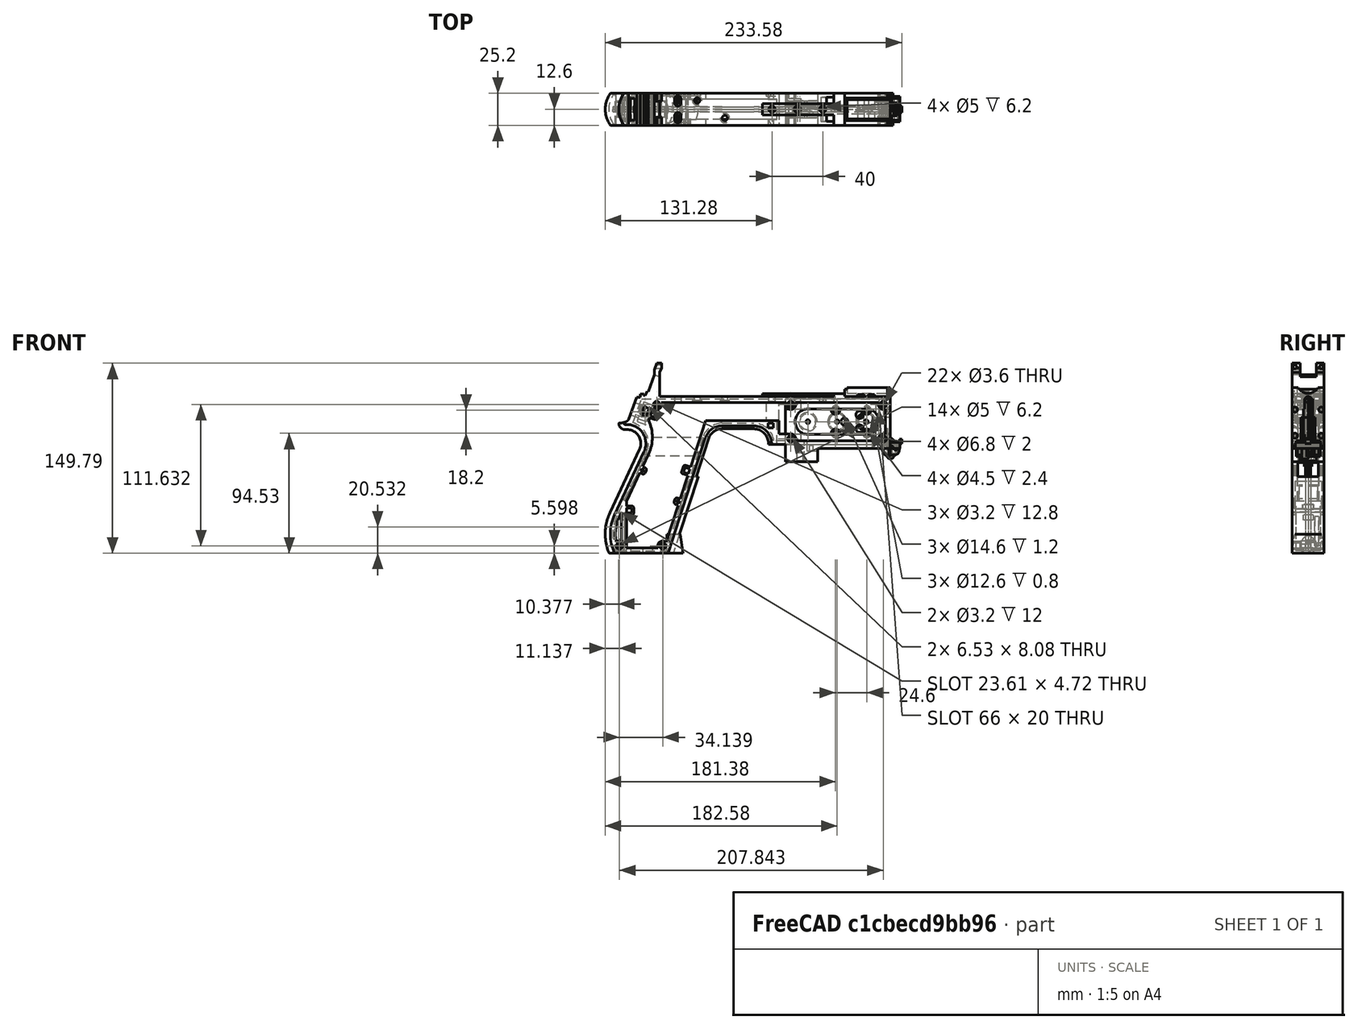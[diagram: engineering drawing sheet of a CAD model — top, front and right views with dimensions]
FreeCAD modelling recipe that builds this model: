
FCSTD DOCUMENT  (FreeCAD 1.0R39319 (Git))
Label: PICON-OF_ver_31
License: All rights reserved
LicenseURL: https://en.wikipedia.org/wiki/All_rights_reserved
objects: Sketcher::SketchObject×119, Part::Extrusion×75, Part::Cut×47, PartDesign::Pad×19, PartDesign::Chamfer×14, PartDesign::Pocket×12, PartDesign::Fillet×9, PartDesign::Body×8, Part::MultiFuse×6, PartDesign::SubtractivePipe×4, PartDesign::SubtractiveLoft×4, PartDesign::Plane×2, PartDesign::SubShapeBinder×2, Part::Part2DObjectPython×2, Part::Sweep×1, PartDesign::ShapeBinder×1, PartDesign::FeatureBase×1, Part::Cone×1, Part::Chamfer×1, Part::Mirroring×1, +1 more types
note: 573 computed .brp shape members not serialized (recipe doc carries the construction recipe); baked Part::Feature solids carry a one-line shape summary decoded from their .brp

FEATURE [Sketcher::SketchObject] Sketch  label="corpo principale"
  ArcFitTolerance = 1e-06
  AttacherType = Attacher::AttachEngine3D
  AttachmentSupport = -> [XZ_Plane]
  FullyConstrained = true
  MakeInternals = false
  MapMode = 5
  Placement = pos=(0,0,0) rot=(1,0,0;1.5708rad)
  sketch-geometry (65):
    g0: LineSegment StartX=0 StartY=0 StartZ=0 EndX=-57.2 EndY=0 EndZ=0
    g1: LineSegment StartX=-57.2 StartY=0 StartZ=0 EndX=-57.2 EndY=-10.4 EndZ=0
    g2: LineSegment StartX=-57.2 StartY=-10.4 StartZ=0 EndX=-82.8 EndY=-10.4 EndZ=0
    g3: LineSegment StartX=-82.8 StartY=-10.4 StartZ=0 EndX=-82.8 EndY=3.2 EndZ=0
    g4: LineSegment StartX=-82.8 StartY=3.2 StartZ=0 EndX=-93.6 EndY=3.2 EndZ=0
    g5: LineSegment StartX=-93.6 StartY=3.2 StartZ=0 EndX=-93.6 EndY=4 EndZ=0
    g6: LineSegment StartX=-107.6 StartY=18 StartZ=0 EndX=-132.428 EndY=18 EndZ=0
    g7: LineSegment StartX=-145.743 StartY=8.32624 StartZ=0 EndX=-175.232 EndY=-82.4316 EndZ=0
    g8: LineSegment StartX=-175.232 StartY=-82.4316 StartZ=0 EndX=-217.232 EndY=-82.4316 EndZ=0
    g9: LineSegment StartX=-217.232 StartY=-52.1862 StartZ=0 EndX=-193.988 EndY=-2.33927 EndZ=0
    g10: LineSegment StartX=-206.196 StartY=23.0857 StartZ=0 EndX=-199.861 EndY=40.4914 EndZ=0
    g11: LineSegment StartX=-199.861 StartY=40.4914 StartZ=0 EndX=-197.061 EndY=40.4914 EndZ=0
    g12: LineSegment StartX=-197.061 StartY=40.4914 StartZ=0 EndX=-197.061 EndY=42.8914 EndZ=0
    g13: LineSegment StartX=-197.061 StartY=42.8914 StartZ=0 EndX=-194.261 EndY=42.8914 EndZ=0
    g14: LineSegment StartX=-194.261 StartY=42.8914 StartZ=0 EndX=-194.535 EndY=42.1397 EndZ=0
    g15: LineSegment StartX=-194.535 StartY=42.1397 StartZ=0 EndX=-193.031 EndY=41.5924 EndZ=0
    g16: LineSegment StartX=-193.031 StartY=41.5924 StartZ=0 EndX=-191.663 EndY=45.3512 EndZ=0
    g17: LineSegment StartX=-191.663 StartY=45.3512 StartZ=0 EndX=-190.536 EndY=44.9408 EndZ=0
    g18: LineSegment StartX=-190.536 StartY=44.9408 StartZ=0 EndX=-185.747 EndY=58.0965 EndZ=0
    g19: LineSegment StartX=-185.747 StartY=58.0965 StartZ=0 EndX=-185.747 EndY=62.0965 EndZ=0
    g20: LineSegment StartX=-185.747 StartY=62.0965 StartZ=0 EndX=-183.832 EndY=67.3588 EndZ=0
    g21: LineSegment StartX=-183.832 StartY=67.3588 StartZ=0 EndX=-180.232 EndY=67.3588 EndZ=0
    g22: LineSegment StartX=-180.232 StartY=67.3588 StartZ=0 EndX=-180.232 EndY=63.7588 EndZ=0
    g23: LineSegment StartX=-180.232 StartY=63.7588 StartZ=0 EndX=-181.6 EndY=60 EndZ=0
    g24: LineSegment StartX=-181.6 StartY=60 StartZ=0 EndX=-181.6 EndY=41.2 EndZ=0
    g25: LineSegment StartX=-181.6 StartY=41.2 StartZ=0 EndX=-100.8 EndY=41.2 EndZ=0
    g26: LineSegment StartX=-36 StartY=43.2 StartZ=0 EndX=-36 EndY=41.2 EndZ=0
    g27: LineSegment StartX=0 StartY=48 StartZ=0 EndX=0 EndY=0 EndZ=0
    g28: LineSegment StartX=-209.901 StartY=19.85 StartZ=0 EndX=-209.901 EndY=20.1 EndZ=0
    g29: LineSegment StartX=-208.001 StartY=22 StartZ=0 EndX=-207.747 EndY=22 EndZ=0
    g30: LineSegment StartX=-207.583 StartY=19 StartZ=0 EndX=-209.051 EndY=19 EndZ=0
    g31: ArcOfCircle CenterX=-208.001 CenterY=20.1 CenterZ=0 NormalX=0 NormalY=0 NormalZ=1 AngleXU=0 Radius=1.9 StartAngle=1.5708 EndAngle=3.14159
    g32: GeomPoint [constr] X=-209.901 Y=22 Z=0
    g33: ArcOfCircle CenterX=-209.051 CenterY=19.85 CenterZ=0 NormalX=0 NormalY=0 NormalZ=1 AngleXU=0 Radius=0.85 StartAngle=3.14159 EndAngle=4.71239
    g34: GeomPoint [constr] X=-209.901 Y=19 Z=0
    g35: ArcOfCircle CenterX=-207.747 CenterY=23.65 CenterZ=0 NormalX=0 NormalY=0 NormalZ=1 AngleXU=0 Radius=1.65 StartAngle=4.71239 EndAngle=5.93412
    g36: GeomPoint [constr] X=-206.591 Y=22 Z=0
    g37: LineSegment StartX=-4 StartY=6 StartZ=0 EndX=-4 EndY=36.4 EndZ=0
    g38: LineSegment StartX=-4 StartY=36.4 StartZ=0 EndX=-185.2 EndY=36.4 EndZ=0
    g39: LineSegment StartX=-185.2 StartY=36.4 StartZ=0 EndX=-190.441 EndY=22 EndZ=0
    g40: LineSegment StartX=-214.575 StartY=-78.4316 StartZ=0 EndX=-178.142 EndY=-78.4316 EndZ=0
    g41: LineSegment StartX=-178.142 StartY=-78.4316 StartZ=0 EndX=-145.51 EndY=22 EndZ=0
    g42: LineSegment StartX=-145.51 StartY=22 StartZ=0 EndX=-87.91 EndY=22 EndZ=0
    g43: LineSegment StartX=-87.91 StartY=22 StartZ=0 EndX=-87.91 EndY=11.6 EndZ=0
    g44: LineSegment StartX=-87.91 StartY=11.6 StartZ=0 EndX=-80.11 EndY=11.6 EndZ=0
    g45: LineSegment StartX=-80.11 StartY=11.6 StartZ=0 EndX=-80.11 EndY=6 EndZ=0
    g46: LineSegment StartX=-80.11 StartY=6 StartZ=0 EndX=-4 EndY=6 EndZ=0
    g47: LineSegment StartX=-190.363 StartY=-4.02975 StartZ=0 EndX=-213.607 EndY=-53.8767 EndZ=0
    g48: ArcOfCircle CenterX=-132.428 CenterY=4 CenterZ=0 NormalX=0 NormalY=0 NormalZ=1 AngleXU=0 Radius=14 StartAngle=1.5708 EndAngle=2.82743
    g49: GeomPoint [constr] X=-142.6 Y=18 Z=0
    g50: ArcOfCircle CenterX=-107.6 CenterY=4 CenterZ=0 NormalX=0 NormalY=0 NormalZ=1 AngleXU=0 Radius=14 StartAngle=0 EndAngle=1.5708
    g51: GeomPoint [constr] X=-93.6 Y=18 Z=0
    g52: ArcOfCircle CenterX=-184.801 CenterY=-67.3089 CenterZ=0 NormalX=0 NormalY=0 NormalZ=1 AngleXU=0 Radius=35.7833 StartAngle=2.70526 EndAngle=3.57792
    g53: ArcOfCircle CenterX=-207.583 CenterY=4 CenterZ=0 NormalX=0 NormalY=0 NormalZ=1 AngleXU=0 Radius=15 StartAngle=5.84685 EndAngle=7.85398
    g54: LineSegment [constr] StartX=-213.607 StartY=-53.8767 StartZ=0 EndX=-217.232 EndY=-52.1862 EndZ=0
    g55: ArcOfCircle CenterX=-184.801 CenterY=-67.3089 CenterZ=0 NormalX=0 NormalY=0 NormalZ=1 AngleXU=0 Radius=31.7833 StartAngle=2.70526 EndAngle=3.49911
    g56: ArcOfCircle CenterX=-218.095 CenterY=8.90192 CenterZ=0 NormalX=0 NormalY=0 NormalZ=1 AngleXU=0 Radius=30.5989 StartAngle=5.84685 EndAngle=6.72553
    g57: LineSegment StartX=-44.6 StartY=43.2 StartZ=0 EndX=-36 EndY=43.2 EndZ=0
    g58: LineSegment StartX=-100.8 StartY=41.2 StartZ=0 EndX=-44.6 EndY=41.2 EndZ=0
    g59: LineSegment StartX=-44.6 StartY=41.2 StartZ=0 EndX=-44.6 EndY=43.2 EndZ=0
    g60: LineSegment StartX=-2.4 StartY=48 StartZ=0 EndX=0 EndY=48 EndZ=0
    g61: LineSegment StartX=-36 StartY=41.2 StartZ=0 EndX=-2.4 EndY=41.2 EndZ=0
    g62: LineSegment StartX=-2.4 StartY=41.2 StartZ=0 EndX=-2.4 EndY=48 EndZ=0
    g63: LineSegment [constr] StartX=-181.6 StartY=36.4 StartZ=0 EndX=-152.209 EndY=36.4 EndZ=0
    g64: LineSegment [constr] StartX=-181.6 StartY=36.4 StartZ=0 EndX=-130.41 EndY=36.4 EndZ=0
  constraints (183):
    c: Coincident(g-1,g0)
    c: PointOnObject(g0,g-1)
    c: Coincident(g0,g1)
    c: Vertical(g1)
    c: Coincident(g1,g2)
    c: Horizontal(g2)
    c: Coincident(g2,g3)
    c: Vertical(g3)
    c: Coincident(g3,g4)
    c: Coincident(g4,g5)
    c: Vertical(g5)
    c: Horizontal(g6)
    c: Coincident(g7,g8)
    c: Horizontal(g8)
    c: Coincident(g10,g11)
    c: Horizontal(g11)
    c: Coincident(g11,g12)
    c: Vertical(g12)
    c: Coincident(g12,g13)
    c: Horizontal(g13)
    c: Coincident(g13,g14)
    c: Coincident(g14,g15)
    c: Coincident(g15,g16)
    c: Coincident(g16,g17)
    c: Coincident(g17,g18)
    c: Coincident(g18,g19)
    c: Vertical(g19)
    c: Coincident(g19,g20)
    c: Coincident(g20,g21)
    c: Horizontal(g21)
    c: Coincident(g21,g22)
    c: Vertical(g22)
    c: Coincident(g22,g23)
    c: Coincident(g23,g24)
    c: Vertical(g24)
    c: Coincident(g24,g25)
    c: Horizontal(g25)
    c: Coincident(g57,g26)
    c: Vertical(g26)
    c: Coincident(g26,g61)
    c: PointOnObject(g60,g-2)
    c: Coincident(g60,g27)
    c: Coincident(g27,g0)
    c: DistanceY(g27,g27) = 48
    c: DistanceY(g1,g1) = 10.4
    c: DistanceX(g0,g0) = 57.2
    c: DistanceX(g2,g2) = 25.6
    c: Horizontal(g4)
    c: DistanceY(g3,g3) = 13.6
    c: DistanceX(g4,g4) = 10.8
    c: DistanceY(g5,g51) = 14.8
    c: DistanceX(g49,g51) = 49
    c: Distance(g7,g49) = 105.6
    c: DistanceX(g61,g60) = 36
    c: DistanceX(g25,g25) = 80.8
    c: DistanceY(g24,g24) = 18.8
    c: DistanceY(g22,g22) = 3.6
    c: Distance(g23) = 4
    c: Angle(g-1,g23) = 1.22173
    c: DistanceX(g21,g21) = 3.6
    c: Distance(g20) = 5.6
    c: Angle(g-1,g20) = 1.22173
    c: DistanceY(g19,g19) = 4
    c: Distance(g18) = 14
    c: Angle(g-1,g18) = 1.22173
    c: Distance(g17) = 1.2
    c: Distance(g16) = 4
    c: Angle(g16) = 1.22173
    c: Perpendicular(g18,g17)
    c: Distance(g15) = 1.6
    c: Perpendicular(g16,g15)
    c: Distance(g14) = 0.8
    c: DistanceX(g13,g13) = 2.8
    c: Perpendicular(g15,g14)
    c: DistanceY(g12,g12) = 2.4
    c: DistanceX(g11,g11) = 2.8
    c: Distance(g9) = 55
    c: Angle(g9,g-1) = 2.00713
    c: Horizontal(g29)
    c: Vertical(g28)
    c: Horizontal(g30)
    c: PointOnObject(g32,g29)
    c: PointOnObject(g32,g28)
    c: Tangent(g29,g31) = 1.5708
    c: Tangent(g28,g31) = 1.5708
    c: PointOnObject(g34,g28)
    c: PointOnObject(g34,g30)
    c: Tangent(g28,g33) = 1.5708
    c: Tangent(g30,g33) = 1.5708
    c: PointOnObject(g36,g29)
    c: PointOnObject(g36,g10)
    c: Tangent(g29,g35) = -1.5708
    c: Tangent(g10,g35) = -1.5708
    c: Angle(g-1,g10) = 1.22173
    c: Radius(g35) = 1.65
    c: Vertical(g37)
    c: Coincident(g37,g38)
    c: Horizontal(g38)
    c: Coincident(g38,g39)
    c: Horizontal(g40)
    c: Coincident(g40,g41)
    c: Coincident(g41,g42)
    c: Horizontal(g42)
    c: Coincident(g42,g43)
    c: Vertical(g43)
    c: Coincident(g43,g44)
    c: Horizontal(g44)
    c: Coincident(g44,g45)
    c: Vertical(g45)
    c: Coincident(g45,g46)
    c: Coincident(g46,g37)
    c: Horizontal(g46)
    c: DistanceY(g0,g37) = 6
    c: DistanceX(g37,g0) = 4
    c: DistanceY(g37,g25) = 4.8
    c: DistanceX(g38,g38) = 181.2
    c: DistanceX(g42,g42) = 57.6
    c: DistanceY(g49,g41) = 4
    c: DistanceX(g41,g49) = 2.91
    c: DistanceY(g43,g43) = 10.4
    c: DistanceX(g44,g44) = 7.8
    c: DistanceY(g7,g40) = 4
    c: Distance(g47) = 55
    c: Angle(g-1,g39) = 1.22173
    c: PointOnObject(g49,g7)
    c: PointOnObject(g49,g6)
    c: Tangent(g7,g48) = -1.5708
    c: Tangent(g6,g48) = -1.5708
    c: PointOnObject(g51,g5)
    c: PointOnObject(g51,g6)
    c: Tangent(g5,g50) = -1.5708
    c: Tangent(g6,g50) = -1.5708
    c: Radius(g50) = 14
    c: Radius(g48) = 14
    c: DistanceX(g8,g8) = 42
    c: Angle(g7,g-1) = 1.88496
    c: Parallel(g41,g7)
    c: Parallel(g47,g9)
    c: Coincident(g52,g8)
    c: Tangent(g52,g9) = 1.5708
    c: DistanceX(g9,g8) = 0
    c: Tangent(g53,g9) = -1.5708
    c: Tangent(g53,g30) = -1.5708
    c: Diameter(g53) = 30
    c: DistanceY(g53,g0) = -4
    c: Coincident(g54,g47)
    c: Distance(g54) = 4
    c: Coincident(g54,g9)
    c: Coincident(g55,g40)
    c: Tangent(g55,g47) = -1.5708
    c: Coincident(g52,g55)
    c: Coincident(g56,g39)
    c: Tangent(g56,g47) = 1.5708
    c: Horizontal(g57)
    c: DistanceX(g57,g57) = 8.6
    c: Coincident(g58,g25)
    c: Horizontal(g58)
    c: Coincident(g59,g58)
    c: Vertical(g59)
    c: DistanceY(g58,g57) = 2
    c: DistanceX(g58,g58) = 56.2
    c: Coincident(g59,g57)
    c: DistanceY(g41,g36) = 0
    c: DistanceY(g36,g39) = 0
    c: DistanceY(g28,g28) = 0.25
    c: DistanceX(g30,g36) = 2.46
    c: DistanceX(g28,g29) = 1.9
    c: Coincident(g62,g60)
    c: Horizontal(g60)
    c: DistanceX(g62,g27) = 2.4
    c: Coincident(g61,g62)
    c: DistanceY(g26,g26) = 2
    c: Vertical(g62)
    c: DistanceY(g61,g60) = 6.8
    c: Horizontal(g61)
    c: Distance(g63) = 29.391
    c: PointOnObject(g63,g38)
    c: PointOnObject(g63,g38)
    c: Distance(g64) = 51.19
    c: PointOnObject(g64,g38)
    c: PointOnObject(g64,g38)
    c: DistanceX(g24,g63) = 0
    c: DistanceX(g24,g64) = 0
FEATURE [Part::Extrusion] Extrude  label="Extrude corpo principale"
  Base = -> Sketch
  Dir = (0,-1,2e-16)
  DirMode = 2
  FaceMakerClass = Part::FaceMakerBullseye
  FaceMakerMode = 3
  LengthFwd = 25.2
  LengthRev = 12.6
  Solid = true
  Symmetric = true
FEATURE [Sketcher::SketchObject] Sketch002  label="scavo grilletto"
  ArcFitTolerance = 1e-06
  AttachmentSupport = -> [XZ_Plane]
  ExternalGeometry = -> [Sketch]
  FullyConstrained = true
  MakeInternals = false
  MapMode = 5
  Placement = pos=(0,0,0) rot=(1,0,0;1.5708rad)
  sketch-geometry (4):
    g0: LineSegment StartX=-89.51 StartY=22 StartZ=0 EndX=-152.71 EndY=22 EndZ=0
    g1: LineSegment StartX=-152.71 StartY=22 StartZ=0 EndX=-167.006 EndY=-22 EndZ=0
    g2: LineSegment StartX=-167.006 StartY=-22 StartZ=0 EndX=-89.51 EndY=-22 EndZ=0
    g3: LineSegment StartX=-89.51 StartY=-22 StartZ=0 EndX=-89.51 EndY=22 EndZ=0
  constraints (12):
    c: Horizontal(g0)
    c: Coincident(g0,g1)
    c: Coincident(g1,g2)
    c: Horizontal(g2)
    c: Coincident(g2,g3)
    c: Coincident(g3,g0)
    c: Vertical(g3)
    c: Angle(g1,g0) = 1.88496
    c: DistanceY(g3,g3) = 44
    c: DistanceX(g0,g0) = 63.2
    c: DistanceX(g0,g-3) = 1.6
    c: DistanceY(g-3,g0) = 0
FEATURE [Sketcher::SketchObject] Sketch004  label="traiettoria arrotondamento impugnatura anteriore"
  ArcFitTolerance = 1e-06
  AttachmentSupport = -> [XZ_Plane]
  ExternalGeometry = -> [Sketch]
  FullyConstrained = true
  MakeInternals = false
  MapMode = 5
  Placement = pos=(0,0,0) rot=(1,0,0;1.5708rad)
  sketch-geometry (13):
    g0: LineSegment StartX=-175.232 StartY=-82.4316 StartZ=0 EndX=-145.743 EndY=8.32624 EndZ=0
    g1: LineSegment StartX=-93.6 StartY=3.2 StartZ=0 EndX=-93.6 EndY=4 EndZ=0
    g2: LineSegment StartX=-132.428 StartY=18 StartZ=0 EndX=-107.6 EndY=18 EndZ=0
    g3: ArcOfCircle CenterX=-132.428 CenterY=4 CenterZ=0 NormalX=0 NormalY=0 NormalZ=1 AngleXU=0 Radius=14 StartAngle=1.5708 EndAngle=2.82743
    g4: ArcOfCircle CenterX=-107.6 CenterY=4 CenterZ=0 NormalX=0 NormalY=0 NormalZ=1 AngleXU=0 Radius=14 StartAngle=0 EndAngle=1.5708
    g5: LineSegment StartX=-175.232 StartY=-82.4316 StartZ=0 EndX=-217.232 EndY=-82.4316 EndZ=0
    g6: LineSegment StartX=-217.232 StartY=-52.1862 StartZ=0 EndX=-193.988 EndY=-2.33927 EndZ=0
    g7: LineSegment StartX=-209.051 StartY=19 StartZ=0 EndX=-207.583 EndY=19 EndZ=0
    g8: LineSegment StartX=-209.901 StartY=20.1 StartZ=0 EndX=-209.901 EndY=19.85 EndZ=0
    g9: ArcOfCircle CenterX=-184.801 CenterY=-67.3089 CenterZ=0 NormalX=0 NormalY=0 NormalZ=1 AngleXU=0 Radius=35.7833 StartAngle=2.70526 EndAngle=3.57792
    g10: ArcOfCircle CenterX=-207.583 CenterY=4 CenterZ=0 NormalX=0 NormalY=0 NormalZ=1 AngleXU=0 Radius=15 StartAngle=5.84685 EndAngle=7.85398
    g11: ArcOfCircle CenterX=-209.051 CenterY=19.85 CenterZ=0 NormalX=0 NormalY=0 NormalZ=1 AngleXU=0 Radius=0.85 StartAngle=3.14159 EndAngle=4.71239
    g12: ArcOfCircle CenterX=-208.001 CenterY=20.1 CenterZ=0 NormalX=0 NormalY=0 NormalZ=1 AngleXU=0 Radius=1.9 StartAngle=1.5708 EndAngle=3.14159
  constraints (26):
    c: Coincident(g0,g-3)
    c: Coincident(g0,g-6)
    c: Coincident(g1,g-8)
    c: Coincident(g1,g-7)
    c: Coincident(g2,g-5)
    c: Coincident(g2,g-4)
    c: Coincident(g3,g2)
    c: Tangent(g3,g0) = 1.5708
    c: Coincident(g4,g1)
    c: Tangent(g4,g2) = 1.5708
    c: Coincident(g5,g0)
    c: Coincident(g5,g-9)
    c: Coincident(g6,g-12)
    c: Coincident(g6,g-11)
    c: Coincident(g7,g-15)
    c: Coincident(g7,g-14)
    c: Coincident(g8,g-16)
    c: Coincident(g8,g-17)
    c: Tangent(g9,g6) = 1.5708
    c: Coincident(g9,g5)
    c: Coincident(g10,g7)
    c: Tangent(g10,g6) = -1.5708
    c: Tangent(g11,g7) = -1.5708
    c: Coincident(g11,g8)
    c: Tangent(g12,g8) = -1.5708
    c: Coincident(g12,g-17)
FEATURE [PartDesign::Plane] DatumPlane  label="Piano per disegno arrotondamento impugnatura"
  AttachmentSupport = -> [Sketch]
  Length = 68.5841
  MapMode = 7
  Placement = pos=(-145.743,1.8e-15,8.32624) rot=(0.154555,0.154555,0.97582;1.59527rad)
  ResizeMode = 0
  Width = 191.269
FEATURE [Sketcher::SketchObject] Sketch005  label="forma arrotondamento impugnatura anteriore"
  ArcFitTolerance = 1e-06
  AttachmentSupport = -> [DatumPlane]
  FullyConstrained = true
  MakeInternals = false
  MapMode = 5
  Placement = pos=(-145.743,1.8e-15,8.32624) rot=(0.154555,0.154555,0.97582;1.59527rad)
  sketch-geometry (5):
    g0: GeomPoint [constr] X=0 Y=-4 Z=0
    g1: GeomPoint [constr] X=-12.6 Y=7.1e-15 Z=0
    g2: GeomPoint [constr] X=12.6 Y=4.97e-14 Z=0
    g3: LineSegment StartX=-12.6 StartY=7.1e-15 StartZ=0 EndX=12.6 EndY=4.97e-14 EndZ=0
    g4: ArcOfCircle CenterX=-3.88e-14 CenterY=17.845 CenterZ=0 NormalX=0 NormalY=0 NormalZ=1 AngleXU=0 Radius=21.845 StartAngle=4.09759 EndAngle=5.32718
  constraints (11):
    c: DistanceY(g0,g-1) = 4
    c: DistanceX(g-1,g0) = 0
    c: DistanceX(g1,g-1) = 12.6
    c: DistanceX(g-1,g2) = 12.6
    c: DistanceY(g-1,g2) = 0
    c: DistanceY(g-1,g1) = 0
    c: Coincident(g3,g1)
    c: Coincident(g3,g2)
    c: Coincident(g4,g1)
    c: Coincident(g4,g2)
    c: PointOnObject(g0,g4)
FEATURE [Part::Sweep] Sweep  label="Sweep impugnatura"
  Frenet = true
  Sections = -> [Sketch005]
  Solid = true
  Spine = -> Sketch [Edge32,Edge33,Edge34,Edge35,Edge36,Edge37,Edge38,Edge39,Edge40,Edge41,Edge42,Edge43,Edge44]
  Transition = 1
FEATURE [Sketcher::SketchObject] Sketch008  label="buchi e pulizie varie"
  ArcFitTolerance = 1e-06
  AttachmentSupport = -> [XZ_Plane]
  ExternalGeometry = -> [Sketch]
  FullyConstrained = true
  MakeInternals = false
  MapMode = 5
  Placement = pos=(0,0,0) rot=(1,0,0;1.5708rad)
  sketch-geometry (26):
    g0: LineSegment StartX=-96.278 StartY=20.155 StartZ=0 EndX=-92.278 EndY=20.155 EndZ=0
    g1: LineSegment StartX=-92.278 StartY=20.155 StartZ=0 EndX=-92.278 EndY=16.155 EndZ=0
    g2: LineSegment StartX=-92.278 StartY=16.155 StartZ=0 EndX=-96.278 EndY=16.155 EndZ=0
    g3: LineSegment StartX=-96.278 StartY=16.155 StartZ=0 EndX=-96.278 EndY=20.155 EndZ=0
    g4: LineSegment StartX=-222.232 StartY=-82.4316 StartZ=0 EndX=-170.232 EndY=-82.4316 EndZ=0
    g5: LineSegment StartX=-170.232 StartY=-82.4316 StartZ=0 EndX=-170.232 EndY=-86.4316 EndZ=0
    g6: LineSegment StartX=-170.232 StartY=-86.4316 StartZ=0 EndX=-222.232 EndY=-86.4316 EndZ=0
    g7: LineSegment StartX=-222.232 StartY=-86.4316 StartZ=0 EndX=-222.232 EndY=-82.4316 EndZ=0
    g8: LineSegment StartX=-213.901 StartY=20.1 StartZ=0 EndX=-213.901 EndY=26 EndZ=0
    g9: LineSegment StartX=-213.901 StartY=26 StartZ=0 EndX=-206.196 EndY=26 EndZ=0
    g10: LineSegment StartX=-17.4 StartY=42.8 StartZ=0 EndX=-12.4 EndY=42.8 EndZ=0
    g11: LineSegment StartX=-12.4 StartY=42.8 StartZ=0 EndX=-12.4 EndY=41.2 EndZ=0
    g12: LineSegment StartX=-12.4 StartY=41.2 StartZ=0 EndX=-17.4 EndY=41.2 EndZ=0
    g13: LineSegment StartX=-17.4 StartY=41.2 StartZ=0 EndX=-17.4 EndY=42.8 EndZ=0
    g14: LineSegment StartX=-25.9 StartY=42.8 StartZ=0 EndX=-20.9 EndY=42.8 EndZ=0
    g15: LineSegment StartX=-20.9 StartY=42.8 StartZ=0 EndX=-20.9 EndY=41.2 EndZ=0
    g16: LineSegment StartX=-20.9 StartY=41.2 StartZ=0 EndX=-25.9 EndY=41.2 EndZ=0
    g17: LineSegment StartX=-25.9 StartY=41.2 StartZ=0 EndX=-25.9 EndY=42.8 EndZ=0
    g18: GeomPoint [constr] X=-206.196 Y=23.0857 Z=0
    g19: GeomPoint [constr] X=-213.901 Y=20.1 Z=0
    g20: BSplineCurve PolesCount=4 KnotsCount=2 Degree=3 IsPeriodic=0
    g21-g24: Circle [constr] x4 (B-spline internal-alignment scaffolding for g20; pole/knot coordinates omitted)
    g25: LineSegment StartX=-206.196 StartY=26 StartZ=0 EndX=-206.196 EndY=23.0857 EndZ=0
  constraints (73):
    c: Horizontal(g0)
    c: Coincident(g1,g0)
    c: Vertical(g1)
    c: Coincident(g2,g1)
    c: Horizontal(g2)
    c: Coincident(g3,g2)
    c: Coincident(g3,g0)
    c: Vertical(g3)
    c: DistanceX(g0,g-4) = 4.368
    c: DistanceY(g0,g-4) = 1.845
    c: DistanceY(g1,g1) = 4
    c: DistanceX(g2,g2) = 4
    c: Horizontal(g4)
    c: Coincident(g5,g4)
    c: Vertical(g5)
    c: Coincident(g6,g5)
    c: Horizontal(g6)
    c: Coincident(g7,g6)
    c: Coincident(g7,g4)
    c: Vertical(g7)
    c: DistanceY(g7,g7) = 4
    c: DistanceX(g4,g-5) = 5
    c: DistanceX(g-5,g4) = 5
    c: DistanceY(g4,g-5) = 0
    c: Coincident(g9,g8)
    c: Parallel(g9,g-6)
    c: DistanceX(g8,g-8) = 4
    c: Horizontal(g10)
    c: Coincident(g11,g10)
    c: Vertical(g11)
    c: Coincident(g12,g11)
    c: Horizontal(g12)
    c: Coincident(g13,g12)
    c: Coincident(g13,g10)
    c: Vertical(g13)
    c: Horizontal(g14)
    c: Coincident(g15,g14)
    c: Vertical(g15)
    c: Coincident(g16,g15)
    c: Horizontal(g16)
    c: Coincident(g17,g16)
    c: Coincident(g17,g14)
    c: Vertical(g17)
    c: DistanceY(g11,g10) = 1.6
    c: DistanceX(g10,g10) = 5
    c: DistanceY(g15,g14) = 1.6
    c: DistanceX(g14,g14) = 5
    c: DistanceX(g15,g12) = 3.5
    c: DistanceX(g11,g-9) = 10
    c: DistanceY(g-9,g11) = 0
    c: DistanceY(g-9,g15) = 0
    c: Perpendicular(g8,g9)
    c: DistanceY(g-7,g9) = 4
    c: DistanceY(g8,g-8) = 0
    c: InternalAlignment(g18,g20)
    c: InternalAlignment(g19,g20)
    c: InternalAlignment(g21,g20)
    c: Weight(g21) = 1
    c: InternalAlignment(g22,g20)
    c: Equal(g22,g21)
    c: InternalAlignment(g23,g20)
    c: Equal(g23,g21)
    c: InternalAlignment(g24,g20)
    c: Equal(g24,g21)
    c: Coincident(g18,g-12)
    c: Coincident(g19,g8)
    c: Coincident(g25,g9)
    c: Coincident(g25,g20)
    c: Vertical(g25)
    c: DistanceY(g20,g23) = 0
    c: DistanceY(g22,g18) = 2.26
    c: DistanceX(g22,g18) = 0.93
    c: DistanceX(g20,g23) = 2.9
FEATURE [Part::Extrusion] Extrude004  label="Extrude Buchi e pulizie varie"
  Base = -> Sketch008
  Dir = (0,-1,2e-16)
  DirMode = 2
  FaceMakerClass = Part::FaceMakerBullseye
  FaceMakerMode = 3
  LengthFwd = 25.2
  LengthRev = 0
  Solid = true
  Symmetric = true
FEATURE [Sketcher::SketchObject] Sketch009  label="rinforzi"
  ArcFitTolerance = 1e-06
  AttachmentSupport = -> [XZ_Plane]
  ExternalGeometry = -> [Sketch]
  FullyConstrained = true
  MakeInternals = false
  MapMode = 5
  Placement = pos=(0,0,0) rot=(1,0,0;1.5708rad)
  sketch-geometry (9):
    g0: LineSegment StartX=-87.91 StartY=22 StartZ=0 EndX=-87.91 EndY=36.4 EndZ=0
    g1: LineSegment StartX=-87.91 StartY=36.4 StartZ=0 EndX=-97.91 EndY=36.4 EndZ=0
    g2: LineSegment StartX=-97.91 StartY=36.4 StartZ=0 EndX=-97.91 EndY=22 EndZ=0
    g3: LineSegment StartX=-97.91 StartY=22 StartZ=0 EndX=-87.91 EndY=22 EndZ=0
    g4: LineSegment StartX=-149.713 StartY=9.06563 StartZ=0 EndX=-154.586 EndY=-5.93437 EndZ=0
    g5: LineSegment StartX=-154.586 StartY=-5.93437 StartZ=0 EndX=-191.863 EndY=-5.93437 EndZ=0
    g6: LineSegment StartX=-191.863 StartY=-5.93437 StartZ=0 EndX=-191.863 EndY=9.06563 EndZ=0
    g7: LineSegment StartX=-191.863 StartY=9.06563 StartZ=0 EndX=-149.713 EndY=9.06563 EndZ=0
    g8: LineSegment [constr] StartX=-145.51 StartY=22 StartZ=0 EndX=-149.713 EndY=9.06563 EndZ=0
  constraints (25):
    c: Vertical(g0)
    c: Coincident(g1,g0)
    c: Horizontal(g1)
    c: Coincident(g2,g1)
    c: Vertical(g2)
    c: Coincident(g3,g2)
    c: Coincident(g3,g0)
    c: Horizontal(g3)
    c: Coincident(g0,g-4)
    c: DistanceX(g3,g3) = 10
    c: DistanceY(g0,g-3) = 0
    c: Coincident(g5,g4)
    c: Horizontal(g5)
    c: Coincident(g6,g5)
    c: Vertical(g6)
    c: Coincident(g7,g6)
    c: Coincident(g7,g4)
    c: Horizontal(g7)
    c: Distance(g8) = 13.6
    c: Parallel(g-6,g8)
    c: Coincident(g-6,g8)
    c: Parallel(g4,g-6)
    c: DistanceY(g4,g4) = 15
    c: Coincident(g4,g8)
    c: DistanceX(g-5,g5) = -1.5
FEATURE [Part::Extrusion] Extrude001  label="Extrude scavo grilletto"
  Base = -> Sketch002
  Dir = (0,-1,2e-16)
  DirMode = 2
  FaceMakerClass = Part::FaceMakerBullseye
  FaceMakerMode = 3
  LengthFwd = 16
  LengthRev = 0
  Solid = true
  Symmetric = true
FEATURE [Part::Extrusion] Extrude005  label="Extrude Rinforzi"
  Base = -> Sketch009
  Dir = (0,-1,2e-16)
  DirMode = 2
  FaceMakerClass = Part::FaceMakerBullseye
  FaceMakerMode = 3
  LengthFwd = 2
  LengthRev = 0
  Placement = pos=(0,12.6,0) rot=(0,0,1;0rad)
  Solid = true
  Symmetric = false
FEATURE [PartDesign::ShapeBinder] CopyCut
  TraceSupport = false
FEATURE [PartDesign::Plane] DatumPlane001
  AttachmentSupport = -> [CopyCut]
  Length = 60
  MapMode = 5
  Placement = pos=(0,12.6,0) rot=(0,0.707107,0.707107;3.14159rad)
  ResizeMode = 0
  Width = 60
FEATURE [Sketcher::SketchObject] Sketch010  label="buco neopixel"
  ArcFitTolerance = 1e-06
  AttachmentSupport = -> [XZ_Plane]
  ExternalGeometry = -> [Sketch]
  FullyConstrained = true
  MakeInternals = false
  MapMode = 5
  Placement = pos=(0,0,0) rot=(1,0,0;1.5708rad)
  sketch-geometry (5):
    g0: LineSegment [constr] StartX=-199.861 StartY=40.4914 StartZ=0 EndX=-201.368 EndY=36.3521 EndZ=0
    g1: LineSegment StartX=-201.368 StartY=36.3521 StartZ=0 EndX=-204.932 EndY=26.5605 EndZ=0
    g2: LineSegment StartX=-201.368 StartY=36.3521 StartZ=0 EndX=-180.2 EndY=28.6477 EndZ=0
    g3: LineSegment StartX=-180.2 StartY=28.6477 StartZ=0 EndX=-183.764 EndY=18.8561 EndZ=0
    g4: LineSegment StartX=-183.764 StartY=18.8561 StartZ=0 EndX=-204.932 EndY=26.5605 EndZ=0
  constraints (14):
    c: Parallel(g0,g-3)
    c: Distance(g0) = 4.405
    c: Coincident(g0,g-3)
    c: Coincident(g2,g1)
    c: Coincident(g3,g2)
    c: Coincident(g4,g3)
    c: Coincident(g4,g1)
    c: Parallel(g1,g-3)
    c: Distance(g1) = 10.42
    c: Coincident(g1,g0)
    c: Parallel(g2,g4)
    c: Perpendicular(g1,g2)
    c: DistanceX(g-4,g2) = 5
    c: Parallel(g3,g1)
FEATURE [Part::Extrusion] Extrude006  label="Extrude buco neopixel"
  Base = -> Sketch010
  Dir = (0,-1,2e-16)
  DirMode = 2
  FaceMakerClass = Part::FaceMakerBullseye
  FaceMakerMode = 3
  LengthFwd = 17.2
  LengthRev = 0
  Solid = true
  Symmetric = true
FEATURE [Sketcher::SketchObject] Sketch011  label="fermo grilletto"
  ArcFitTolerance = 1e-06
  AttachmentSupport = -> [XZ_Plane]
  ExternalGeometry = -> [Sketch]
  FullyConstrained = true
  MakeInternals = false
  MapMode = 5
  Placement = pos=(0,0,0) rot=(1,0,0;1.5708rad)
  sketch-geometry (18):
    g0: LineSegment [constr] StartX=-145.51 StartY=22 StartZ=0 EndX=-157.347 EndY=-14.4293 EndZ=0
    g1: LineSegment [constr] StartX=-157.347 StartY=-14.4293 StartZ=0 EndX=-157.841 EndY=-15.951 EndZ=0
    g2: LineSegment StartX=-161.151 StartY=-13.1932 StartZ=0 EndX=-155.825 EndY=-14.9237 EndZ=0
    g3: LineSegment StartX=-163.167 StartY=-14.2205 StartZ=0 EndX=-164.403 EndY=-18.0247 EndZ=0
    g4: LineSegment StartX=-163.376 StartY=-20.0408 StartZ=0 EndX=-158.05 EndY=-21.7713 EndZ=0
    g5: LineSegment StartX=-158.05 StartY=-21.7713 StartZ=0 EndX=-155.825 EndY=-14.9237 EndZ=0
    g6: LineSegment StartX=-161.645 StartY=-14.7149 StartZ=0 EndX=-157.841 EndY=-15.951 EndZ=0
    g7: LineSegment StartX=-157.841 StartY=-15.951 StartZ=0 EndX=-159.077 EndY=-19.7552 EndZ=0
    g8: LineSegment StartX=-159.077 StartY=-19.7552 StartZ=0 EndX=-162.881 EndY=-18.5191 EndZ=0
    g9: LineSegment StartX=-162.881 StartY=-18.5191 StartZ=0 EndX=-161.645 EndY=-14.7149 EndZ=0
    g10: LineSegment [constr] StartX=-161.645 StartY=-14.7149 StartZ=0 EndX=-161.151 EndY=-13.1932 EndZ=0
    g11: LineSegment [constr] StartX=-159.077 StartY=-19.7552 StartZ=0 EndX=-157.555 EndY=-20.2496 EndZ=0
    g12: LineSegment [constr] StartX=-159.077 StartY=-19.7552 StartZ=0 EndX=-159.572 EndY=-21.2769 EndZ=0
    g13: LineSegment [constr] StartX=-161.645 StartY=-14.7149 StartZ=0 EndX=-163.167 EndY=-14.2205 EndZ=0
    g14: ArcOfCircle CenterX=-161.645 CenterY=-14.7149 CenterZ=0 NormalX=0 NormalY=0 NormalZ=1 AngleXU=0 Radius=1.6 StartAngle=1.25664 EndAngle=2.82743
    g15: GeomPoint [constr] X=-162.673 Y=-12.6988 Z=0
    g16: ArcOfCircle CenterX=-162.881 CenterY=-18.5191 CenterZ=0 NormalX=0 NormalY=0 NormalZ=1 AngleXU=0 Radius=1.6 StartAngle=2.82743 EndAngle=4.39823
    g17: GeomPoint [constr] X=-164.897 Y=-19.5464 Z=0
  constraints (48):
    c: Parallel(g0,g-3)
    c: Distance(g0) = 38.304
    c: Coincident(g0,g-3)
    c: Parallel(g1,g-3)
    c: Distance(g1) = 1.6
    c: Coincident(g1,g0)
    c: Coincident(g5,g4)
    c: Coincident(g5,g2)
    c: Coincident(g7,g6)
    c: Coincident(g8,g7)
    c: Coincident(g9,g8)
    c: Coincident(g9,g6)
    c: Parallel(g7,g-3)
    c: Parallel(g9,g7)
    c: Perpendicular(g6,g7)
    c: Parallel(g6,g8)
    c: Distance(g6) = 4
    c: Distance(g9) = 4
    c: Parallel(g5,g7)
    c: Parallel(g9,g3)
    c: Parallel(g2,g6)
    c: Parallel(g4,g8)
    c: Parallel(g13,g6)
    c: Parallel(g10,g9)
    c: Parallel(g11,g8)
    c: Parallel(g12,g7)
    c: Distance(g10) = 1.6
    c: Distance(g13) = 1.6
    c: Distance(g12) = 1.6
    c: Distance(g11) = 1.6
    c: Coincident(g10,g6)
    c: Coincident(g13,g6)
    c: Coincident(g12,g7)
    c: Coincident(g11,g7)
    c: Distance(g10,g15) = 1.6
    c: Distance(g15,g13) = 1.6
    c: Distance(g4,g12) = 1.6
    c: Distance(g4,g11) = 1.6
    c: PointOnObject(g15,g2)
    c: Tangent(g3,g14) = -1.5708
    c: Tangent(g2,g14) = 1.5708
    c: PointOnObject(g17,g4)
    c: PointOnObject(g17,g3)
    c: Tangent(g4,g16) = -1.5708
    c: Tangent(g3,g16) = -1.5708
    c: Equal(g16,g14)
    c: Coincident(g16,g8)
    c: Coincident(g6,g1)
FEATURE [Part::Extrusion] Extrude007  label="Extrude fermo grilletto"
  Base = -> Sketch011
  Dir = (0,-1,2e-16)
  DirMode = 2
  FaceMakerClass = Part::FaceMakerBullseye
  FaceMakerMode = 3
  LengthFwd = 25.2
  LengthRev = 0
  Solid = true
  Symmetric = true
FEATURE [Sketcher::SketchObject] Sketch012  label="buco oled"
  ArcFitTolerance = 1e-06
  AttachmentSupport = -> [XZ_Plane]
  ExternalGeometry = -> [Sketch]
  FullyConstrained = true
  MakeInternals = false
  MapMode = 5
  Placement = pos=(0,0,0) rot=(1,0,0;1.5708rad)
  sketch-geometry (4):
    g0: LineSegment StartX=-185.747 StartY=58.0965 StartZ=0 EndX=-180.232 EndY=56.0891 EndZ=0
    g1: LineSegment StartX=-185.747 StartY=58.0965 StartZ=0 EndX=-185.747 EndY=67.3588 EndZ=0
    g2: LineSegment StartX=-185.747 StartY=67.3588 StartZ=0 EndX=-180.232 EndY=67.3588 EndZ=0
    g3: LineSegment StartX=-180.232 StartY=67.3588 StartZ=0 EndX=-180.232 EndY=56.0891 EndZ=0
  constraints (10):
    c: Coincident(g1,g0)
    c: Coincident(g2,g1)
    c: Coincident(g3,g2)
    c: Coincident(g3,g0)
    c: Parallel(g1,g-5)
    c: Perpendicular(g-3,g0)
    c: Parallel(g2,g-6)
    c: Parallel(g3,g-4)
    c: Coincident(g0,g-5)
    c: Coincident(g2,g-6)
FEATURE [Part::Extrusion] Extrude008  label="Extrude buco oled"
  Base = -> Sketch012
  Dir = (0,-1,2e-16)
  DirMode = 2
  FaceMakerClass = Part::FaceMakerBullseye
  FaceMakerMode = 3
  LengthFwd = 12.8
  LengthRev = 0
  Solid = true
  Symmetric = true
FEATURE [Sketcher::SketchObject] Sketch013  label="buco pompa"
  ArcFitTolerance = 1e-06
  AttachmentSupport = -> [XZ_Plane]
  ExternalGeometry = -> [Sketch]
  FullyConstrained = true
  MakeInternals = false
  MapMode = 5
  Placement = pos=(0,0,0) rot=(1,0,0;1.5708rad)
  sketch-geometry (8):
    g0: LineSegment StartX=-82.8 StartY=-10.4 StartZ=0 EndX=-82.8 EndY=-9.6 EndZ=0
    g1: LineSegment StartX=-82.8 StartY=-9.6 StartZ=0 EndX=-67.9 EndY=-9.6 EndZ=0
    g2: LineSegment StartX=-67.9 StartY=-9.6 StartZ=0 EndX=-67.9 EndY=6 EndZ=0
    g3: LineSegment StartX=-67.9 StartY=6 StartZ=0 EndX=-65.9 EndY=6 EndZ=0
    g4: LineSegment StartX=-65.9 StartY=6 StartZ=0 EndX=-65.9 EndY=-1.7 EndZ=0
    g5: LineSegment StartX=-65.9 StartY=-1.7 StartZ=0 EndX=-57.2 EndY=-1.7 EndZ=0
    g6: LineSegment StartX=-57.2 StartY=-1.7 StartZ=0 EndX=-57.2 EndY=-10.4 EndZ=0
    g7: LineSegment StartX=-57.2 StartY=-10.4 StartZ=0 EndX=-82.8 EndY=-10.4 EndZ=0
  constraints (22):
    c: Vertical(g0)
    c: Coincident(g1,g0)
    c: Horizontal(g1)
    c: Coincident(g2,g1)
    c: Vertical(g2)
    c: Coincident(g3,g2)
    c: Horizontal(g3)
    c: Coincident(g4,g3)
    c: Vertical(g4)
    c: Coincident(g5,g4)
    c: Horizontal(g5)
    c: Coincident(g6,g5)
    c: Vertical(g6)
    c: Coincident(g7,g6)
    c: Coincident(g7,g0)
    c: DistanceY(g0,g0) = 0.8
    c: DistanceY(g6,g6) = 8.7
    c: DistanceX(g1,g1) = 14.9
    c: DistanceX(g3,g3) = 2
    c: Coincident(g0,g-4)
    c: DistanceY(g2,g-6) = 0
    c: Coincident(g6,g-5)
FEATURE [Part::Extrusion] Extrude009  label="Extrude buco pompa"
  Base = -> Sketch013
  Dir = (0,-1,2e-16)
  DirMode = 2
  FaceMakerClass = Part::FaceMakerBullseye
  FaceMakerMode = 3
  LengthFwd = 13.2
  LengthRev = 0
  Solid = true
  Symmetric = true
FEATURE [Sketcher::SketchObject] Sketch014  label="buco frontale"
  ArcFitTolerance = 1e-06
  AttachmentSupport = -> [XZ_Plane]
  ExternalGeometry = -> [Sketch]
  FullyConstrained = true
  MakeInternals = false
  MapMode = 5
  Placement = pos=(0,0,0) rot=(1,0,0;1.5708rad)
  sketch-geometry (10):
    g0: LineSegment StartX=0 StartY=0 StartZ=0 EndX=0 EndY=24.671 EndZ=0
    g1: LineSegment StartX=0 StartY=24.671 StartZ=0 EndX=-4 EndY=24.671 EndZ=0
    g2: LineSegment StartX=-4 StartY=24.671 StartZ=0 EndX=-4 EndY=16 EndZ=0
    g3: LineSegment StartX=-4 StartY=16 StartZ=0 EndX=-2.4 EndY=16 EndZ=0
    g4: LineSegment StartX=-2.4 StartY=16 StartZ=0 EndX=-2.4 EndY=10 EndZ=0
    g5: LineSegment StartX=-2.4 StartY=10 StartZ=0 EndX=-12 EndY=10 EndZ=0
    g6: LineSegment StartX=-12 StartY=10 StartZ=0 EndX=-12 EndY=6 EndZ=0
    g7: LineSegment StartX=-12 StartY=6 StartZ=0 EndX=-2.4 EndY=6 EndZ=0
    g8: LineSegment StartX=-2.4 StartY=6 StartZ=0 EndX=-2.4 EndY=0 EndZ=0
    g9: LineSegment StartX=-2.4 StartY=0 StartZ=0 EndX=0 EndY=0 EndZ=0
  constraints (29):
    c: Vertical(g0)
    c: Coincident(g1,g0)
    c: Horizontal(g1)
    c: Coincident(g2,g1)
    c: Vertical(g2)
    c: Coincident(g3,g2)
    c: Horizontal(g3)
    c: Coincident(g4,g3)
    c: Vertical(g4)
    c: Coincident(g5,g4)
    c: Horizontal(g5)
    c: Coincident(g6,g5)
    c: Vertical(g6)
    c: Coincident(g7,g6)
    c: Coincident(g8,g7)
    c: Vertical(g8)
    c: Coincident(g9,g8)
    c: Coincident(g9,g0)
    c: Horizontal(g9)
    c: DistanceY(g0,g0) = 24.671
    c: Horizontal(g7)
    c: DistanceY(g6,g6) = 4
    c: DistanceY(g4,g4) = 6
    c: DistanceX(g9,g9) = 2.4
    c: Coincident(g0,g-1)
    c: DistanceY(g-3,g7) = 0
    c: DistanceX(g8,g4) = 0
    c: DistanceX(g-3,g1) = 0
    c: DistanceX(g6,g-3) = 8
FEATURE [Part::Extrusion] Extrude010  label="Extrude buco frontale"
  Base = -> Sketch014
  Dir = (0,-1,2e-16)
  DirMode = 2
  FaceMakerClass = Part::FaceMakerBullseye
  FaceMakerMode = 3
  LengthFwd = 11.2
  LengthRev = 0
  Solid = true
  Symmetric = true
FEATURE [Sketcher::SketchObject] Sketch015  label="guida rail"
  ArcFitTolerance = 1e-06
  AttachmentSupport = -> [XZ_Plane]
  ExternalGeometry = -> [Sketch]
  FullyConstrained = true
  MakeInternals = false
  MapMode = 5
  Placement = pos=(0,0,0) rot=(1,0,0;1.5708rad)
  sketch-geometry (4):
    g0: LineSegment StartX=-100.8 StartY=43.2 StartZ=0 EndX=-44.6 EndY=43.2 EndZ=0
    g1: LineSegment StartX=-44.6 StartY=43.2 StartZ=0 EndX=-44.6 EndY=41.2 EndZ=0
    g2: LineSegment StartX=-44.6 StartY=41.2 StartZ=0 EndX=-100.8 EndY=41.2 EndZ=0
    g3: LineSegment StartX=-100.8 StartY=41.2 StartZ=0 EndX=-100.8 EndY=43.2 EndZ=0
  constraints (9):
    c: Horizontal(g0)
    c: Coincident(g1,g0)
    c: Coincident(g2,g1)
    c: Coincident(g3,g2)
    c: Coincident(g3,g0)
    c: Vertical(g3)
    c: Coincident(g2,g-3)
    c: Coincident(g1,g-3)
    c: Coincident(g0,g-4)
FEATURE [Part::Extrusion] Extrude011  label="Extrude guida rail"
  Base = -> Sketch015
  Dir = (0,-1,2e-16)
  DirMode = 2
  FaceMakerClass = Part::FaceMakerBullseye
  FaceMakerMode = 3
  LengthFwd = 9
  LengthRev = 0
  Solid = true
  Symmetric = true
FEATURE [Sketcher::SketchObject] Sketch016  label="guide per coperture laterali"
  ArcFitTolerance = 1e-06
  AttachmentSupport = -> [XZ_Plane]
  ExternalGeometry = -> [Sketch]
  FullyConstrained = true
  MakeInternals = false
  MapMode = 5
  Placement = pos=(0,0,0) rot=(1,0,0;1.5708rad)
  sketch-geometry (14):
    g0: Circle CenterX=-5.6 CenterY=7.6 CenterZ=0 NormalX=0 NormalY=0 NormalZ=1 AngleXU=0 Radius=1.6
    g1: Circle CenterX=-5.6 CenterY=7.6 CenterZ=0 NormalX=0 NormalY=0 NormalZ=1 AngleXU=0 Radius=4
    g2: Circle CenterX=-5.6 CenterY=34.8 CenterZ=0 NormalX=0 NormalY=0 NormalZ=1 AngleXU=0 Radius=1.6
    g3: Circle CenterX=-5.6 CenterY=34.8 CenterZ=0 NormalX=0 NormalY=0 NormalZ=1 AngleXU=0 Radius=4
    g4: Circle CenterX=-184.08 CenterY=34.8 CenterZ=0 NormalX=0 NormalY=0 NormalZ=1 AngleXU=0 Radius=1.6
    g5: Circle CenterX=-184.08 CenterY=34.8 CenterZ=0 NormalX=0 NormalY=0 NormalZ=1 AngleXU=0 Radius=4
    g6: Circle CenterX=-179.305 CenterY=-76.8316 CenterZ=0 NormalX=0 NormalY=0 NormalZ=1 AngleXU=0 Radius=1.6
    g7: Circle CenterX=-179.305 CenterY=-76.8316 CenterZ=0 NormalX=0 NormalY=0 NormalZ=1 AngleXU=0 Radius=4
    g8: Circle CenterX=-213.443 CenterY=-76.8316 CenterZ=0 NormalX=0 NormalY=0 NormalZ=1 AngleXU=0 Radius=1.6
    g9: Circle CenterX=-213.443 CenterY=-76.8316 CenterZ=0 NormalX=0 NormalY=0 NormalZ=1 AngleXU=0 Radius=4
    g10: Circle CenterX=-78.51 CenterY=7.6 CenterZ=0 NormalX=0 NormalY=0 NormalZ=1 AngleXU=0 Radius=1.6
    g11: Circle CenterX=-78.51 CenterY=7.6 CenterZ=0 NormalX=0 NormalY=0 NormalZ=1 AngleXU=0 Radius=4
    g12: Circle CenterX=-78.51 CenterY=34.8 CenterZ=0 NormalX=0 NormalY=0 NormalZ=1 AngleXU=0 Radius=1.6
    g13: Circle CenterX=-78.51 CenterY=34.8 CenterZ=0 NormalX=0 NormalY=0 NormalZ=1 AngleXU=0 Radius=4
  constraints (35):
    c: Diameter(g0) = 3.2
    c: Diameter(g1) = 8
    c: Coincident(g0,g1)
    c: Diameter(g2) = 3.2
    c: Diameter(g3) = 8
    c: Coincident(g3,g2)
    c: Tangent(g2,g-7)
    c: Diameter(g4) = 3.2
    c: Diameter(g5) = 8
    c: Coincident(g5,g4)
    c: Tangent(g4,g-7)
    c: Tangent(g4,g-8)
    c: Diameter(g6) = 3.2
    c: Diameter(g7) = 8
    c: Coincident(g7,g6)
    c: Tangent(g6,g-9)
    c: Tangent(g6,g-10)
    c: Diameter(g8) = 3.2
    c: Diameter(g9) = 8
    c: Coincident(g9,g8)
    c: Tangent(g8,g-10)
    c: Tangent(g8,g-11)
    c: Diameter(g10) = 3.2
    c: Diameter(g11) = 8
    c: Diameter(g12) = 3.2
    c: Diameter(g13) = 8
    c: Coincident(g12,g13)
    c: Coincident(g10,g11)
    c: Tangent(g12,g-7)
    c: DistanceX(g12,g10) = 0
    c: Tangent(g2,g-6)
    c: Tangent(g0,g-6)
    c: Tangent(g0,g-3)
    c: Tangent(g10,g-3)
    c: Tangent(g10,g-4)
FEATURE [Part::Extrusion] Extrude012  label="extrude guide per coperture laterali"
  Base = -> Sketch016
  Dir = (0,-1,2e-16)
  DirMode = 2
  FaceMakerClass = Part::FaceMakerBullseye
  FaceMakerMode = 3
  LengthFwd = 25.2
  LengthRev = 0
  Solid = true
  Symmetric = true
FEATURE [Sketcher::SketchObject] Sketch017  label="supporto CAM"
  ArcFitTolerance = 1e-06
  AttachmentSupport = -> [XZ_Plane]
  ExternalGeometry = -> [Sketch]
  FullyConstrained = true
  MakeInternals = false
  MapMode = 5
  Placement = pos=(0,0,0) rot=(1,0,0;1.5708rad)
  sketch-geometry (6):
    g0: LineSegment StartX=-2.4 StartY=48 StartZ=0 EndX=-2.4 EndY=41.2 EndZ=0
    g1: LineSegment StartX=-2.4 StartY=48 StartZ=0 EndX=-34 EndY=48 EndZ=0
    g2: LineSegment StartX=-34 StartY=48 StartZ=0 EndX=-34 EndY=46.72 EndZ=0
    g3: LineSegment StartX=-34 StartY=46.72 StartZ=0 EndX=-36 EndY=46.72 EndZ=0
    g4: LineSegment StartX=-36 StartY=46.72 StartZ=0 EndX=-36 EndY=41.2 EndZ=0
    g5: LineSegment StartX=-36 StartY=41.2 StartZ=0 EndX=-2.4 EndY=41.2 EndZ=0
  constraints (15):
    c: Coincident(g1,g0)
    c: Horizontal(g1)
    c: Coincident(g2,g1)
    c: Vertical(g2)
    c: Coincident(g3,g2)
    c: Horizontal(g3)
    c: Coincident(g4,g3)
    c: Coincident(g5,g4)
    c: DistanceX(g1,g0) = 31.6
    c: Coincident(g5,g0)
    c: Vertical(g4)
    c: DistanceY(g2,g1) = 1.28
    c: Coincident(g0,g-3)
    c: Coincident(g0,g-3)
    c: Coincident(g4,g-4)
FEATURE [Part::Extrusion] Extrude013  label="Extrude supporto CAM"
  Base = -> Sketch017
  Dir = (0,-1,2e-16)
  DirMode = 2
  FaceMakerClass = Part::FaceMakerBullseye
  FaceMakerMode = 3
  LengthFwd = 17.8
  LengthRev = 0
  Solid = true
  Symmetric = true
FEATURE [Sketcher::SketchObject] Sketch018  label="Scavo CAM"
  ArcFitTolerance = 1e-06
  AttachmentSupport = -> [YZ_Plane]
  ExternalGeometry = -> [Sketch]
  FullyConstrained = true
  MakeInternals = false
  MapMode = 5
  Placement = pos=(0,0,0) rot=(0.57735,0.57735,0.57735;2.0944rad)
  sketch-geometry (4):
    g0: LineSegment StartX=-7.73 StartY=48 StartZ=0 EndX=7.73 EndY=48 EndZ=0
    g1: LineSegment [constr] StartX=1.07e-14 StartY=48 StartZ=0 EndX=0 EndY=43.5155 EndZ=0
    g2: ArcOfCircle CenterX=9e-15 CenterY=52.42 CenterZ=0 NormalX=0 NormalY=0 NormalZ=1 AngleXU=0 Radius=8.90445 StartAngle=3.66102 EndAngle=5.76376
    g3: Circle [constr] CenterX=9e-15 CenterY=52.42 CenterZ=0 NormalX=0 NormalY=0 NormalZ=1 AngleXU=0 Radius=8.9
  constraints (13):
    c: Horizontal(g0)
    c: DistanceY(g-3,g0) = 0
    c: DistanceX(g0,g0) = 15.46
    c: DistanceX(g0,g-3) = 7.73
    c: DistanceX(g-3) = 0
    c: Coincident(g1,g-3)
    c: PointOnObject(g1,g-2)
    c: Coincident(g2,g0)
    c: Coincident(g2,g0)
    c: PointOnObject(g1,g2)
    c: Diameter(g3) = 17.8
    c: DistanceY(g1,g3) = 4.42
    c: Coincident(g2,g3)
FEATURE [Part::Extrusion] Extrude014  label="Extrude Scavo CAM"
  Base = -> Sketch018
  Dir = (1,0,0)
  DirMode = 2
  FaceMakerClass = Part::FaceMakerBullseye
  FaceMakerMode = 3
  LengthFwd = -34
  LengthRev = 0
  Solid = true
  Symmetric = false
FEATURE [Sketcher::SketchObject] Sketch019  label="scavo rumble"
  ArcFitTolerance = 1e-06
  AttachmentSupport = -> [XZ_Plane]
  ExternalGeometry = -> [Sketch]
  FullyConstrained = true
  MakeInternals = false
  MapMode = 5
  Placement = pos=(0,0,0) rot=(1,0,0;1.5708rad)
  sketch-geometry (6):
    g0: LineSegment StartX=-164.575 StartY=-24.3786 StartZ=0 EndX=-159.439 EndY=-26.0473 EndZ=0
    g1: LineSegment StartX=-159.439 StartY=-26.0473 StartZ=0 EndX=-166.547 EndY=-47.9216 EndZ=0
    g2: LineSegment StartX=-166.547 StartY=-47.9216 StartZ=0 EndX=-171.682 EndY=-46.2529 EndZ=0
    g3: LineSegment StartX=-171.682 StartY=-46.2529 StartZ=0 EndX=-164.575 EndY=-24.3786 EndZ=0
    g4: LineSegment [constr] StartX=-145.51 StartY=22 StartZ=0 EndX=-160.961 EndY=-25.5528 EndZ=0
    g5: LineSegment [constr] StartX=-159.439 StartY=-26.0473 StartZ=0 EndX=-160.961 EndY=-25.5528 EndZ=0
  constraints (17):
    c: Coincident(g1,g0)
    c: Coincident(g2,g1)
    c: Coincident(g3,g2)
    c: Coincident(g3,g0)
    c: Parallel(g3,g-3)
    c: Parallel(g3,g1)
    c: Perpendicular(g3,g0)
    c: Perpendicular(g2,g3)
    c: Distance(g2,g0) = 23
    c: Parallel(g4,g-3)
    c: Distance(g4) = 50
    c: Coincident(g4,g-3)
    c: Parallel(g5,g0)
    c: Distance(g5) = 1.6
    c: Coincident(g5,g0)
    c: Distance(g5,g0) = 3.8
    c: Coincident(g5,g4)
FEATURE [Part::Extrusion] Extrude015  label="scavo rumble001"
  Base = -> Sketch019
  Dir = (0,-1,2e-16)
  DirMode = 2
  FaceMakerClass = Part::FaceMakerBullseye
  FaceMakerMode = 3
  LengthFwd = 21
  LengthRev = 0
  Solid = true
  Symmetric = true
FEATURE [Sketcher::SketchObject] Sketch020  label="fermo rumble"
  ArcFitTolerance = 1e-06
  AttachmentSupport = -> [XZ_Plane]
  ExternalGeometry = -> [Sketch019,Sketch]
  FullyConstrained = true
  MakeInternals = false
  MapMode = 5
  Placement = pos=(0,0,0) rot=(1,0,0;1.5708rad)
  sketch-geometry (16):
    g0: LineSegment [constr] StartX=-166.709 StartY=-43.2425 StartZ=0 EndX=-168.068 EndY=-47.4271 EndZ=0
    g1: LineSegment [constr] StartX=-168.068 StartY=-47.4271 StartZ=0 EndX=-166.547 EndY=-47.9216 EndZ=0
    g2: LineSegment StartX=-168.121 StartY=-40.4703 StartZ=0 EndX=-166.029 EndY=-41.1502 EndZ=0
    g3: LineSegment StartX=-166.029 StartY=-41.1502 StartZ=0 EndX=-166.709 EndY=-43.2425 EndZ=0
    g4: LineSegment StartX=-166.709 StartY=-43.2425 StartZ=0 EndX=-168.801 EndY=-42.5626 EndZ=0
    g5: LineSegment StartX=-168.801 StartY=-42.5626 StartZ=0 EndX=-168.121 EndY=-40.4703 EndZ=0
    g6: LineSegment StartX=-167.627 StartY=-38.9486 StartZ=0 EndX=-164.203 EndY=-40.0611 EndZ=0
    g7: LineSegment StartX=-164.203 StartY=-40.0611 StartZ=0 EndX=-165.81 EndY=-45.0066 EndZ=0
    g8: LineSegment StartX=-165.81 StartY=-45.0066 StartZ=0 EndX=-169.234 EndY=-43.8941 EndZ=0
    g9: LineSegment StartX=-170.261 StartY=-41.878 StartZ=0 EndX=-169.643 EndY=-39.9759 EndZ=0
    g10: LineSegment [constr] StartX=-169.643 StartY=-39.9759 StartZ=0 EndX=-169.148 EndY=-38.4542 EndZ=0
    g11: LineSegment [constr] StartX=-169.148 StartY=-38.4542 StartZ=0 EndX=-167.627 EndY=-38.9486 EndZ=0
    g12: ArcOfCircle CenterX=-168.739 CenterY=-42.3724 CenterZ=0 NormalX=0 NormalY=0 NormalZ=1 AngleXU=0 Radius=1.6 StartAngle=2.82743 EndAngle=4.39823
    g13: GeomPoint [constr] X=-170.755 Y=-43.3997 Z=0
    g14: ArcOfCircle CenterX=-168.121 CenterY=-40.4703 CenterZ=0 NormalX=0 NormalY=0 NormalZ=1 AngleXU=0 Radius=1.6 StartAngle=1.25664 EndAngle=2.82743
    g15: GeomPoint [constr] X=-169.148 Y=-38.4542 Z=0
  constraints (42):
    c: Parallel(g0,g-4)
    c: Distance(g0) = 4.4
    c: Coincident(g1,g0)
    c: Perpendicular(g0,g1)
    c: Distance(g1) = 1.6
    c: Coincident(g1,g-5)
    c: Coincident(g3,g2)
    c: Coincident(g4,g3)
    c: Coincident(g5,g4)
    c: Coincident(g5,g2)
    c: Parallel(g3,g-4)
    c: Parallel(g3,g5)
    c: Perpendicular(g2,g3)
    c: Parallel(g4,g2)
    c: Distance(g2) = 2.2
    c: Distance(g3) = 2.2
    c: Coincident(g7,g6)
    c: Coincident(g8,g7)
    c: Parallel(g7,g-4)
    c: Parallel(g7,g9)
    c: Perpendicular(g6,g7)
    c: Parallel(g6,g8)
    c: Distance(g6,g15) = 5.2
    c: Distance(g7) = 5.2
    c: Coincident(g11,g10)
    c: Parallel(g10,g9)
    c: Parallel(g11,g6)
    c: Distance(g10) = 1.6
    c: Distance(g11) = 1.6
    c: Coincident(g10,g15)
    c: Distance(g11,g2) = 1.6
    c: Distance(g2,g10) = 1.6
    c: PointOnObject(g13,g8)
    c: PointOnObject(g13,g9)
    c: Tangent(g8,g12) = 1.5708
    c: Tangent(g9,g12) = 1.5708
    c: PointOnObject(g15,g9)
    c: Tangent(g6,g14) = 1.5708
    c: Tangent(g9,g14) = 1.5708
    c: Equal(g12,g14)
    c: Coincident(g6,g11)
    c: Coincident(g3,g0)
FEATURE [Part::Extrusion] Extrude016  label="Extrude fermo rumble"
  Base = -> Sketch020
  Dir = (0,-1,2e-16)
  DirMode = 2
  FaceMakerClass = Part::FaceMakerBullseye
  FaceMakerMode = 3
  LengthFwd = 25.2
  LengthRev = 0
  Solid = true
  Symmetric = true
FEATURE [Sketcher::SketchObject] Sketch021  label="perno fermo rumble001"
  ArcFitTolerance = 1e-06
  AttachmentSupport = -> [XZ_Plane001]
  FullyConstrained = true
  MakeInternals = false
  MapMode = 5
  Placement = pos=(0,0,0) rot=(1,0,0;1.5708rad)
  sketch-geometry (16):
    g0: LineSegment StartX=0 StartY=0.45 StartZ=0 EndX=0 EndY=1.55 EndZ=0
    g1: LineSegment StartX=0.45 StartY=2 StartZ=0 EndX=1.55 EndY=2 EndZ=0
    g2: LineSegment StartX=2 StartY=1.55 StartZ=0 EndX=2 EndY=0.45 EndZ=0
    g3: LineSegment StartX=1.55 StartY=0 StartZ=0 EndX=0.45 EndY=0 EndZ=0
    g4: ArcOfCircle [constr] CenterX=0.45 CenterY=1.55 CenterZ=0 NormalX=0 NormalY=0 NormalZ=1 AngleXU=0 Radius=0.45 StartAngle=1.5708 EndAngle=3.14159
    g5: GeomPoint [constr] X=0 Y=2 Z=0
    g6: LineSegment StartX=0.45 StartY=2 StartZ=0 EndX=0 EndY=1.55 EndZ=0
    g7: ArcOfCircle [constr] CenterX=1.55 CenterY=1.55 CenterZ=0 NormalX=0 NormalY=0 NormalZ=1 AngleXU=0 Radius=0.45 StartAngle=0 EndAngle=1.5708
    g8: GeomPoint [constr] X=2 Y=2 Z=0
    g9: LineSegment StartX=2 StartY=1.55 StartZ=0 EndX=1.55 EndY=2 EndZ=0
    g10: ArcOfCircle [constr] CenterX=1.55 CenterY=0.45 CenterZ=0 NormalX=0 NormalY=0 NormalZ=1 AngleXU=0 Radius=0.45 StartAngle=4.71239 EndAngle=6.28319
    g11: GeomPoint [constr] X=2 Y=0 Z=0
    g12: LineSegment StartX=1.55 StartY=0 StartZ=0 EndX=2 EndY=0.45 EndZ=0
    g13: ArcOfCircle [constr] CenterX=0.45 CenterY=0.45 CenterZ=0 NormalX=0 NormalY=0 NormalZ=1 AngleXU=0 Radius=0.45 StartAngle=3.14159 EndAngle=4.71239
    g14: GeomPoint [constr] X=0 Y=0 Z=0
    g15: LineSegment StartX=0 StartY=0.45 StartZ=0 EndX=0.45 EndY=0 EndZ=0
  constraints (35):
    c: Coincident(g14,g-1)
    c: PointOnObject(g5,g-2)
    c: Horizontal(g1)
    c: Vertical(g2)
    c: Horizontal(g3)
    c: DistanceX(g5,g8) = 2
    c: DistanceY(g11,g8) = 2
    c: PointOnObject(g5,g0)
    c: PointOnObject(g5,g1)
    c: Tangent(g0,g4) = 1.5708
    c: Tangent(g1,g4) = 1.5708
    c: Coincident(g6,g0)
    c: Coincident(g6,g1)
    c: PointOnObject(g8,g2)
    c: PointOnObject(g8,g1)
    c: Tangent(g2,g7) = 1.5708
    c: Tangent(g1,g7) = 1.5708
    c: Coincident(g9,g2)
    c: Coincident(g9,g1)
    c: PointOnObject(g11,g2)
    c: PointOnObject(g11,g3)
    c: Tangent(g2,g10) = 1.5708
    c: Tangent(g3,g10) = 1.5708
    c: Coincident(g12,g2)
    c: Coincident(g12,g3)
    c: PointOnObject(g14,g0)
    c: PointOnObject(g14,g3)
    c: Tangent(g0,g13) = 1.5708
    c: Tangent(g3,g13) = 1.5708
    c: Coincident(g15,g0)
    c: Coincident(g15,g3)
    c: Equal(g6,g9)
    c: Equal(g9,g12)
    c: Equal(g12,g15)
    c: DistanceX(g14,g3) = 0.45
FEATURE [Part::Extrusion] Extrude017  label="Extrude perno fermo rumble"
  Base = -> Sketch021
  Dir = (0,-1,2e-16)
  DirMode = 2
  FaceMakerClass = Part::FaceMakerBullseye
  FaceMakerMode = 3
  LengthFwd = 25.2
  LengthRev = 0
  Solid = true
  Symmetric = true
FEATURE [Sketcher::SketchObject] Sketch022  label="fori per M3x5(OD)x6(L)"
  ArcFitTolerance = 1e-06
  AttachmentSupport = -> [XZ_Plane]
  ExternalGeometry = -> [Sketch016]
  FullyConstrained = true
  MakeInternals = false
  MapMode = 5
  Placement = pos=(0,0,0) rot=(1,0,0;1.5708rad)
  sketch-geometry (7):
    g0: Circle CenterX=-5.6 CenterY=34.8 CenterZ=0 NormalX=0 NormalY=0 NormalZ=1 AngleXU=0 Radius=2.5
    g1: Circle CenterX=-5.6 CenterY=7.6 CenterZ=0 NormalX=0 NormalY=0 NormalZ=1 AngleXU=0 Radius=2.5
    g2: Circle CenterX=-78.51 CenterY=34.8 CenterZ=0 NormalX=0 NormalY=0 NormalZ=1 AngleXU=0 Radius=2.5
    g3: Circle CenterX=-78.51 CenterY=7.6 CenterZ=0 NormalX=0 NormalY=0 NormalZ=1 AngleXU=0 Radius=2.5
    g4: Circle CenterX=-184.08 CenterY=34.8 CenterZ=0 NormalX=0 NormalY=0 NormalZ=1 AngleXU=0 Radius=2.5
    g5: Circle CenterX=-179.305 CenterY=-76.8316 CenterZ=0 NormalX=0 NormalY=0 NormalZ=1 AngleXU=0 Radius=2.5
    g6: Circle CenterX=-213.443 CenterY=-76.8316 CenterZ=0 NormalX=0 NormalY=0 NormalZ=1 AngleXU=0 Radius=2.5
  constraints (14):
    c: Diameter(g0) = 5
    c: Diameter(g1) = 5
    c: Diameter(g2) = 5
    c: Diameter(g3) = 5
    c: Diameter(g4) = 5
    c: Diameter(g5) = 5
    c: Diameter(g6) = 5
    c: Coincident(g0,g-8)
    c: Coincident(g1,g-9)
    c: Coincident(g2,g-6)
    c: Coincident(g3,g-7)
    c: Coincident(g4,g-5)
    c: Coincident(g5,g-4)
    c: Coincident(g6,g-3)
FEATURE [Part::Extrusion] Extrude018  label="Extrude fori M3x5x6 - dx"
  Base = -> Sketch022
  Dir = (0,-1,2e-16)
  DirMode = 2
  FaceMakerClass = Part::FaceMakerBullseye
  FaceMakerMode = 3
  LengthFwd = 6.2
  LengthRev = 0
  Placement = pos=(0,-9.5,0) rot=(0,0,1;0rad)
  Solid = true
  Symmetric = true
FEATURE [Part::Extrusion] Extrude019  label="Extrude fori M3x5x6 - sx"
  Base = -> Sketch022
  Dir = (0,-1,2e-16)
  DirMode = 2
  FaceMakerClass = Part::FaceMakerBullseye
  FaceMakerMode = 3
  LengthFwd = 6.2
  LengthRev = 0
  Placement = pos=(0,9.5,0) rot=(0,0,1;0rad)
  Solid = true
  Symmetric = true
FEATURE [Sketcher::SketchObject] Sketch023  label="foro anteriore M3x5x6"
  ArcFitTolerance = 1e-06
  AttachmentSupport = -> [YZ_Plane]
  FullyConstrained = true
  MakeInternals = false
  MapMode = 5
  Placement = pos=(0,0,0) rot=(0.57735,0.57735,0.57735;2.0944rad)
  sketch-geometry (2):
    g0: LineSegment [constr] StartX=0 StartY=0 StartZ=0 EndX=0 EndY=38.6 EndZ=0
    g1: Circle CenterX=0 CenterY=38.6 CenterZ=0 NormalX=0 NormalY=0 NormalZ=1 AngleXU=0 Radius=2.5
  constraints (5):
    c: Coincident(g0,g-1)
    c: PointOnObject(g0,g-2)
    c: DistanceY(g0,g0) = 38.6
    c: Diameter(g1) = 5
    c: Coincident(g1,g0)
FEATURE [Part::Extrusion] Extrude020  label="Extrude foro anteriore M3x5x6"
  Base = -> Sketch023
  Dir = (1,0,0)
  DirMode = 2
  FaceMakerClass = Part::FaceMakerBullseye
  FaceMakerMode = 3
  LengthFwd = -6.2
  LengthRev = 0
  Solid = true
  Symmetric = false
FEATURE [Sketcher::SketchObject] Sketch024  label="fori per viti frontale"
  ArcFitTolerance = 1e-06
  AttachmentSupport = -> [YZ_Plane]
  FullyConstrained = true
  MakeInternals = false
  MapMode = 5
  Placement = pos=(0,0,0) rot=(0.57735,0.57735,0.57735;2.0944rad)
  sketch-geometry (9):
    g0: LineSegment [constr] StartX=-10.3 StartY=30.721 StartZ=0 EndX=10.3 EndY=30.721 EndZ=0
    g1: LineSegment [constr] StartX=10.3 StartY=30.721 StartZ=0 EndX=10.3 EndY=10.121 EndZ=0
    g2: LineSegment [constr] StartX=10.3 StartY=10.121 StartZ=0 EndX=-10.3 EndY=10.121 EndZ=0
    g3: LineSegment [constr] StartX=-10.3 StartY=10.121 StartZ=0 EndX=-10.3 EndY=30.721 EndZ=0
    g4: LineSegment [constr] StartX=0 StartY=0 StartZ=0 EndX=0 EndY=10.121 EndZ=0
    g5: Circle CenterX=-10.3 CenterY=30.721 CenterZ=0 NormalX=0 NormalY=0 NormalZ=1 AngleXU=0 Radius=2
    g6: Circle CenterX=10.3 CenterY=30.721 CenterZ=0 NormalX=0 NormalY=0 NormalZ=1 AngleXU=0 Radius=2
    g7: Circle CenterX=-10.3 CenterY=10.121 CenterZ=0 NormalX=0 NormalY=0 NormalZ=1 AngleXU=0 Radius=2
    g8: Circle CenterX=10.3 CenterY=10.121 CenterZ=0 NormalX=0 NormalY=0 NormalZ=1 AngleXU=0 Radius=2
  constraints (22):
    c: Horizontal(g0)
    c: Coincident(g1,g0)
    c: Vertical(g1)
    c: Coincident(g2,g1)
    c: Horizontal(g2)
    c: Coincident(g3,g2)
    c: Coincident(g3,g0)
    c: Vertical(g3)
    c: DistanceX(g0,g0) = 20.6
    c: DistanceY(g3,g3) = 20.6
    c: Coincident(g4,g-1)
    c: PointOnObject(g4,g-2)
    c: DistanceY(g4,g4) = 10.121
    c: Symmetric(g2,g2,g4)
    c: Diameter(g5) = 4
    c: Diameter(g6) = 4
    c: Diameter(g7) = 4
    c: Diameter(g8) = 4
    c: Coincident(g5,g0)
    c: Coincident(g6,g0)
    c: Coincident(g7,g2)
    c: Coincident(g8,g1)
FEATURE [Part::Extrusion] Extrude021  label="Extrude fori per viti frontale"
  Base = -> Sketch024
  Dir = (1,0,0)
  DirMode = 2
  FaceMakerClass = Part::FaceMakerBullseye
  FaceMakerMode = 3
  LengthFwd = -2.4
  LengthRev = 0
  Solid = true
  Symmetric = false
FEATURE [Sketcher::SketchObject] Sketch025  label="foro per filo CAM"
  ArcFitTolerance = 1e-06
  AttachmentSupport = -> [XZ_Plane]
  ExternalGeometry = -> [Sketch]
  FullyConstrained = true
  MakeInternals = false
  MapMode = 5
  Placement = pos=(0,0,0) rot=(1,0,0;1.5708rad)
  sketch-geometry (4):
    g0: LineSegment StartX=-44.6 StartY=41.2 StartZ=0 EndX=-44.6 EndY=36.4 EndZ=0
    g1: LineSegment StartX=-44.6 StartY=36.4 StartZ=0 EndX=-54.6 EndY=36.4 EndZ=0
    g2: LineSegment StartX=-54.6 StartY=36.4 StartZ=0 EndX=-50.4 EndY=41.2 EndZ=0
    g3: LineSegment StartX=-50.4 StartY=41.2 StartZ=0 EndX=-44.6 EndY=41.2 EndZ=0
  constraints (11):
    c: Vertical(g0)
    c: Coincident(g1,g0)
    c: Horizontal(g1)
    c: Coincident(g2,g1)
    c: Coincident(g3,g2)
    c: Coincident(g3,g0)
    c: Horizontal(g3)
    c: Coincident(g0,g-3)
    c: DistanceY(g0,g-4) = 0
    c: DistanceX(g3,g3) = 5.8
    c: DistanceX(g1,g1) = 10
FEATURE [Part::Extrusion] Extrude022  label="Extrude foro per filo CAM dx"
  Base = -> Sketch025
  Dir = (0,-1,2e-16)
  DirMode = 2
  FaceMakerClass = Part::FaceMakerBullseye
  FaceMakerMode = 3
  LengthFwd = 4.9
  LengthRev = 0
  Placement = pos=(0,6.95,0) rot=(0,0,1;0rad)
  Solid = true
  Symmetric = true
FEATURE [Part::Extrusion] Extrude023  label="Extrude foro per filo CAM sx"
  Base = -> Sketch025
  Dir = (0,-1,2e-16)
  DirMode = 2
  FaceMakerClass = Part::FaceMakerBullseye
  FaceMakerMode = 3
  LengthFwd = 4.9
  LengthRev = 0
  Placement = pos=(0,-6.95,0) rot=(0,0,1;0rad)
  Solid = true
  Symmetric = true
FEATURE [Sketcher::SketchObject] Sketch026  label="foro sotto anteriore M3x5x6"
  ArcFitTolerance = 1e-06
  AttachmentSupport = -> [XY_Plane]
  FullyConstrained = true
  MakeInternals = false
  MapMode = 5
  sketch-geometry (2):
    g0: LineSegment [constr] StartX=0 StartY=0 StartZ=0 EndX=-16.5 EndY=0 EndZ=0
    g1: Circle CenterX=-16.5 CenterY=0 CenterZ=0 NormalX=0 NormalY=0 NormalZ=1 AngleXU=0 Radius=2.5
  constraints (5):
    c: Distance(g0) = 16.5
    c: Coincident(g0,g-1)
    c: PointOnObject(g0,g-1)
    c: Diameter(g1) = 5
    c: Coincident(g0,g1)
FEATURE [Sketcher::SketchObject] Sketch027  label="foro sotto posteriore M3x5x6"
  ArcFitTolerance = 1e-06
  AttachmentSupport = -> [XY_Plane]
  ExternalGeometry = -> [Sketch]
  FullyConstrained = true
  MakeInternals = false
  MapMode = 5
  sketch-geometry (2):
    g0: LineSegment [constr] StartX=-82.8 StartY=2e-16 StartZ=0 EndX=-71.3 EndY=2e-16 EndZ=0
    g1: Circle CenterX=-71.3 CenterY=2e-16 CenterZ=0 NormalX=0 NormalY=0 NormalZ=1 AngleXU=0 Radius=2.5
  constraints (5):
    c: Distance(g0) = 11.5
    c: Coincident(g0,g-3)
    c: PointOnObject(g0,g-3)
    c: Diameter(g1) = 5
    c: Coincident(g1,g0)
FEATURE [Sketcher::SketchObject] Sketch029  label="fori sotto impugnatura"
  ArcFitTolerance = 1e-06
  AttachmentSupport = -> [XY_Plane]
  ExternalGeometry = -> [Sketch]
  FullyConstrained = true
  MakeInternals = false
  MapMode = 5
  sketch-geometry (15):
    g0: LineSegment [constr] StartX=-175.232 StartY=-1.83e-14 StartZ=0 EndX=-191.232 EndY=0 EndZ=0
    g1: Circle CenterX=-191.232 CenterY=0 CenterZ=0 NormalX=0 NormalY=0 NormalZ=1 AngleXU=0 Radius=3.95
    g2: LineSegment [constr] StartX=-175.232 StartY=-1.83e-14 StartZ=0 EndX=-204.275 EndY=0 EndZ=0
    g3: LineSegment StartX=-204.275 StartY=3.525 StartZ=0 EndX=-204.275 EndY=-3.525 EndZ=0
    g4: LineSegment StartX=-205.4 StartY=-4.65 StartZ=0 EndX=-206.65 EndY=-4.65 EndZ=0
    g5: LineSegment StartX=-207.775 StartY=-3.525 StartZ=0 EndX=-207.775 EndY=3.525 EndZ=0
    g6: LineSegment StartX=-206.65 StartY=4.65 StartZ=0 EndX=-205.4 EndY=4.65 EndZ=0
    g7: ArcOfCircle CenterX=-206.65 CenterY=3.525 CenterZ=0 NormalX=0 NormalY=0 NormalZ=1 AngleXU=0 Radius=1.125 StartAngle=1.5708 EndAngle=3.14159
    g8: GeomPoint [constr] X=-207.775 Y=4.65 Z=0
    g9: ArcOfCircle CenterX=-205.4 CenterY=3.525 CenterZ=0 NormalX=0 NormalY=0 NormalZ=1 AngleXU=0 Radius=1.125 StartAngle=0 EndAngle=1.5708
    g10: GeomPoint [constr] X=-204.275 Y=4.65 Z=0
    g11: ArcOfCircle CenterX=-205.4 CenterY=-3.525 CenterZ=0 NormalX=0 NormalY=0 NormalZ=1 AngleXU=0 Radius=1.125 StartAngle=4.71239 EndAngle=6.28319
    g12: GeomPoint [constr] X=-204.275 Y=-4.65 Z=0
    g13: ArcOfCircle CenterX=-206.65 CenterY=-3.525 CenterZ=0 NormalX=0 NormalY=0 NormalZ=1 AngleXU=0 Radius=1.125 StartAngle=3.14159 EndAngle=4.71239
    g14: GeomPoint [constr] X=-207.775 Y=-4.65 Z=0
  constraints (35):
    c: Distance(g0) = 16
    c: Coincident(g0,g-3)
    c: PointOnObject(g0,g-1)
    c: Diameter(g1) = 7.9
    c: Coincident(g1,g0)
    c: Coincident(g2,g0)
    c: PointOnObject(g2,g-1)
    c: Vertical(g3)
    c: Horizontal(g4)
    c: Vertical(g5)
    c: Horizontal(g6)
    c: DistanceY(g12,g10) = 9.3
    c: DistanceX(g8,g10) = 3.5
    c: Symmetric(g10,g12,g2)
    c: PointOnObject(g8,g5)
    c: PointOnObject(g8,g6)
    c: Tangent(g5,g7) = 1.5708
    c: Tangent(g6,g7) = 1.5708
    c: PointOnObject(g10,g3)
    c: PointOnObject(g10,g6)
    c: Tangent(g3,g9) = 1.5708
    c: Tangent(g6,g9) = 1.5708
    c: PointOnObject(g12,g3)
    c: PointOnObject(g12,g4)
    c: Tangent(g3,g11) = 1.5708
    c: Tangent(g4,g11) = 1.5708
    c: PointOnObject(g14,g4)
    c: PointOnObject(g14,g5)
    c: Tangent(g4,g13) = 1.5708
    c: Tangent(g5,g13) = 1.5708
    c: Equal(g7,g9)
    c: Equal(g9,g11)
    c: Equal(g11,g13)
    c: DistanceX(g6,g6) = 1.25
    c: DistanceX(g-5,g5) = 6.8
FEATURE [Sketcher::SketchObject] Sketch030  label="fori superiori per solenoide e oled"
  ArcFitTolerance = 1e-06
  AttachmentSupport = -> [XY_Plane]
  ExternalGeometry = -> [Sketch]
  FullyConstrained = true
  MakeInternals = false
  MapMode = 5
  sketch-geometry (33):
    g0: LineSegment [constr] StartX=-181.6 StartY=1.12e-14 StartZ=0 EndX=-169.91 EndY=0 EndZ=0
    g1: LineSegment [constr] StartX=-169.91 StartY=0 StartZ=0 EndX=-169.91 EndY=-2.6 EndZ=0
    g2: LineSegment [constr] StartX=-169.91 StartY=0 StartZ=0 EndX=-169.91 EndY=2.6 EndZ=0
    g3: LineSegment StartX=-169.91 StartY=4.975 StartZ=0 EndX=-169.91 EndY=8.225 EndZ=0
    g4: LineSegment StartX=-167.535 StartY=10.6 StartZ=0 EndX=-167.285 EndY=10.6 EndZ=0
    g5: LineSegment StartX=-164.91 StartY=8.225 StartZ=0 EndX=-164.91 EndY=4.975 EndZ=0
    g6: LineSegment StartX=-167.285 StartY=2.6 StartZ=0 EndX=-167.535 EndY=2.6 EndZ=0
    g7: LineSegment StartX=-169.91 StartY=-4.975 StartZ=0 EndX=-169.91 EndY=-8.225 EndZ=0
    g8: LineSegment StartX=-167.535 StartY=-10.6 StartZ=0 EndX=-167.285 EndY=-10.6 EndZ=0
    g9: LineSegment StartX=-164.91 StartY=-8.225 StartZ=0 EndX=-164.91 EndY=-4.975 EndZ=0
    g10: LineSegment StartX=-167.285 StartY=-2.6 StartZ=0 EndX=-167.535 EndY=-2.6 EndZ=0
    g11: ArcOfCircle CenterX=-167.535 CenterY=8.225 CenterZ=0 NormalX=0 NormalY=0 NormalZ=1 AngleXU=0 Radius=2.375 StartAngle=1.5708 EndAngle=3.14159
    g12: GeomPoint [constr] X=-169.91 Y=10.6 Z=0
    g13: ArcOfCircle CenterX=-167.285 CenterY=8.225 CenterZ=0 NormalX=0 NormalY=0 NormalZ=1 AngleXU=0 Radius=2.375 StartAngle=0 EndAngle=1.5708
    g14: GeomPoint [constr] X=-164.91 Y=10.6 Z=0
    g15: ArcOfCircle CenterX=-167.285 CenterY=4.975 CenterZ=0 NormalX=0 NormalY=0 NormalZ=1 AngleXU=0 Radius=2.375 StartAngle=4.71239 EndAngle=6.28319
    g16: GeomPoint [constr] X=-164.91 Y=2.6 Z=0
    g17: ArcOfCircle CenterX=-167.535 CenterY=4.975 CenterZ=0 NormalX=0 NormalY=0 NormalZ=1 AngleXU=0 Radius=2.375 StartAngle=3.14159 EndAngle=4.71239
    g18: GeomPoint [constr] X=-169.91 Y=2.6 Z=0
    g19: ArcOfCircle CenterX=-167.535 CenterY=-4.975 CenterZ=0 NormalX=0 NormalY=0 NormalZ=1 AngleXU=0 Radius=2.375 StartAngle=1.5708 EndAngle=3.14159
    g20: GeomPoint [constr] X=-169.91 Y=-2.6 Z=0
    g21: ArcOfCircle CenterX=-167.285 CenterY=-4.975 CenterZ=0 NormalX=0 NormalY=0 NormalZ=1 AngleXU=0 Radius=2.375 StartAngle=0 EndAngle=1.5708
    g22: GeomPoint [constr] X=-164.91 Y=-2.6 Z=0
    g23: ArcOfCircle CenterX=-167.285 CenterY=-8.225 CenterZ=0 NormalX=0 NormalY=0 NormalZ=1 AngleXU=0 Radius=2.375 StartAngle=4.71239 EndAngle=6.28319
    g24: GeomPoint [constr] X=-164.91 Y=-10.6 Z=0
    g25: ArcOfCircle CenterX=-167.535 CenterY=-8.225 CenterZ=0 NormalX=0 NormalY=0 NormalZ=1 AngleXU=0 Radius=2.375 StartAngle=3.14159 EndAngle=4.71239
    g26: GeomPoint [constr] X=-169.91 Y=-10.6 Z=0
    g27: LineSegment [constr] StartX=-181.6 StartY=1.12e-14 StartZ=0 EndX=-152.209 EndY=0 EndZ=0
    g28: LineSegment [constr] StartX=-181.6 StartY=1.12e-14 StartZ=0 EndX=-130.41 EndY=0 EndZ=0
    g29: LineSegment [constr] StartX=-152.209 StartY=0 StartZ=0 EndX=-152.209 EndY=6.95 EndZ=0
    g30: LineSegment [constr] StartX=-130.41 StartY=0 StartZ=0 EndX=-130.41 EndY=-6.95 EndZ=0
    g31: Circle CenterX=-152.209 CenterY=6.95 CenterZ=0 NormalX=0 NormalY=0 NormalZ=1 AngleXU=0 Radius=2.1
    g32: Circle CenterX=-130.41 CenterY=-6.95 CenterZ=0 NormalX=0 NormalY=0 NormalZ=1 AngleXU=0 Radius=2.1
  constraints (79):
    c: Distance(g0) = 11.69
    c: PointOnObject(g0,g-1)
    c: Coincident(g-4,g0)
    c: Distance(g1) = 2.6
    c: Coincident(g1,g0)
    c: Vertical(g1)
    c: Distance(g2) = 2.6
    c: Coincident(g2,g0)
    c: Vertical(g2)
    c: Distance(g18,g12) = 8
    c: Coincident(g18,g2)
    c: Vertical(g3)
    c: Distance(g14,g12) = 5
    c: Horizontal(g4)
    c: Distance(g16,g14) = 8
    c: Vertical(g5)
    c: Distance(g26,g20) = 8
    c: Coincident(g20,g1)
    c: Vertical(g7)
    c: Distance(g26,g24) = 5
    c: Horizontal(g8)
    c: Distance(g24,g22) = 8
    c: Vertical(g9)
    c: PointOnObject(g12,g3)
    c: PointOnObject(g12,g4)
    c: Tangent(g3,g11) = 1.5708
    c: Tangent(g4,g11) = 1.5708
    c: PointOnObject(g14,g5)
    c: PointOnObject(g14,g4)
    c: Tangent(g5,g13) = 1.5708
    c: Tangent(g4,g13) = 1.5708
    c: PointOnObject(g16,g5)
    c: PointOnObject(g16,g6)
    c: Tangent(g5,g15) = 1.5708
    c: Tangent(g6,g15) = 1.5708
    c: PointOnObject(g18,g3)
    c: PointOnObject(g18,g6)
    c: Tangent(g3,g17) = 1.5708
    c: Tangent(g6,g17) = 1.5708
    c: Equal(g11,g13)
    c: Equal(g13,g15)
    c: Equal(g15,g17)
    c: DistanceX(g4,g4) = 0.25
    c: PointOnObject(g20,g7)
    c: PointOnObject(g20,g10)
    c: Tangent(g7,g19) = -1.5708
    c: Tangent(g10,g19) = -1.5708
    c: PointOnObject(g22,g9)
    c: PointOnObject(g22,g10)
    c: Tangent(g9,g21) = -1.5708
    c: Tangent(g10,g21) = -1.5708
    c: PointOnObject(g24,g9)
    c: PointOnObject(g24,g8)
    c: Tangent(g9,g23) = -1.5708
    c: Tangent(g8,g23) = -1.5708
    c: PointOnObject(g26,g8)
    c: PointOnObject(g26,g7)
    c: Tangent(g8,g25) = -1.5708
    c: Tangent(g7,g25) = -1.5708
    c: Equal(g19,g21)
    c: Equal(g21,g23)
    c: Equal(g23,g25)
    c: DistanceX(g10,g10) = 0.25
    c: Distance(g27) = 29.391
    c: Coincident(g27,g0)
    c: PointOnObject(g27,g-1)
    c: Distance(g28) = 51.19
    c: Coincident(g28,g0)
    c: PointOnObject(g28,g-1)
    c: Distance(g29) = 6.95
    c: Coincident(g29,g27)
    c: Vertical(g29)
    c: Distance(g30) = 6.95
    c: Coincident(g30,g28)
    c: Vertical(g30)
    c: Diameter(g31) = 4.2
    c: Diameter(g32) = 4.2
    c: Coincident(g32,g30)
    c: Coincident(g31,g29)
FEATURE [Sketcher::SketchObject] Sketch031  label="fori inferiori switch pompa"
  ArcFitTolerance = 1e-06
  AttachmentSupport = -> [XY_Plane]
  ExternalGeometry = -> [Sketch]
  FullyConstrained = true
  MakeInternals = false
  MapMode = 5
  sketch-geometry (4):
    g0: LineSegment [constr] StartX=-57.2 StartY=1.9e-15 StartZ=0 EndX=-62.45 EndY=1.9e-15 EndZ=0
    g1: LineSegment [constr] StartX=-62.45 StartY=3.25 StartZ=0 EndX=-62.45 EndY=-3.25 EndZ=0
    g2: Circle CenterX=-62.45 CenterY=3.25 CenterZ=0 NormalX=0 NormalY=0 NormalZ=1 AngleXU=0 Radius=1.6
    g3: Circle CenterX=-62.45 CenterY=-3.25 CenterZ=0 NormalX=0 NormalY=0 NormalZ=1 AngleXU=0 Radius=1.6
  constraints (10):
    c: Distance(g0) = 5.25
    c: Coincident(g0,g-3)
    c: PointOnObject(g0,g-3)
    c: Vertical(g1)
    c: DistanceY(g1,g1) = 6.5
    c: Symmetric(g1,g1,g0)
    c: Diameter(g2) = 3.2
    c: Diameter(g3) = 3.2
    c: Coincident(g2,g1)
    c: Coincident(g3,g1)
FEATURE [Sketcher::SketchObject] Sketch032  label="spazio per PILA 18650"
  ArcFitTolerance = 1e-06
  AttachmentSupport = -> [XY_Plane]
  ExternalGeometry = -> [Sketch]
  FullyConstrained = true
  MakeInternals = false
  MapMode = 5
  sketch-geometry (2):
    g0: LineSegment [constr] StartX=-178.142 StartY=-1.74e-14 StartZ=0 EndX=-190.142 EndY=-1.83e-14 EndZ=0
    g1: Circle CenterX=-190.142 CenterY=-1.83e-14 CenterZ=0 NormalX=0 NormalY=0 NormalZ=1 AngleXU=0 Radius=9.25
  constraints (5):
    c: Distance(g0) = 12
    c: Coincident(g0,g-3)
    c: PointOnObject(g0,g-4)
    c: Diameter(g1) = 18.5
    c: Coincident(g1,g0)
FEATURE [Part::Extrusion] Extrude030  label="Extrude spazio per PILA 18650"
  Base = -> Sketch032
  Dir = (0,0,1)
  DirLink = -> Sketch [Edge45]
  DirMode = 2
  FaceMakerClass = Part::FaceMakerBullseye
  FaceMakerMode = 3
  LengthFwd = 68
  LengthRev = 0
  Placement = pos=(6,0,-72.7) rot=(0,0,1;0rad)
  Solid = true
  Symmetric = false
FEATURE [Sketcher::SketchObject] Sketch033  label="fermo per scheda micro"
  ArcFitTolerance = 1e-06
  AttachmentSupport = -> [XZ_Plane]
  ExternalGeometry = -> [Sketch]
  FullyConstrained = true
  MakeInternals = false
  MapMode = 5
  Placement = pos=(0,0,0) rot=(1,0,0;1.5708rad)
  sketch-geometry (12):
    g0: LineSegment StartX=-11.6 StartY=6 StartZ=0 EndX=-4 EndY=6 EndZ=0
    g1: LineSegment StartX=-4 StartY=6 StartZ=0 EndX=-4 EndY=36.4 EndZ=0
    g2: LineSegment StartX=-4 StartY=36.4 StartZ=0 EndX=-11.6 EndY=36.4 EndZ=0
    g3: LineSegment StartX=-11.6 StartY=36.4 StartZ=0 EndX=-11.6 EndY=6 EndZ=0
    g4: LineSegment StartX=-80.11 StartY=11.6 StartZ=0 EndX=-70.51 EndY=11.6 EndZ=0
    g5: LineSegment StartX=-70.51 StartY=11.6 StartZ=0 EndX=-70.51 EndY=6 EndZ=0
    g6: LineSegment StartX=-70.51 StartY=6 StartZ=0 EndX=-80.11 EndY=6 EndZ=0
    g7: LineSegment StartX=-80.11 StartY=6 StartZ=0 EndX=-80.11 EndY=11.6 EndZ=0
    g8: LineSegment StartX=-78.51 StartY=36.4 StartZ=0 EndX=-70.51 EndY=36.4 EndZ=0
    g9: LineSegment StartX=-70.51 StartY=36.4 StartZ=0 EndX=-70.51 EndY=30.8 EndZ=0
    g10: LineSegment StartX=-70.51 StartY=30.8 StartZ=0 EndX=-78.51 EndY=30.8 EndZ=0
    g11: LineSegment StartX=-78.51 StartY=30.8 StartZ=0 EndX=-78.51 EndY=36.4 EndZ=0
  constraints (33):
    c: Horizontal(g0)
    c: Coincident(g1,g0)
    c: Coincident(g2,g1)
    c: Horizontal(g2)
    c: Coincident(g3,g2)
    c: Coincident(g3,g0)
    c: Vertical(g3)
    c: DistanceX(g2,g2) = 7.6
    c: Coincident(g1,g-3)
    c: Coincident(g0,g-3)
    c: Horizontal(g4)
    c: Coincident(g5,g4)
    c: Vertical(g5)
    c: Coincident(g6,g5)
    c: Horizontal(g6)
    c: Coincident(g7,g6)
    c: Coincident(g7,g4)
    c: Vertical(g7)
    c: DistanceY(g5,g5) = 5.6
    c: DistanceX(g4,g4) = 9.6
    c: Coincident(g9,g8)
    c: Vertical(g9)
    c: Coincident(g10,g9)
    c: Horizontal(g10)
    c: Coincident(g11,g10)
    c: Coincident(g11,g8)
    c: Vertical(g11)
    c: DistanceY(g9,g9) = 5.6
    c: DistanceX(g10,g10) = 8
    c: Coincident(g4,g-4)
    c: DistanceX(g4,g10) = 1.6
    c: Horizontal(g8)
    c: DistanceY(g8,g1) = 0
FEATURE [Sketcher::SketchObject] Sketch034  label="buchi guida rail"
  ArcFitTolerance = 1e-06
  AttachmentSupport = -> [XY_Plane]
  ExternalGeometry = -> [Sketch]
  FullyConstrained = true
  MakeInternals = false
  MapMode = 5
  sketch-geometry (6):
    g0: LineSegment [constr] StartX=-100.8 StartY=9.1e-15 StartZ=0 EndX=-93.3 EndY=0 EndZ=0
    g1: LineSegment [constr] StartX=-93.3 StartY=0 StartZ=0 EndX=-73.3 EndY=0 EndZ=0
    g2: LineSegment [constr] StartX=-73.3 StartY=0 StartZ=0 EndX=-53.3 EndY=0 EndZ=0
    g3: Circle CenterX=-93.3 CenterY=0 CenterZ=0 NormalX=0 NormalY=0 NormalZ=1 AngleXU=0 Radius=2.5
    g4: Circle CenterX=-73.3 CenterY=0 CenterZ=0 NormalX=0 NormalY=0 NormalZ=1 AngleXU=0 Radius=2.5
    g5: Circle CenterX=-53.3 CenterY=0 CenterZ=0 NormalX=0 NormalY=0 NormalZ=1 AngleXU=0 Radius=2.5
  constraints (15):
    c: Distance(g0) = 7.5
    c: Coincident(g0,g-3)
    c: PointOnObject(g0,g-1)
    c: Distance(g1) = 20
    c: Coincident(g1,g0)
    c: PointOnObject(g1,g-1)
    c: Distance(g2) = 20
    c: Coincident(g2,g1)
    c: PointOnObject(g2,g-1)
    c: Diameter(g3) = 5
    c: Diameter(g4) = 5
    c: Diameter(g5) = 5
    c: Coincident(g3,g0)
    c: Coincident(g4,g1)
    c: Coincident(g5,g2)
FEATURE [PartDesign::FeatureBase] BaseFeature
  BaseFeature = -> Extrude017
  Suppressed = false
FEATURE [PartDesign::Body] Body001  label="perno fermo rumble"
  AllowCompound = false
  BaseFeature = -> Extrude017
  Group = -> [BaseFeature,Sketch021]
  Origin = -> Origin001
  Tip = -> BaseFeature
FEATURE [Part::Extrusion] Extrude032  label="Extrude buchi guida rail"
  Base = -> Sketch034
  Dir = (0,0,1)
  DirMode = 2
  FaceMakerClass = Part::FaceMakerBullseye
  FaceMakerMode = 3
  LengthFwd = -6.2
  LengthRev = 0
  Placement = pos=(0,0,43.2) rot=(0,0,1;0rad)
  Solid = true
  Symmetric = false
FEATURE [Part::Extrusion] Extrude033  label="Extrude fori superiori per solenoide e oled001"
  Base = -> Sketch030
  Dir = (0,0,1)
  DirMode = 2
  FaceMakerClass = Part::FaceMakerBullseye
  FaceMakerMode = 3
  LengthFwd = -4.8
  LengthRev = 0
  Placement = pos=(0,0,41.2) rot=(0,0,1;0rad)
  Solid = true
  Symmetric = false
FEATURE [Part::Extrusion] Extrude034  label="Extrude fori sotto impugnatura001"
  Base = -> Sketch029
  Dir = (0,0,1)
  DirMode = 2
  FaceMakerClass = Part::FaceMakerBullseye
  FaceMakerMode = 3
  LengthFwd = 5
  LengthRev = 0
  Placement = pos=(0,0,-83) rot=(0,0,1;0rad)
  Solid = true
  Symmetric = false
FEATURE [Part::Extrusion] Extrude035  label="Extrude fori inferiori switch pompa001"
  Base = -> Sketch031
  Dir = (0,0,1)
  DirMode = 2
  FaceMakerClass = Part::FaceMakerBullseye
  FaceMakerMode = 3
  LengthFwd = 4
  LengthRev = 0
  Placement = pos=(0,0,-1.7) rot=(0,0,1;0rad)
  Solid = true
  Symmetric = false
FEATURE [Part::Extrusion] Extrude036  label="Extrude foro sotto posteriore M3x5x007"
  Base = -> Sketch027
  Dir = (0,0,1)
  DirMode = 2
  FaceMakerClass = Part::FaceMakerBullseye
  FaceMakerMode = 3
  LengthFwd = 6.2
  LengthRev = 0
  Placement = pos=(0,0,-9.6) rot=(0,0,1;0rad)
  Solid = true
  Symmetric = false
FEATURE [Part::Extrusion] Extrude037  label="Extrude foro sotto anteriore M3x5x007"
  Base = -> Sketch026
  Dir = (0,0,1)
  DirMode = 2
  FaceMakerClass = Part::FaceMakerBullseye
  FaceMakerMode = 3
  LengthFwd = 6.2
  LengthRev = 0
  Solid = true
  Symmetric = false
FEATURE [Sketcher::SketchObject] Sketch035  label="foro per fissaggio micro"
  ArcFitTolerance = 1e-06
  AttachmentSupport = -> [XZ_Plane]
  ExternalGeometry = -> [Sketch,Sketch033]
  FullyConstrained = true
  MakeInternals = false
  MapMode = 5
  Placement = pos=(0,0,0) rot=(1,0,0;1.5708rad)
  sketch-geometry (3):
    g0: Circle CenterX=-7.8 CenterY=21.2 CenterZ=0 NormalX=0 NormalY=0 NormalZ=1 AngleXU=0 Radius=1.6
    g1: GeomPoint [constr] X=-4 Y=21.2 Z=0
    g2: LineSegment [constr] StartX=-4 StartY=21.2 StartZ=0 EndX=-11.6 EndY=21.2 EndZ=0
  constraints (6):
    c: Diameter(g0) = 3.2
    c: Symmetric(g-3,g-3,g1)
    c: Coincident(g2,g1)
    c: Horizontal(g2)
    c: DistanceX(g-4,g2) = 0
    c: Symmetric(g2,g1,g0)
FEATURE [Part::Extrusion] Extrude038  label="Extrude foro per fissaggio micro"
  Base = -> Sketch035
  Dir = (0,-1,2e-16)
  DirMode = 2
  FaceMakerClass = Part::FaceMakerBullseye
  FaceMakerMode = 3
  LengthFwd = 3
  LengthRev = 0
  Placement = pos=(0,8.6,0) rot=(0,0,1;0rad)
  Solid = true
  Symmetric = false
FEATURE [Sketcher::SketchObject] Sketch036  label="supporto per alimentatore"
  ArcFitTolerance = 1e-06
  AttachmentSupport = -> [XZ_Plane]
  ExternalGeometry = -> [Sketch,Sketch016,Sketch022]
  FullyConstrained = true
  MakeInternals = false
  MapMode = 5
  Placement = pos=(0,0,0) rot=(1,0,0;1.5708rad)
  sketch-geometry (5):
    g0: LineSegment StartX=-211.843 StartY=-50.0944 StartZ=0 EndX=-211.843 EndY=-80.4316 EndZ=0
    g1: LineSegment StartX=-211.843 StartY=-50.0944 StartZ=0 EndX=-207.775 EndY=-41.3701 EndZ=0
    g2: LineSegment [constr] StartX=-209.443 StartY=-50.0944 StartZ=0 EndX=-209.443 EndY=-80.4316 EndZ=0
    g3: LineSegment StartX=-207.775 StartY=-41.3701 StartZ=0 EndX=-207.775 EndY=-80.4316 EndZ=0
    g4: LineSegment StartX=-211.843 StartY=-80.4316 StartZ=0 EndX=-207.775 EndY=-80.4316 EndZ=0
  constraints (15):
    c: Vertical(g0)
    c: Coincident(g1,g0)
    c: Vertical(g2)
    c: Tangent(g2,g-5)
    c: Coincident(g3,g1)
    c: Vertical(g3)
    c: DistanceY(g-3,g3) = -2
    c: Tangent(g1,g-8)
    c: DistanceY(g-3,g0) = -2
    c: Coincident(g4,g0)
    c: Coincident(g4,g3)
    c: Tangent(g0,g-6)
    c: DistanceY(g-3,g2) = -2
    c: DistanceY(g2,g0) = 0
    c: DistanceX(g-3,g3) = 6.8
FEATURE [Part::Extrusion] Extrude039  label="Extrude039 supporto alimentatore"
  Base = -> Sketch036
  Dir = (0,-1,2e-16)
  DirMode = 2
  FaceMakerClass = Part::FaceMakerBullseye
  FaceMakerMode = 3
  LengthFwd = 25.2
  LengthRev = 0
  Solid = true
  Symmetric = true
FEATURE [Sketcher::SketchObject] Sketch037  label="scavo per alimentatore"
  ArcFitTolerance = 1e-06
  AttachmentSupport = -> [XZ_Plane]
  ExternalGeometry = -> [Sketch036]
  FullyConstrained = true
  MakeInternals = false
  MapMode = 5
  Placement = pos=(0,0,0) rot=(1,0,0;1.5708rad)
  sketch-geometry (4):
    g0: LineSegment StartX=-209.575 StartY=-50.4316 StartZ=0 EndX=-209.575 EndY=-80.4316 EndZ=0
    g1: LineSegment StartX=-209.575 StartY=-50.4316 StartZ=0 EndX=-207.775 EndY=-50.4316 EndZ=0
    g2: LineSegment StartX=-207.775 StartY=-50.4316 StartZ=0 EndX=-207.775 EndY=-80.4316 EndZ=0
    g3: LineSegment StartX=-207.775 StartY=-80.4316 StartZ=0 EndX=-209.575 EndY=-80.4316 EndZ=0
  constraints (11):
    c: Vertical(g0)
    c: Coincident(g1,g0)
    c: Horizontal(g1)
    c: Coincident(g2,g1)
    c: Vertical(g2)
    c: Coincident(g3,g2)
    c: Coincident(g3,g0)
    c: Horizontal(g3)
    c: DistanceX(g1,g1) = 1.8
    c: Coincident(g2,g-3)
    c: DistanceY(g2,g2) = 30
FEATURE [Part::Extrusion] Extrude040  label="Extrude040 scavo alimentatore"
  Base = -> Sketch037
  Dir = (0,-1,2e-16)
  DirMode = 2
  FaceMakerClass = Part::FaceMakerBullseye
  FaceMakerMode = 3
  LengthFwd = 19.5
  LengthRev = 0
  Solid = true
  Symmetric = true
FEATURE [Part::Extrusion] Extrude031  label="Extrude fermo per scheda micro"
  Base = -> Sketch033
  Dir = (0,-1,2e-16)
  DirMode = 2
  FaceMakerClass = Part::FaceMakerBullseye
  FaceMakerMode = 3
  LengthFwd = 3
  LengthRev = 0
  Placement = pos=(0,8.6,0) rot=(0,0,1;0rad)
  Solid = true
  Symmetric = false
FEATURE [Sketcher::SketchObject] Sketch038  label="scavo driver solenoide"
  ArcFitTolerance = 1e-06
  AttachmentSupport = -> [XZ_Plane]
  ExternalGeometry = -> [Sketch,Sketch036]
  FullyConstrained = true
  MakeInternals = false
  MapMode = 5
  Placement = pos=(0,0,0) rot=(1,0,0;1.5708rad)
  sketch-geometry (7):
    g0: LineSegment StartX=-193.66 StartY=-11.0994 StartZ=0 EndX=-195.11 EndY=-10.4232 EndZ=0
    g1: LineSegment StartX=-195.11 StartY=-10.4232 StartZ=0 EndX=-209.225 EndY=-40.6939 EndZ=0
    g2: LineSegment StartX=-193.66 StartY=-11.0994 StartZ=0 EndX=-190.216 EndY=-12.7054 EndZ=0
    g3: LineSegment StartX=-190.216 StartY=-12.7054 StartZ=0 EndX=-204.331 EndY=-42.9761 EndZ=0
    g4: LineSegment StartX=-204.331 StartY=-42.9761 StartZ=0 EndX=-207.775 EndY=-41.3701 EndZ=0
    g5: LineSegment [constr] StartX=-209.225 StartY=-40.6939 StartZ=0 EndX=-207.775 EndY=-41.3701 EndZ=0
    g6: LineSegment StartX=-209.225 StartY=-40.6939 StartZ=0 EndX=-207.775 EndY=-41.3701 EndZ=0
  constraints (19):
    c: Coincident(g1,g0)
    c: Coincident(g3,g2)
    c: Coincident(g4,g3)
    c: Distance(g2) = 3.8
    c: Distance(g1) = 33.4
    c: Coincident(g5,g1)
    c: Distance(g5) = 1.6
    c: Coincident(g-4,g5)
    c: Perpendicular(g5,g-3)
    c: Parallel(g1,g-3)
    c: Perpendicular(g1,g0)
    c: Distance(g0) = 1.6
    c: Coincident(g6,g1)
    c: Coincident(g6,g5)
    c: Parallel(g3,g-3)
    c: Perpendicular(g3,g4)
    c: Perpendicular(g2,g3)
    c: Coincident(g2,g0)
    c: Coincident(g4,g5)
FEATURE [Part::Extrusion] Extrude041  label="Extrude scavo driver solenoide"
  Base = -> Sketch038
  Dir = (0,-1,2e-16)
  DirMode = 2
  FaceMakerClass = Part::FaceMakerBullseye
  FaceMakerMode = 3
  LengthFwd = 17
  LengthRev = 0
  Solid = true
  Symmetric = true
FEATURE [Sketcher::SketchObject] Sketch039  label="scavo per cavo usb per micro"
  ArcFitTolerance = 1e-06
  AttachmentSupport = -> [XZ_Plane]
  ExternalGeometry = -> [Sketch,Sketch016]
  FullyConstrained = true
  MakeInternals = false
  MapMode = 5
  Placement = pos=(0,0,0) rot=(1,0,0;1.5708rad)
  sketch-geometry (4):
    g0: LineSegment StartX=-82.51 StartY=36.4 StartZ=0 EndX=-74.51 EndY=36.4 EndZ=0
    g1: LineSegment StartX=-74.51 StartY=36.4 StartZ=0 EndX=-74.51 EndY=30.8 EndZ=0
    g2: LineSegment StartX=-74.51 StartY=30.8 StartZ=0 EndX=-82.51 EndY=30.8 EndZ=0
    g3: LineSegment StartX=-82.51 StartY=30.8 StartZ=0 EndX=-82.51 EndY=36.4 EndZ=0
  constraints (11):
    c: Coincident(g1,g0)
    c: Vertical(g1)
    c: Coincident(g2,g1)
    c: Horizontal(g2)
    c: Coincident(g3,g2)
    c: Coincident(g3,g0)
    c: Vertical(g3)
    c: Tangent(g0,g-3)
    c: Tangent(g2,g-4)
    c: Tangent(g3,g-4)
    c: Tangent(g1,g-4)
FEATURE [Part::Extrusion] Extrude042  label="Extrude scavo per cavo usb per micro"
  Base = -> Sketch039
  Dir = (0,-1,2e-16)
  DirMode = 2
  FaceMakerClass = Part::FaceMakerBullseye
  FaceMakerMode = 3
  LengthFwd = 11.2
  LengthRev = 0
  Solid = true
  Symmetric = true
FEATURE [Sketcher::SketchObject] Sketch040  label="scavo saldature alimentatore connettore 5v"
  ArcFitTolerance = 1e-06
  AttachmentSupport = -> [XZ_Plane]
  ExternalGeometry = -> [Sketch037]
  FullyConstrained = true
  MakeInternals = false
  MapMode = 5
  Placement = pos=(0,0,0) rot=(1,0,0;1.5708rad)
  sketch-geometry (4):
    g0: LineSegment StartX=-211.175 StartY=-52.4316 StartZ=0 EndX=-211.175 EndY=-56.4316 EndZ=0
    g1: LineSegment StartX=-211.175 StartY=-52.4316 StartZ=0 EndX=-209.575 EndY=-52.4316 EndZ=0
    g2: LineSegment StartX=-209.575 StartY=-52.4316 StartZ=0 EndX=-209.575 EndY=-56.4316 EndZ=0
    g3: LineSegment StartX=-209.575 StartY=-56.4316 StartZ=0 EndX=-211.175 EndY=-56.4316 EndZ=0
  constraints (11):
    c: Vertical(g0)
    c: Coincident(g1,g0)
    c: Horizontal(g1)
    c: Coincident(g2,g1)
    c: Coincident(g3,g2)
    c: Coincident(g3,g0)
    c: Horizontal(g3)
    c: DistanceX(g1,g1) = 1.6
    c: DistanceY(g2,g2) = 4
    c: Tangent(g2,g-3)
    c: DistanceY(g1,g-3) = 2
FEATURE [Part::Extrusion] Extrude043  label="Extrude scavo saldature alimentatore connettore 5v"
  Base = -> Sketch040
  Dir = (0,-1,2e-16)
  DirMode = 2
  FaceMakerClass = Part::FaceMakerBullseye
  FaceMakerMode = 3
  LengthFwd = 8
  LengthRev = 0
  Solid = true
  Symmetric = true
FEATURE [Sketcher::SketchObject] Sketch041  label="scavo saldature alimentatore connettore 5v verticali"
  ArcFitTolerance = 1e-06
  AttachmentSupport = -> [XZ_Plane]
  ExternalGeometry = -> [Sketch037]
  FullyConstrained = true
  MakeInternals = false
  MapMode = 5
  Placement = pos=(0,0,0) rot=(1,0,0;1.5708rad)
  sketch-geometry (4):
    g0: LineSegment StartX=-211.175 StartY=-53.6316 StartZ=0 EndX=-209.575 EndY=-53.6316 EndZ=0
    g1: LineSegment StartX=-209.575 StartY=-53.6316 StartZ=0 EndX=-209.575 EndY=-76.6316 EndZ=0
    g2: LineSegment StartX=-209.575 StartY=-76.6316 StartZ=0 EndX=-211.175 EndY=-76.6316 EndZ=0
    g3: LineSegment StartX=-211.175 StartY=-76.6316 StartZ=0 EndX=-211.175 EndY=-53.6316 EndZ=0
  constraints (11):
    c: Horizontal(g0)
    c: Coincident(g1,g0)
    c: Coincident(g2,g1)
    c: Horizontal(g2)
    c: Coincident(g3,g2)
    c: Coincident(g3,g0)
    c: Vertical(g3)
    c: DistanceY(g3,g3) = 23
    c: DistanceX(g0,g0) = 1.6
    c: Tangent(g1,g-3)
    c: DistanceY(g0,g-3) = 3.2
FEATURE [Part::Extrusion] Extrude044  label="Extrude scavo saldature alimentatore connettore 5v verticali"
  Base = -> Sketch041
  Dir = (0,-1,2e-16)
  DirMode = 2
  FaceMakerClass = Part::FaceMakerBullseye
  FaceMakerMode = 3
  LengthFwd = 3.2
  LengthRev = 0
  Placement = pos=(0,8.3,0) rot=(0,0,1;0rad)
  Solid = true
  Symmetric = false
FEATURE [Sketcher::SketchObject] Sketch042  label="fermi per driver solenoide e alimentatore"
  ArcFitTolerance = 1e-06
  AttachmentSupport = -> [XZ_Plane]
  ExternalGeometry = -> [Sketch036,Sketch037,Sketch,Sketch038]
  FullyConstrained = true
  MakeInternals = false
  MapMode = 5
  Placement = pos=(0,0,0) rot=(1,0,0;1.5708rad)
  sketch-geometry (27):
    g0: LineSegment StartX=-195.773 StartY=-15.631 StartZ=0 EndX=-196.702 EndY=-17.6249 EndZ=0
    g1: LineSegment StartX=-196.702 StartY=-17.6249 StartZ=0 EndX=-194.709 EndY=-18.5546 EndZ=0
    g2: LineSegment StartX=-194.709 StartY=-18.5546 StartZ=0 EndX=-193.779 EndY=-16.5607 EndZ=0
    g3: LineSegment StartX=-193.779 StartY=-16.5607 StartZ=0 EndX=-195.773 EndY=-15.631 EndZ=0
    g4: LineSegment StartX=-196.547 StartY=-13.5047 StartZ=0 EndX=-198.829 EndY=-18.3988 EndZ=0
    g5: LineSegment StartX=-198.829 StartY=-18.3988 StartZ=0 EndX=-195.385 EndY=-20.0047 EndZ=0
    g6: LineSegment StartX=-193.258 StartY=-19.2308 StartZ=0 EndX=-192.329 EndY=-17.2369 EndZ=0
    g7: LineSegment StartX=-193.103 StartY=-15.1106 StartZ=0 EndX=-196.547 EndY=-13.5047 EndZ=0
    g8: LineSegment [constr] StartX=-193.935 StartY=-20.6809 StartZ=0 EndX=-193.258 EndY=-19.2308 EndZ=0
    g9: LineSegment [constr] StartX=-193.935 StartY=-20.6809 StartZ=0 EndX=-195.385 EndY=-20.0047 EndZ=0
    g10: ArcOfCircle CenterX=-193.779 CenterY=-16.5607 CenterZ=0 NormalX=0 NormalY=0 NormalZ=1 AngleXU=0 Radius=1.6 StartAngle=5.84685 EndAngle=7.41765
    g11: GeomPoint [constr] X=-191.653 Y=-15.7868 Z=0
    g12: ArcOfCircle CenterX=-194.709 CenterY=-18.5546 CenterZ=0 NormalX=0 NormalY=0 NormalZ=1 AngleXU=0 Radius=1.6 StartAngle=4.27606 EndAngle=5.84685
    g13: GeomPoint [constr] X=-193.935 Y=-20.6809 Z=0
    g14: LineSegment StartX=-207.775 StartY=-46.8316 StartZ=0 EndX=-207.775 EndY=-50.8316 EndZ=0
    g15: LineSegment StartX=-207.775 StartY=-46.8316 StartZ=0 EndX=-203.775 EndY=-46.8316 EndZ=0
    g16: LineSegment StartX=-203.775 StartY=-46.8316 StartZ=0 EndX=-203.775 EndY=-50.8316 EndZ=0
    g17: LineSegment StartX=-207.775 StartY=-50.8316 StartZ=0 EndX=-203.775 EndY=-50.8316 EndZ=0
    g18: LineSegment StartX=-209.375 StartY=-52.4316 StartZ=0 EndX=-203.775 EndY=-52.4316 EndZ=0
    g19: LineSegment StartX=-202.175 StartY=-50.8316 StartZ=0 EndX=-202.175 EndY=-46.8316 EndZ=0
    g20: LineSegment StartX=-203.775 StartY=-45.2316 StartZ=0 EndX=-209.375 EndY=-45.2316 EndZ=0
    g21: LineSegment StartX=-209.375 StartY=-45.2316 StartZ=0 EndX=-209.375 EndY=-52.4316 EndZ=0
    g22: ArcOfCircle CenterX=-203.775 CenterY=-46.8316 CenterZ=0 NormalX=0 NormalY=0 NormalZ=1 AngleXU=0 Radius=1.6 StartAngle=1.8e-15 EndAngle=1.5708
    g23: GeomPoint [constr] X=-202.175 Y=-45.2316 Z=0
    g24: ArcOfCircle CenterX=-203.775 CenterY=-50.8316 CenterZ=0 NormalX=0 NormalY=0 NormalZ=1 AngleXU=0 Radius=1.6 StartAngle=4.71239 EndAngle=6.28319
    g25: GeomPoint [constr] X=-202.175 Y=-52.4316 Z=0
    g26: LineSegment [constr] StartX=-207.775 StartY=-50.4316 StartZ=0 EndX=-207.775 EndY=-50.8316 EndZ=0
  constraints (69):
    c: Coincident(g1,g0)
    c: Coincident(g2,g1)
    c: Coincident(g3,g2)
    c: Coincident(g3,g0)
    c: Parallel(g0,g2)
    c: Perpendicular(g3,g0)
    c: Perpendicular(g1,g0)
    c: Coincident(g5,g4)
    c: Coincident(g7,g4)
    c: Distance(g3) = 2.2
    c: Distance(g2) = 2.2
    c: Parallel(g6,g2)
    c: Parallel(g6,g4)
    c: Perpendicular(g5,g6)
    c: Perpendicular(g7,g6)
    c: Distance(g13,g11) = 5.4
    c: Distance(g5,g13) = 5.4
    c: Coincident(g9,g8)
    c: Distance(g8) = 1.6
    c: Distance(g9) = 1.6
    c: Perpendicular(g9,g8)
    c: Parallel(g8,g6)
    c: Coincident(g8,g13)
    c: Distance(g8,g1) = 1.6
    c: Distance(g9,g1) = 1.6
    c: Tangent(g0,g-5)
    c: Distance(g0,g-6) = 26.2
    c: PointOnObject(g11,g7)
    c: PointOnObject(g11,g6)
    c: Tangent(g7,g10) = -1.5708
    c: Tangent(g6,g10) = -1.5708
    c: PointOnObject(g13,g5)
    c: Tangent(g5,g12) = -1.5708
    c: Tangent(g6,g12) = -1.5708
    c: Equal(g10,g12)
    c: Coincident(g10,g2)
    c: Vertical(g14)
    c: Coincident(g15,g14)
    c: Horizontal(g15)
    c: Coincident(g16,g15)
    c: Vertical(g16)
    c: Coincident(g17,g14)
    c: Coincident(g17,g16)
    c: Horizontal(g17)
    c: Distance(g16) = 4
    c: Distance(g15) = 4
    c: Horizontal(g18)
    c: Vertical(g19)
    c: Horizontal(g20)
    c: Coincident(g21,g20)
    c: Coincident(g21,g18)
    c: Vertical(g21)
    c: Distance(g20,g23) = 7.2
    c: Distance(g25,g23) = 7.2
    c: DistanceY(g18,g14) = 1.6
    c: DistanceX(g18,g14) = 1.6
    c: PointOnObject(g23,g20)
    c: PointOnObject(g23,g19)
    c: Tangent(g20,g22) = -1.5708
    c: Tangent(g19,g22) = -1.5708
    c: PointOnObject(g25,g19)
    c: Tangent(g18,g24) = -1.5708
    c: Tangent(g19,g24) = -1.5708
    c: Equal(g22,g24)
    c: Coincident(g22,g15)
    c: Vertical(g26)
    c: Distance(g26) = 0.4
    c: Coincident(g26,g-4)
    c: Coincident(g14,g26)
FEATURE [Part::Extrusion] Extrude045  label="Extrude fermi per driver solenoide e alimentatore"
  Base = -> Sketch042
  Dir = (0,-1,2e-16)
  DirMode = 2
  FaceMakerClass = Part::FaceMakerBullseye
  FaceMakerMode = 3
  LengthFwd = 25.2
  LengthRev = 0
  Solid = true
  Symmetric = true
FEATURE [Sketcher::SketchObject] Sketch043  label="scavo pulizia fermo alimentatore"
  ArcFitTolerance = 1e-06
  AttachmentSupport = -> [XZ_Plane]
  ExternalGeometry = -> [Sketch042,Sketch036,Sketch037]
  FullyConstrained = true
  MakeInternals = false
  MapMode = 5
  Placement = pos=(0,0,0) rot=(1,0,0;1.5708rad)
  sketch-geometry (6):
    g0: LineSegment StartX=-209.375 StartY=-52.4316 StartZ=0 EndX=-209.375 EndY=-50.4316 EndZ=0
    g1: LineSegment StartX=-209.375 StartY=-50.4316 StartZ=0 EndX=-207.775 EndY=-50.4316 EndZ=0
    g2: LineSegment StartX=-207.775 StartY=-50.4316 StartZ=0 EndX=-207.775 EndY=-45.2316 EndZ=0
    g3: LineSegment StartX=-207.775 StartY=-45.2316 StartZ=0 EndX=-202.175 EndY=-45.2316 EndZ=0
    g4: LineSegment StartX=-202.175 StartY=-45.2316 StartZ=0 EndX=-202.175 EndY=-52.4316 EndZ=0
    g5: LineSegment StartX=-202.175 StartY=-52.4316 StartZ=0 EndX=-209.375 EndY=-52.4316 EndZ=0
  constraints (13):
    c: Vertical(g0)
    c: Coincident(g1,g0)
    c: Coincident(g2,g1)
    c: Coincident(g3,g2)
    c: Coincident(g4,g3)
    c: Coincident(g5,g4)
    c: Coincident(g5,g0)
    c: Horizontal(g5)
    c: Coincident(g0,g-6)
    c: Tangent(g1,g-8)
    c: Tangent(g2,g-4)
    c: Tangent(g3,g-7)
    c: Tangent(g4,g-3)
FEATURE [Part::Extrusion] Extrude046  label="Extrude scavo pulizia fermo alimentatore"
  Base = -> Sketch043
  Dir = (0,-1,2e-16)
  DirMode = 2
  FaceMakerClass = Part::FaceMakerBullseye
  FaceMakerMode = 3
  LengthFwd = 19.5
  LengthRev = 0
  Solid = true
  Symmetric = true
FEATURE [Sketcher::SketchObject] Sketch044  label="buchini per fissaggio oled"
  ArcFitTolerance = 1e-06
  AttachmentSupport = -> [YZ_Plane]
  ExternalGeometry = -> [Sketch]
  FullyConstrained = true
  MakeInternals = false
  MapMode = 5
  Placement = pos=(0,0,0) rot=(0.57735,0.57735,0.57735;2.0944rad)
  sketch-geometry (5):
    g0: LineSegment [constr] StartX=1.5e-14 StartY=67.3588 StartZ=0 EndX=0 EndY=64.3588 EndZ=0
    g1: LineSegment [constr] StartX=0 StartY=64.3588 StartZ=0 EndX=10.4 EndY=64.3588 EndZ=0
    g2: LineSegment [constr] StartX=0 StartY=64.3588 StartZ=0 EndX=-10.4 EndY=64.3588 EndZ=0
    g3: Circle CenterX=10.4 CenterY=64.3588 CenterZ=0 NormalX=0 NormalY=0 NormalZ=1 AngleXU=0 Radius=1.5
    g4: Circle CenterX=-10.4 CenterY=64.3588 CenterZ=0 NormalX=0 NormalY=0 NormalZ=1 AngleXU=0 Radius=1.5
  constraints (13):
    c: Distance(g0) = 3
    c: PointOnObject(g0,g-2)
    c: Coincident(g1,g0)
    c: Horizontal(g1)
    c: Coincident(g2,g0)
    c: Horizontal(g2)
    c: DistanceX(g1,g1) = 10.4
    c: Coincident(g3,g1)
    c: Diameter(g4) = 3
    c: Coincident(g4,g2)
    c: Coincident(g0,g-7)
    c: Equal(g1,g2)
    c: Equal(g4,g3)
FEATURE [Part::Extrusion] Extrude047  label="Extrude buchini per fissaggio oled"
  Base = -> Sketch044
  Dir = (1,0,0)
  DirMode = 2
  FaceMakerClass = Part::FaceMakerBullseye
  FaceMakerMode = 3
  LengthFwd = 10
  LengthRev = 0
  Placement = pos=(-186,0,0) rot=(0,0,1;0rad)
  Solid = true
  Symmetric = false
FEATURE [Sketcher::SketchObject] Sketch046  label="scavo 5x5 neopixel"
  ArcFitTolerance = 1e-06
  AttachmentSupport = -> [YZ_Plane002]
  FullyConstrained = true
  MakeInternals = false
  MapMode = 5
  Placement = pos=(0,0,0) rot=(0.57735,0.57735,0.57735;2.0944rad)
  sketch-geometry (4):
    g0: LineSegment StartX=-2.7 StartY=2.7 StartZ=0 EndX=2.7 EndY=2.7 EndZ=0
    g1: LineSegment StartX=2.7 StartY=2.7 StartZ=0 EndX=2.7 EndY=-2.7 EndZ=0
    g2: LineSegment StartX=2.7 StartY=-2.7 StartZ=0 EndX=-2.7 EndY=-2.7 EndZ=0
    g3: LineSegment StartX=-2.7 StartY=-2.7 StartZ=0 EndX=-2.7 EndY=2.7 EndZ=0
  constraints (11):
    c: Horizontal(g0)
    c: Coincident(g1,g0)
    c: Vertical(g1)
    c: Coincident(g2,g1)
    c: Horizontal(g2)
    c: Coincident(g3,g2)
    c: Coincident(g3,g0)
    c: Vertical(g3)
    c: DistanceX(g0,g0) = 5.4
    c: DistanceY(g1,g1) = 5.4
    c: Symmetric(g0,g1,g-1)
FEATURE [Part::Extrusion] Extrude049  label="Extrude scavo 5x5 neopixel"
  Base = -> Sketch046
  Dir = (1,0,0)
  DirMode = 2
  FaceMakerClass = Part::FaceMakerBullseye
  FaceMakerMode = 3
  LengthFwd = 1
  LengthRev = 0
  Solid = true
  Symmetric = false
FEATURE [Sketcher::SketchObject] Sketch047  label="scavo 10x10 neopixel corpo"
  ArcFitTolerance = 1e-06
  AttachmentSupport = -> [YZ_Plane002]
  FullyConstrained = true
  MakeInternals = false
  MapMode = 5
  Placement = pos=(0,0,0) rot=(0.57735,0.57735,0.57735;2.0944rad)
  sketch-geometry (4):
    g0: LineSegment StartX=-5 StartY=5.1 StartZ=0 EndX=5 EndY=5.1 EndZ=0
    g1: LineSegment StartX=5 StartY=5.1 StartZ=0 EndX=5 EndY=-5.1 EndZ=0
    g2: LineSegment StartX=5 StartY=-5.1 StartZ=0 EndX=-5 EndY=-5.1 EndZ=0
    g3: LineSegment StartX=-5 StartY=-5.1 StartZ=0 EndX=-5 EndY=5.1 EndZ=0
  constraints (11):
    c: Horizontal(g0)
    c: Coincident(g1,g0)
    c: Vertical(g1)
    c: Coincident(g2,g1)
    c: Horizontal(g2)
    c: Coincident(g3,g2)
    c: Coincident(g3,g0)
    c: Vertical(g3)
    c: DistanceX(g0,g0) = 10
    c: DistanceY(g1,g1) = 10.2
    c: Symmetric(g0,g2,g-1)
FEATURE [Part::Extrusion] Extrude050  label="Extrude scavo 10x10 neopixel corpo"
  Base = -> Sketch047
  Dir = (1,0,0)
  DirMode = 2
  FaceMakerClass = Part::FaceMakerBullseye
  FaceMakerMode = 3
  LengthFwd = 8
  LengthRev = 0
  Placement = pos=(1,0,0) rot=(0,0,1;0rad)
  Solid = true
  Symmetric = false
FEATURE [Sketcher::SketchObject] Sketch048  label="buco per perno blocco neopixel"
  ArcFitTolerance = 1e-06
  AttachmentSupport = -> [XZ_Plane002]
  FullyConstrained = true
  MakeInternals = false
  MapMode = 5
  Placement = pos=(0,0,0) rot=(1,0,0;1.5708rad)
  sketch-geometry (4):
    g0: LineSegment StartX=3 StartY=1.2 StartZ=0 EndX=3 EndY=-1.2 EndZ=0
    g1: LineSegment StartX=3 StartY=-1.2 StartZ=0 EndX=5.4 EndY=-1.2 EndZ=0
    g2: LineSegment StartX=5.4 StartY=-1.2 StartZ=0 EndX=5.4 EndY=1.2 EndZ=0
    g3: LineSegment StartX=5.4 StartY=1.2 StartZ=0 EndX=3 EndY=1.2 EndZ=0
  constraints (11):
    c: Coincident(g1,g0)
    c: Horizontal(g1)
    c: Coincident(g2,g1)
    c: Vertical(g2)
    c: Coincident(g3,g2)
    c: Coincident(g3,g0)
    c: Horizontal(g3)
    c: DistanceX(g1,g1) = 2.4
    c: DistanceY(g2,g2) = 2.4
    c: Symmetric(g0,g0,g-1)
    c: DistanceX(g-1,g0) = 3
FEATURE [Sketcher::SketchObject] Sketch045  label="blocco principale per neopixel"
  ArcFitTolerance = 1e-06
  AttachmentSupport = -> [XZ_Plane002]
  ExternalGeometry = -> [Sketch048]
  FullyConstrained = true
  MakeInternals = false
  MapMode = 5
  Placement = pos=(0,0,0) rot=(1,0,0;1.5708rad)
  sketch-geometry (6):
    g0: LineSegment StartX=0 StartY=5.1 StartZ=0 EndX=0 EndY=-5.1 EndZ=0
    g1: LineSegment StartX=0 StartY=-5.1 StartZ=0 EndX=3 EndY=-5.1 EndZ=0
    g2: LineSegment StartX=7 StartY=-1.1 StartZ=0 EndX=7 EndY=5.1 EndZ=0
    g3: LineSegment StartX=7 StartY=5.1 StartZ=0 EndX=0 EndY=5.1 EndZ=0
    g4: ArcOfCircle CenterX=3 CenterY=-1.1 CenterZ=0 NormalX=0 NormalY=0 NormalZ=1 AngleXU=0 Radius=4 StartAngle=4.71239 EndAngle=6.28319
    g5: GeomPoint [constr] X=7 Y=-5.1 Z=0
  constraints (15):
    c: Vertical(g0)
    c: Coincident(g1,g0)
    c: Horizontal(g1)
    c: Vertical(g2)
    c: Coincident(g3,g2)
    c: Coincident(g3,g0)
    c: Horizontal(g3)
    c: DistanceY(g0,g0) = 10.2
    c: Symmetric(g0,g0,g-1)
    c: DistanceX(g3,g3) = 7
    c: PointOnObject(g5,g2)
    c: PointOnObject(g5,g1)
    c: Tangent(g2,g4) = -1.5708
    c: Tangent(g1,g4) = -1.5708
    c: DistanceX(g-3,g1) = 0
FEATURE [Part::Extrusion] Extrude048  label="Extrude blocco principale per neopixel"
  Base = -> Sketch045
  Dir = (0,-1,2e-16)
  DirMode = 2
  FaceMakerClass = Part::FaceMakerBullseye
  FaceMakerMode = 3
  LengthFwd = 17
  LengthRev = 0
  Solid = true
  Symmetric = true
FEATURE [Part::Extrusion] Extrude051  label="Extrude buco per perno blocco neopixel"
  Base = -> Sketch048
  Dir = (0,-1,2e-16)
  DirMode = 2
  FaceMakerClass = Part::FaceMakerBullseye
  FaceMakerMode = 3
  LengthFwd = 17
  LengthRev = 0
  Solid = true
  Symmetric = true
FEATURE [Sketcher::SketchObject] Sketch049  label="rinforzi esterni per corpo neopoixel"
  ArcFitTolerance = 1e-06
  AttachmentSupport = -> [XZ_Plane002]
  ExternalGeometry = -> [Sketch045]
  FullyConstrained = true
  MakeInternals = false
  MapMode = 5
  Placement = pos=(0,0,0) rot=(1,0,0;1.5708rad)
  sketch-geometry (8):
    g0: LineSegment StartX=1 StartY=-4.1 StartZ=0 EndX=2 EndY=-4.1 EndZ=0
    g1: LineSegment StartX=2 StartY=-4.1 StartZ=0 EndX=2 EndY=-5.1 EndZ=0
    g2: LineSegment StartX=2 StartY=-5.1 StartZ=0 EndX=1 EndY=-5.1 EndZ=0
    g3: LineSegment StartX=1 StartY=-5.1 StartZ=0 EndX=1 EndY=-4.1 EndZ=0
    g4: LineSegment StartX=1 StartY=5.1 StartZ=0 EndX=2 EndY=5.1 EndZ=0
    g5: LineSegment StartX=2 StartY=5.1 StartZ=0 EndX=2 EndY=4.1 EndZ=0
    g6: LineSegment StartX=2 StartY=4.1 StartZ=0 EndX=1 EndY=4.1 EndZ=0
    g7: LineSegment StartX=1 StartY=4.1 StartZ=0 EndX=1 EndY=5.1 EndZ=0
  constraints (24):
    c: Horizontal(g0)
    c: Coincident(g1,g0)
    c: Vertical(g1)
    c: Coincident(g2,g1)
    c: Horizontal(g2)
    c: Coincident(g3,g2)
    c: Coincident(g3,g0)
    c: Vertical(g3)
    c: Horizontal(g4)
    c: Coincident(g5,g4)
    c: Vertical(g5)
    c: Coincident(g6,g5)
    c: Horizontal(g6)
    c: Coincident(g7,g6)
    c: Coincident(g7,g4)
    c: Vertical(g7)
    c: DistanceX(g4,g4) = 1
    c: DistanceY(g5,g5) = 1
    c: DistanceX(g0,g0) = 1
    c: DistanceY(g1,g1) = 1
    c: DistanceX(g-3,g4) = 1
    c: DistanceY(g-3,g4) = 0
    c: DistanceX(g-4,g2) = 1
    c: DistanceY(g2,g-4) = 0
FEATURE [Part::Extrusion] Extrude052  label="Extrude rinforzi esterni per corpo neopoixel"
  Base = -> Sketch049
  Dir = (0,-1,2e-16)
  DirMode = 2
  FaceMakerClass = Part::FaceMakerBullseye
  FaceMakerMode = 3
  LengthFwd = 17
  LengthRev = 0
  Solid = true
  Symmetric = true
FEATURE [Part::Cut] Cut030
  Base = -> Extrude048
  Refine = true
  Tool = -> Extrude050
FEATURE [Part::Cut] Cut031
  Base = -> Cut030
  Refine = true
  Tool = -> Extrude049
FEATURE [Part::Cut] Cut032
  Base = -> Cut031
  Refine = true
  Tool = -> Extrude051
FEATURE [Part::MultiFuse] Fusion001  label="fusion neopixel"
  Refine = true
  Shapes = -> [Cut032,Extrude052]
FEATURE [Sketcher::SketchObject] Sketch052  label="scavo saldature driver solenoide"
  ArcFitTolerance = 1e-06
  AttachmentSupport = -> [XZ_Plane]
  ExternalGeometry = -> [Sketch038]
  FullyConstrained = true
  MakeInternals = false
  MapMode = 5
  Placement = pos=(0,0,0) rot=(1,0,0;1.5708rad)
  sketch-geometry (4):
    g0: LineSegment StartX=-196.56 StartY=-9.74706 StartZ=0 EndX=-198.25 EndY=-13.3723 EndZ=0
    g1: LineSegment StartX=-198.25 StartY=-13.3723 StartZ=0 EndX=-196.8 EndY=-14.0485 EndZ=0
    g2: LineSegment StartX=-196.8 StartY=-14.0485 StartZ=0 EndX=-195.11 EndY=-10.4232 EndZ=0
    g3: LineSegment StartX=-195.11 StartY=-10.4232 StartZ=0 EndX=-196.56 EndY=-9.74706 EndZ=0
  constraints (11):
    c: Coincident(g1,g0)
    c: Coincident(g2,g1)
    c: Coincident(g3,g2)
    c: Coincident(g3,g0)
    c: Parallel(g2,g0)
    c: Perpendicular(g2,g3)
    c: Perpendicular(g1,g2,g1) = 1.5708
    c: Parallel(g2,g-3)
    c: Distance(g2) = 4
    c: Distance(g3) = 1.6
    c: Coincident(g2,g-3)
FEATURE [Part::Extrusion] Extrude055  label="Extrude scavo saldature driver solenoide"
  Base = -> Sketch052
  Dir = (0,-1,2e-16)
  DirMode = 2
  FaceMakerClass = Part::FaceMakerBullseye
  FaceMakerMode = 3
  LengthFwd = 6
  LengthRev = 0
  Solid = true
  Symmetric = true
FEATURE [Sketcher::SketchObject] Sketch053  label="scavo saldature rumble"
  ArcFitTolerance = 1e-06
  AttachmentSupport = -> [XZ_Plane]
  ExternalGeometry = -> [Sketch019]
  FullyConstrained = true
  MakeInternals = false
  MapMode = 5
  Placement = pos=(0,0,0) rot=(1,0,0;1.5708rad)
  sketch-geometry (4):
    g0: LineSegment StartX=-165.31 StartY=-44.1173 StartZ=0 EndX=-166.547 EndY=-47.9216 EndZ=0
    g1: LineSegment StartX=-166.547 StartY=-47.9216 StartZ=0 EndX=-165.405 EndY=-48.2924 EndZ=0
    g2: LineSegment StartX=-165.405 StartY=-48.2924 StartZ=0 EndX=-164.169 EndY=-44.4881 EndZ=0
    g3: LineSegment StartX=-164.169 StartY=-44.4881 StartZ=0 EndX=-165.31 EndY=-44.1173 EndZ=0
  constraints (11):
    c: Coincident(g1,g0)
    c: Coincident(g2,g1)
    c: Coincident(g3,g2)
    c: Coincident(g3,g0)
    c: Parallel(g0,g2)
    c: Perpendicular(g3,g0)
    c: Perpendicular(g1,g0)
    c: Parallel(g0,g-3)
    c: Distance(g0) = 4
    c: Distance(g1) = 1.2
    c: Coincident(g0,g-3)
FEATURE [Part::Extrusion] Extrude056  label="Extrude scavo saldature rumble"
  Base = -> Sketch053
  Dir = (0,-1,2e-16)
  DirMode = 2
  FaceMakerClass = Part::FaceMakerBullseye
  FaceMakerMode = 3
  LengthFwd = 8.4
  LengthRev = 0
  Solid = true
  Symmetric = true
FEATURE [Part::Cone] Cone  label="Cono"
  Angle = 180
  AttacherType = Attacher::AttachEngine3D
  Height = 15
  Placement = pos=(-176,0,-82.43) rot=(0,0,1;-1.5708rad)
  Radius1 = 12.6
  Radius2 = 10.5
FEATURE [Sketcher::SketchObject] Sketch054  label="scavo saldature alimentatore connettore USB"
  ArcFitTolerance = 1e-06
  AttachmentSupport = -> [XZ_Plane]
  ExternalGeometry = -> [Sketch037]
  FullyConstrained = true
  MakeInternals = false
  MapMode = 5
  Placement = pos=(0,0,0) rot=(1,0,0;1.5708rad)
  sketch-geometry (4):
    g0: LineSegment StartX=-209.575 StartY=-80.4316 StartZ=0 EndX=-210.375 EndY=-80.4316 EndZ=0
    g1: LineSegment StartX=-210.375 StartY=-80.4316 StartZ=0 EndX=-210.375 EndY=-72.4316 EndZ=0
    g2: LineSegment StartX=-210.375 StartY=-72.4316 StartZ=0 EndX=-209.575 EndY=-72.4316 EndZ=0
    g3: LineSegment StartX=-209.575 StartY=-72.4316 StartZ=0 EndX=-209.575 EndY=-80.4316 EndZ=0
  constraints (11):
    c: Horizontal(g0)
    c: Coincident(g1,g0)
    c: Vertical(g1)
    c: Coincident(g2,g1)
    c: Horizontal(g2)
    c: Coincident(g3,g2)
    c: Coincident(g3,g0)
    c: Vertical(g3)
    c: DistanceX(g0,g0) = 0.8
    c: DistanceY(g3,g3) = 8
    c: Coincident(g0,g-4)
FEATURE [Part::Extrusion] Extrude057  label="Extrude scavo saldature alimentatore connettore USB"
  Base = -> Sketch054
  Dir = (0,-1,2e-16)
  DirMode = 2
  FaceMakerClass = Part::FaceMakerBullseye
  FaceMakerMode = 3
  LengthFwd = 11
  LengthRev = 0
  Solid = true
  Symmetric = true
FEATURE [Sketcher::SketchObject] Sketch055  label="buco interno per micro switch"
  ArcFitTolerance = 1e-06
  AttachmentSupport = -> [XZ_Plane]
  ExternalGeometry = -> [Sketch]
  FullyConstrained = true
  MakeInternals = false
  MapMode = 5
  Placement = pos=(0,0,0) rot=(1,0,0;1.5708rad)
  sketch-geometry (11):
    g0: LineSegment [constr] StartX=-194.483 StartY=34.2854 StartZ=0 EndX=-196.022 EndY=30.0568 EndZ=0
    g1: LineSegment [constr] StartX=-196.022 StartY=30.0568 StartZ=0 EndX=-197.561 EndY=25.8282 EndZ=0
    g2: LineSegment [constr] StartX=-196.022 StartY=30.0568 StartZ=0 EndX=-194.143 EndY=29.3727 EndZ=0
    g3: LineSegment [constr] StartX=-196.022 StartY=30.0568 StartZ=0 EndX=-197.902 EndY=30.7408 EndZ=0
    g4: LineSegment StartX=-196.362 StartY=34.9694 StartZ=0 EndX=-192.604 EndY=33.6014 EndZ=0
    g5: LineSegment StartX=-199.441 StartY=26.5122 StartZ=0 EndX=-195.682 EndY=25.1441 EndZ=0
    g6: LineSegment StartX=-192.604 StartY=33.6014 StartZ=0 EndX=-195.682 EndY=25.1441 EndZ=0
    g7: LineSegment StartX=-196.362 StartY=34.9694 StartZ=0 EndX=-199.441 EndY=26.5122 EndZ=0
    g8: GeomPoint [constr] X=-187.821 Y=29.2 Z=0
    g9: LineSegment [constr] StartX=-188.505 StartY=27.3206 StartZ=0 EndX=-196.022 EndY=30.0568 EndZ=0
    g10: LineSegment [constr] StartX=-187.821 StartY=29.2 StartZ=0 EndX=-188.505 EndY=27.3206 EndZ=0
  constraints (27):
    c: Coincident(g2,g0)
    c: Parallel(g0,g-3)
    c: Tangent(g1,g0) = -1.5708
    c: Perpendicular(g0,g2)
    c: Tangent(g2,g3)
    c: Distance(g0,g1) = 9
    c: Equal(g0,g1)
    c: Distance(g3,g2) = 4
    c: Equal(g2,g3)
    c: Parallel(g3,g4)
    c: Symmetric(g4,g4,g0)
    c: Parallel(g6,g1)
    c: Parallel(g7,g1)
    c: Symmetric(g6,g6,g2)
    c: Symmetric(g5,g5,g1)
    c: Symmetric(g7,g7,g3)
    c: Coincident(g7,g4)
    c: Coincident(g6,g4)
    c: Coincident(g5,g6)
    c: Symmetric(g-3,g-3,g8)
    c: Perpendicular(g-3,g9)
    c: Distance(g9) = 8
    c: Coincident(g3,g9)
    c: Coincident(g10,g8)
    c: Parallel(g10,g-3)
    c: Distance(g10) = 2
    c: Coincident(g10,g9)
FEATURE [Part::Extrusion] Extrude058  label="Extrude buco interno per micro switch sinistro"
  Base = -> Sketch055
  Dir = (0,-1,2e-16)
  DirMode = 2
  FaceMakerClass = Part::FaceMakerBullseye
  FaceMakerMode = 3
  LengthFwd = 9
  LengthRev = 0
  Placement = pos=(0,10.6,0) rot=(0,0,1;0rad)
  Solid = true
  Symmetric = false
FEATURE [Sketcher::SketchObject] Sketch056  label="buco esterno per micro switch"
  ArcFitTolerance = 1e-06
  AttachmentSupport = -> [XZ_Plane]
  ExternalGeometry = -> [Sketch055]
  FullyConstrained = true
  MakeInternals = false
  MapMode = 5
  Placement = pos=(0,0,0) rot=(1,0,0;1.5708rad)
  sketch-geometry (17):
    g0: GeomPoint [constr] X=-194.143 Y=29.3727 Z=0
    g1: GeomPoint [constr] X=-194.483 Y=34.2854 Z=0
    g2: GeomPoint [constr] X=-197.902 Y=30.7408 Z=0
    g3: GeomPoint [constr] X=-197.561 Y=25.8282 Z=0
    g4: GeomPoint [constr] X=-196.022 Y=30.0568 Z=0
    g5: LineSegment [constr] StartX=-194.483 StartY=34.2854 StartZ=0 EndX=-196.022 EndY=30.0568 EndZ=0
    g6: LineSegment [constr] StartX=-196.022 StartY=30.0568 StartZ=0 EndX=-197.561 EndY=25.8282 EndZ=0
    g7: LineSegment [constr] StartX=-197.902 StartY=30.7408 StartZ=0 EndX=-196.022 EndY=30.0568 EndZ=0
    g8: LineSegment [constr] StartX=-196.022 StartY=30.0568 StartZ=0 EndX=-194.143 EndY=29.3727 EndZ=0
    g9: LineSegment [constr] StartX=-195.338 StartY=31.9362 StartZ=0 EndX=-196.022 EndY=30.0568 EndZ=0
    g10: LineSegment [constr] StartX=-196.022 StartY=30.0568 StartZ=0 EndX=-196.706 EndY=28.1774 EndZ=0
    g11: LineSegment [constr] StartX=-196.022 StartY=30.0568 StartZ=0 EndX=-196.821 EndY=30.3475 EndZ=0
    g12: LineSegment [constr] StartX=-196.022 StartY=30.0568 StartZ=0 EndX=-195.223 EndY=29.7661 EndZ=0
    g13: LineSegment StartX=-194.539 StartY=31.6454 StartZ=0 EndX=-195.907 EndY=27.8867 EndZ=0
    g14: LineSegment StartX=-196.137 StartY=32.2269 StartZ=0 EndX=-197.505 EndY=28.4681 EndZ=0
    g15: LineSegment StartX=-196.137 StartY=32.2269 StartZ=0 EndX=-194.539 EndY=31.6454 EndZ=0
    g16: LineSegment StartX=-197.505 StartY=28.4681 StartZ=0 EndX=-195.907 EndY=27.8867 EndZ=0
  constraints (34):
    c: Symmetric(g-5,g-5,g1)
    c: Symmetric(g-5,g-6,g0)
    c: Symmetric(g-6,g-6,g3)
    c: Symmetric(g-5,g-6,g2)
    c: Coincident(g5,g1)
    c: Coincident(g5,g4)
    c: Coincident(g6,g4)
    c: Coincident(g6,g3)
    c: Equal(g5,g6)
    c: Coincident(g7,g2)
    c: Coincident(g7,g4)
    c: Coincident(g8,g4)
    c: Coincident(g8,g0)
    c: Equal(g7,g8)
    c: Coincident(g11,g9)
    c: Coincident(g12,g9)
    c: Tangent(g10,g9) = -1.5708
    c: Perpendicular(g11,g9)
    c: Parallel(g9,g-4)
    c: Equal(g9,g10)
    c: Parallel(g12,g11)
    c: Equal(g11,g12)
    c: Distance(g11,g12) = 1.7
    c: Distance(g9,g10) = 4
    c: Symmetric(g13,g13,g12)
    c: Parallel(g13,g9)
    c: Symmetric(g14,g14,g11)
    c: Symmetric(g15,g15,g9)
    c: Parallel(g15,g11)
    c: Symmetric(g16,g16,g10)
    c: Coincident(g16,g14)
    c: Coincident(g15,g14)
    c: Coincident(g13,g15)
    c: Coincident(g9,g4)
FEATURE [Part::Extrusion] Extrude059  label="Extrude buco esterno per micro switch sinistro"
  Base = -> Sketch056
  Dir = (0,-1,2e-16)
  DirMode = 2
  FaceMakerClass = Part::FaceMakerBullseye
  FaceMakerMode = 3
  LengthFwd = 2
  LengthRev = 0
  Placement = pos=(0,12.6,0) rot=(0,0,1;0rad)
  Solid = true
  Symmetric = false
FEATURE [Sketcher::SketchObject] Sketch057  label="buco interno per SWITCH"
  ArcFitTolerance = 1e-06
  AttachmentSupport = -> [XZ_Plane]
  ExternalGeometry = -> [Sketch]
  FullyConstrained = true
  MakeInternals = false
  MapMode = 5
  Placement = pos=(0,0,0) rot=(1,0,0;1.5708rad)
  sketch-geometry (10):
    g0: GeomPoint [constr] X=-187.821 Y=29.2 Z=0
    g1: LineSegment [constr] StartX=-188.505 StartY=27.3206 StartZ=0 EndX=-193.203 EndY=29.0307 EndZ=0
    g2: LineSegment [constr] StartX=-190.809 StartY=35.6086 StartZ=0 EndX=-195.597 EndY=22.4529 EndZ=0
    g3: GeomPoint [constr] X=-193.203 Y=29.0307 Z=0
    g4: LineSegment [constr] StartX=-196.492 StartY=30.2278 StartZ=0 EndX=-189.914 EndY=27.8336 EndZ=0
    g5: LineSegment StartX=-194.098 StartY=36.8056 StartZ=0 EndX=-187.52 EndY=34.4115 EndZ=0
    g6: LineSegment StartX=-194.098 StartY=36.8056 StartZ=0 EndX=-198.886 EndY=23.6499 EndZ=0
    g7: LineSegment StartX=-187.52 StartY=34.4115 StartZ=0 EndX=-192.308 EndY=21.2558 EndZ=0
    g8: LineSegment StartX=-198.886 StartY=23.6499 StartZ=0 EndX=-192.308 EndY=21.2558 EndZ=0
    g9: LineSegment [constr] StartX=-187.821 StartY=29.2 StartZ=0 EndX=-188.505 EndY=27.3206 EndZ=0
  constraints (23):
    c: Symmetric(g-3,g-3,g0)
    c: Perpendicular(g1,g-3)
    c: Parallel(g2,g-3)
    c: Symmetric(g2,g2,g3)
    c: Perpendicular(g2,g4)
    c: Symmetric(g4,g4,g3)
    c: Distance(g2) = 14
    c: Distance(g4) = 7
    c: Distance(g1) = 5
    c: Parallel(g5,g4)
    c: Parallel(g7,g2)
    c: Symmetric(g5,g5,g2)
    c: Symmetric(g6,g6,g4)
    c: Symmetric(g7,g7,g4)
    c: Symmetric(g8,g8,g2)
    c: Coincident(g6,g5)
    c: Coincident(g7,g5)
    c: Coincident(g8,g7)
    c: Coincident(g3,g1)
    c: Coincident(g9,g0)
    c: Parallel(g9,g-3)
    c: Distance(g9) = 2
    c: Coincident(g1,g9)
FEATURE [Sketcher::SketchObject] Sketch058  label="buco esterno per SWITCH"
  ArcFitTolerance = 1e-06
  AttachmentSupport = -> [XZ_Plane]
  ExternalGeometry = -> [Sketch057]
  FullyConstrained = true
  MakeInternals = false
  MapMode = 5
  Placement = pos=(0,0,0) rot=(1,0,0;1.5708rad)
  sketch-geometry (12):
    g0: GeomPoint [constr] X=-190.809 Y=35.6086 Z=0
    g1: GeomPoint [constr] X=-196.492 Y=30.2278 Z=0
    g2: GeomPoint [constr] X=-189.914 Y=27.8336 Z=0
    g3: GeomPoint [constr] X=-195.597 Y=22.4529 Z=0
    g4: GeomPoint [constr] X=-193.203 Y=29.0307 Z=0
    g5: LineSegment [constr] StartX=-192.006 StartY=32.3196 StartZ=0 EndX=-194.4 EndY=25.7418 EndZ=0
    g6: GeomPoint [constr] X=-193.203 Y=29.0307 Z=0
    g7: LineSegment [constr] StartX=-195.082 StartY=29.7148 StartZ=0 EndX=-191.324 EndY=28.3467 EndZ=0
    g8: LineSegment StartX=-193.885 StartY=33.0037 StartZ=0 EndX=-190.127 EndY=31.6356 EndZ=0
    g9: LineSegment StartX=-190.127 StartY=31.6356 StartZ=0 EndX=-192.521 EndY=25.0578 EndZ=0
    g10: LineSegment StartX=-196.28 StartY=26.4258 StartZ=0 EndX=-192.521 EndY=25.0578 EndZ=0
    g11: LineSegment StartX=-193.885 StartY=33.0037 StartZ=0 EndX=-196.28 EndY=26.4258 EndZ=0
  constraints (21):
    c: Symmetric(g-6,g-6,g3)
    c: Symmetric(g-4,g-6,g2)
    c: Symmetric(g-5,g-4,g0)
    c: Symmetric(g-5,g-6,g1)
    c: Symmetric(g1,g2,g4)
    c: Parallel(g5,g-4)
    c: Symmetric(g5,g5,g6)
    c: Perpendicular(g7,g5)
    c: Symmetric(g7,g7,g6)
    c: Distance(g5) = 7
    c: Distance(g7) = 4
    c: Parallel(g8,g7)
    c: Parallel(g11,g5)
    c: Symmetric(g8,g8,g5)
    c: Symmetric(g9,g9,g7)
    c: Symmetric(g10,g10,g5)
    c: Symmetric(g11,g11,g7)
    c: Coincident(g11,g8)
    c: Coincident(g9,g8)
    c: Coincident(g9,g10)
    c: Coincident(g6,g4)
FEATURE [Part::Extrusion] Extrude060  label="Extrude buco interno per SWITCH destro"
  Base = -> Sketch057
  Dir = (0,-1,2e-16)
  DirMode = 2
  FaceMakerClass = Part::FaceMakerBullseye
  FaceMakerMode = 3
  LengthFwd = 13.2
  LengthRev = 0
  Placement = pos=(0,2.6,0) rot=(0,0,1;0rad)
  Solid = true
  Symmetric = false
FEATURE [Part::Extrusion] Extrude061  label="Extrude buco esterno per SWITCH destro"
  Base = -> Sketch058
  Dir = (0,-1,2e-16)
  DirMode = 2
  FaceMakerClass = Part::FaceMakerBullseye
  FaceMakerMode = 3
  LengthFwd = 2
  LengthRev = 0
  Placement = pos=(0,-10.6,0) rot=(0,0,1;0rad)
  Solid = true
  Symmetric = false
FEATURE [Sketcher::SketchObject] Sketch059  label="buco per spazio introduzione SWITCH"
  ArcFitTolerance = 1e-06
  AttachmentSupport = -> [XZ_Plane]
  ExternalGeometry = -> [Sketch057,Sketch010]
  FullyConstrained = true
  MakeInternals = false
  MapMode = 5
  Placement = pos=(0,0,0) rot=(1,0,0;1.5708rad)
  sketch-geometry (8):
    g0: LineSegment [constr] StartX=-201.368 StartY=36.3521 StartZ=0 EndX=-195.094 EndY=34.0687 EndZ=0
    g1: LineSegment [constr] StartX=-194.098 StartY=36.8056 StartZ=0 EndX=-195.094 EndY=34.0687 EndZ=0
    g2: LineSegment StartX=-198.658 StartY=24.2771 StartZ=0 EndX=-199.654 EndY=21.5401 EndZ=0
    g3: LineSegment StartX=-199.654 StartY=21.5401 StartZ=0 EndX=-181.196 EndY=14.822 EndZ=0
    g4: LineSegment StartX=-181.196 StartY=14.822 StartZ=0 EndX=-180.2 EndY=17.559 EndZ=0
    g5: LineSegment StartX=-180.2 StartY=17.559 StartZ=0 EndX=-198.658 EndY=24.2771 EndZ=0
    g6: LineSegment [constr] StartX=-204.932 StartY=26.5605 StartZ=0 EndX=-198.658 EndY=24.2771 EndZ=0
    g7: LineSegment [constr] StartX=-198.658 StartY=24.2771 StartZ=0 EndX=-199.654 EndY=21.5401 EndZ=0
  constraints (20):
    c: Parallel(g1,g-3)
    c: Parallel(g0,g-4)
    c: Coincident(g0,g-4)
    c: Coincident(g1,g-3)
    c: Coincident(g0,g1)
    c: Coincident(g3,g2)
    c: Coincident(g4,g3)
    c: Coincident(g5,g4)
    c: Coincident(g5,g2)
    c: Parallel(g5,g-5)
    c: Parallel(g3,g-5)
    c: Parallel(g4,g-6)
    c: DistanceX(g-6,g4) = 0
    c: Coincident(g6,g-5)
    c: Equal(g6,g0)
    c: Coincident(g7,g6)
    c: Equal(g7,g1)
    c: Tangent(g7,g-3)
    c: Coincident(g2,g6)
    c: Coincident(g2,g7)
FEATURE [Part::Extrusion] Extrude062  label="Extrude buco per spazio introduzione SWITCH"
  Base = -> Sketch059
  Dir = (0,-1,2e-16)
  DirMode = 2
  FaceMakerClass = Part::FaceMakerBullseye
  FaceMakerMode = 3
  LengthFwd = 13.2
  LengthRev = 0
  Solid = true
  Symmetric = true
FEATURE [Part::Extrusion] Extrude063  label="Extrude buco interno per SWITCH sinistro"
  Base = -> Sketch057
  Dir = (0,-1,2e-16)
  DirMode = 2
  FaceMakerClass = Part::FaceMakerBullseye
  FaceMakerMode = 3
  LengthFwd = 13.2
  LengthRev = 0
  Placement = pos=(0,10.6,0) rot=(0,0,1;0rad)
  Solid = true
  Symmetric = false
FEATURE [Part::Extrusion] Extrude064  label="Extrude buco esterno per SWITCH sinistro"
  Base = -> Sketch058
  Dir = (0,-1,2e-16)
  DirMode = 2
  FaceMakerClass = Part::FaceMakerBullseye
  FaceMakerMode = 3
  LengthFwd = 2
  LengthRev = 0
  Placement = pos=(0,12.6,0) rot=(0,0,1;0rad)
  Solid = true
  Symmetric = false
FEATURE [Sketcher::SketchObject] Sketch060  label="prova spazio switch"
  ArcFitTolerance = 1e-06
  AttachmentSupport = -> [XY_Plane003]
  FullyConstrained = true
  MakeInternals = false
  MapMode = 5
  sketch-geometry (12):
    g0: LineSegment StartX=-7.5 StartY=10 StartZ=0 EndX=-7.5 EndY=-10 EndZ=0
    g1: LineSegment StartX=-7.5 StartY=-10 StartZ=0 EndX=7.5 EndY=-10 EndZ=0
    g2: LineSegment StartX=7.5 StartY=-10 StartZ=0 EndX=7.5 EndY=10 EndZ=0
    g3: LineSegment StartX=7.5 StartY=10 StartZ=0 EndX=-7.5 EndY=10 EndZ=0
    g4: GeomPoint [constr] X=0 Y=0 Z=0
    g5: LineSegment StartX=-2.95 StartY=-5.55 StartZ=0 EndX=2.95 EndY=-5.55 EndZ=0
    g6: LineSegment StartX=2.95 StartY=-5.55 StartZ=0 EndX=2.95 EndY=5.55 EndZ=0
    g7: LineSegment StartX=2.95 StartY=5.55 StartZ=0 EndX=-2.95 EndY=5.55 EndZ=0
    g8: LineSegment StartX=-2.95 StartY=5.55 StartZ=0 EndX=-2.95 EndY=-5.55 EndZ=0
    g9: GeomPoint [constr] X=0 Y=0 Z=0
    g10: Circle CenterX=0 CenterY=7.75 CenterZ=0 NormalX=0 NormalY=0 NormalZ=1 AngleXU=0 Radius=1.6
    g11: Circle CenterX=0 CenterY=-7.75 CenterZ=0 NormalX=0 NormalY=0 NormalZ=1 AngleXU=0 Radius=1.6
  constraints (29):
    c: Coincident(g0,g1)
    c: Coincident(g1,g2)
    c: Coincident(g2,g3)
    c: Coincident(g3,g0)
    c: Vertical(g0)
    c: Vertical(g2)
    c: Horizontal(g1)
    c: Horizontal(g3)
    c: Symmetric(g2,g0,g4)
    c: Coincident(g4,g-1)
    c: Distance(g3) = 15
    c: Distance(g2) = 20
    c: Coincident(g5,g6)
    c: Coincident(g6,g7)
    c: Coincident(g7,g8)
    c: Coincident(g8,g5)
    c: Horizontal(g5)
    c: Horizontal(g7)
    c: Vertical(g6)
    c: Vertical(g8)
    c: Symmetric(g7,g5,g9)
    c: Coincident(g9,g4)
    c: Distance(g7) = 5.9
    c: Distance(g6) = 11.1
    c: Diameter(g10) = 3.2
    c: Equal(g10,g11)
    c: Symmetric(g10,g11,g-1)
    c: PointOnObject(g10,g-2)
    c: Distance(g10,g11) = 15.5
FEATURE [Part::Extrusion] Extrude065  label="Extrude prova spazio switch"
  Base = -> Sketch060
  Dir = (0,0,1)
  DirMode = 2
  FaceMakerClass = Part::FaceMakerBullseye
  FaceMakerMode = 3
  LengthFwd = 5
  LengthRev = 0
  Solid = true
  Symmetric = false
FEATURE [Sketcher::SketchObject] Sketch061  label="struttura esterna blocco switch"
  ArcFitTolerance = 1e-06
  AttachmentSupport = -> [XZ_Plane003]
  FullyConstrained = true
  MakeInternals = false
  MapMode = 5
  Placement = pos=(0,0,0) rot=(1,0,0;1.5708rad)
  sketch-geometry (5):
    g0: LineSegment StartX=-1 StartY=-5.1 StartZ=0 EndX=1 EndY=-5.1 EndZ=0
    g1: LineSegment StartX=1 StartY=-5.1 StartZ=0 EndX=1 EndY=5.1 EndZ=0
    g2: LineSegment StartX=1 StartY=5.1 StartZ=0 EndX=-1 EndY=5.1 EndZ=0
    g3: LineSegment StartX=-1 StartY=5.1 StartZ=0 EndX=-1 EndY=-5.1 EndZ=0
    g4: GeomPoint [constr] X=0 Y=0 Z=0
  constraints (12):
    c: Coincident(g0,g1)
    c: Coincident(g1,g2)
    c: Coincident(g2,g3)
    c: Coincident(g3,g0)
    c: Horizontal(g0)
    c: Horizontal(g2)
    c: Vertical(g1)
    c: Vertical(g3)
    c: Symmetric(g2,g0,g4)
    c: Distance(g1,g3) = 2
    c: Distance(g0,g2) = 10.2
    c: Coincident(g4,g-1)
FEATURE [Part::Extrusion] Extrude066  label="Extrude struttura esterna blocco switch"
  Base = -> Sketch061
  Dir = (0,-1,2e-16)
  DirMode = 2
  FaceMakerClass = Part::FaceMakerBullseye
  FaceMakerMode = 3
  LengthFwd = 16.8
  LengthRev = 0
  Solid = true
  Symmetric = true
FEATURE [Sketcher::SketchObject] Sketch062  label="struttura interna blocco switch"
  ArcFitTolerance = 1e-06
  AttachmentSupport = -> [XZ_Plane003]
  ExternalGeometry = -> [Sketch061]
  FullyConstrained = true
  MakeInternals = false
  MapMode = 5
  Placement = pos=(0,0,0) rot=(1,0,0;1.5708rad)
  sketch-geometry (5):
    g0: LineSegment StartX=-1 StartY=3.1 StartZ=0 EndX=-1 EndY=-3.1 EndZ=0
    g1: LineSegment StartX=-1 StartY=-3.1 StartZ=0 EndX=1 EndY=-3.1 EndZ=0
    g2: LineSegment StartX=1 StartY=-3.1 StartZ=0 EndX=1 EndY=3.1 EndZ=0
    g3: LineSegment StartX=1 StartY=3.1 StartZ=0 EndX=-1 EndY=3.1 EndZ=0
    g4: GeomPoint [constr] X=0 Y=0 Z=0
  constraints (12):
    c: Coincident(g0,g1)
    c: Coincident(g1,g2)
    c: Coincident(g2,g3)
    c: Coincident(g3,g0)
    c: Vertical(g0)
    c: Vertical(g2)
    c: Horizontal(g1)
    c: Horizontal(g3)
    c: Symmetric(g2,g0,g4)
    c: Coincident(g4,g-1)
    c: Distance(g0) = 6.2
    c: Equal(g3,g-3)
FEATURE [Part::Extrusion] Extrude067  label="Extrude struttura interna blocco switch"
  Base = -> Sketch062
  Dir = (0,-1,2e-16)
  DirMode = 2
  FaceMakerClass = Part::FaceMakerBullseye
  FaceMakerMode = 3
  LengthFwd = 12.8
  LengthRev = 0
  Solid = true
  Symmetric = true
FEATURE [Part::Cut] Cut036  label="struttura blocco switch"
  Base = -> Extrude066
  Refine = true
  Tool = -> Extrude067
FEATURE [Sketcher::SketchObject] Sketch063  label="blocchi tra switch"
  ArcFitTolerance = 1e-06
  AttachmentSupport = -> [XZ_Plane003]
  ExternalGeometry = -> [Sketch061,Sketch062]
  FullyConstrained = true
  MakeInternals = false
  MapMode = 5
  Placement = pos=(0,0,0) rot=(1,0,0;1.5708rad)
  sketch-geometry (8):
    g0: LineSegment StartX=-3 StartY=5.1 StartZ=0 EndX=-1 EndY=5.1 EndZ=0
    g1: LineSegment StartX=-1 StartY=5.1 StartZ=0 EndX=-1 EndY=3.1 EndZ=0
    g2: LineSegment StartX=-1 StartY=3.1 StartZ=0 EndX=-3 EndY=3.1 EndZ=0
    g3: LineSegment StartX=-3 StartY=3.1 StartZ=0 EndX=-3 EndY=5.1 EndZ=0
    g4: LineSegment StartX=-3 StartY=-3.1 StartZ=0 EndX=-1 EndY=-3.1 EndZ=0
    g5: LineSegment StartX=-1 StartY=-3.1 StartZ=0 EndX=-1 EndY=-5.1 EndZ=0
    g6: LineSegment StartX=-1 StartY=-5.1 StartZ=0 EndX=-3 EndY=-5.1 EndZ=0
    g7: LineSegment StartX=-3 StartY=-5.1 StartZ=0 EndX=-3 EndY=-3.1 EndZ=0
  constraints (20):
    c: Horizontal(g0)
    c: Coincident(g1,g0)
    c: Coincident(g2,g1)
    c: Horizontal(g2)
    c: Coincident(g3,g2)
    c: Coincident(g3,g0)
    c: Vertical(g3)
    c: Horizontal(g4)
    c: Coincident(g5,g4)
    c: Coincident(g6,g5)
    c: Horizontal(g6)
    c: Coincident(g7,g6)
    c: Coincident(g7,g4)
    c: Vertical(g7)
    c: Coincident(g0,g-4)
    c: Coincident(g1,g-5)
    c: Coincident(g4,g-6)
    c: Coincident(g5,g-7)
    c: Distance(g0) = 2
    c: Distance(g4) = 2
FEATURE [PartDesign::Body] Body003  label="blocco switch e neopixel"
  AllowCompound = false
  Group = -> [Sketch060,Sketch061,Sketch062,Sketch063]
  Origin = -> Origin003
FEATURE [Part::Extrusion] Extrude068  label="Extrude blocchi tra switch"
  Base = -> Sketch063
  Dir = (0,-1,2e-16)
  DirMode = 2
  FaceMakerClass = Part::FaceMakerBullseye
  FaceMakerMode = 3
  LengthFwd = 7.6
  LengthRev = 0
  Solid = true
  Symmetric = true
FEATURE [Part::MultiFuse] Fusion002  label="Fusion blocco switch"
  Refine = true
  Shapes = -> [Cut036,Extrude068]
FEATURE [Sketcher::SketchObject] Sketch066  label="piano per rampino"
  ArcFitTolerance = 1e-06
  AttachmentSupport = -> [XZ_Plane002]
  ExternalGeometry = -> [Sketch045]
  FullyConstrained = true
  MakeInternals = false
  MapMode = 5
  Placement = pos=(0,0,0) rot=(1,0,0;1.5708rad)
  sketch-geometry (4):
    g0: LineSegment StartX=5.4 StartY=5.1 StartZ=0 EndX=5.4 EndY=3.9 EndZ=0
    g1: LineSegment StartX=5.4 StartY=3.9 StartZ=0 EndX=7 EndY=3.9 EndZ=0
    g2: LineSegment StartX=7 StartY=3.9 StartZ=0 EndX=7 EndY=5.1 EndZ=0
    g3: LineSegment StartX=7 StartY=5.1 StartZ=0 EndX=5.4 EndY=5.1 EndZ=0
  constraints (11):
    c: Coincident(g0,g1)
    c: Coincident(g1,g2)
    c: Coincident(g2,g3)
    c: Coincident(g3,g0)
    c: Vertical(g0)
    c: Vertical(g2)
    c: Horizontal(g1)
    c: Horizontal(g3)
    c: Distance(g0,g2) = 1.6
    c: Distance(g1,g3) = 1.2
    c: Coincident(g2,g-3)
FEATURE [Sketcher::SketchObject] Sketch064  label="rampini_per_serraggio_struttura"
  ArcFitTolerance = 1e-06
  AttachmentSupport = -> [XZ_Plane002]
  ExternalGeometry = -> [Sketch066,Sketch045]
  FullyConstrained = true
  MakeInternals = false
  MapMode = 5
  Placement = pos=(0,0,0) rot=(1,0,0;1.5708rad)
  sketch-geometry (7):
    g0: LineSegment StartX=7 StartY=5.1 StartZ=0 EndX=7 EndY=3.9 EndZ=0
    g1: LineSegment StartX=7 StartY=3.9 StartZ=0 EndX=9 EndY=3.9 EndZ=0
    g2: LineSegment StartX=7 StartY=5.1 StartZ=0 EndX=7 EndY=5.1 EndZ=0
    g3: LineSegment StartX=7 StartY=5.1 StartZ=0 EndX=7 EndY=7.5 EndZ=0
    g4: LineSegment StartX=9 StartY=5.1 StartZ=0 EndX=9 EndY=3.9 EndZ=0
    g5: LineSegment StartX=7 StartY=7.5 StartZ=0 EndX=9 EndY=7.5 EndZ=0
    g6: LineSegment StartX=9 StartY=7.5 StartZ=0 EndX=9 EndY=5.1 EndZ=0
  constraints (20):
    c: Vertical(g0)
    c: Coincident(g1,g0)
    c: Horizontal(g1)
    c: Coincident(g2,g0)
    c: Horizontal(g2)
    c: Coincident(g3,g2)
    c: Vertical(g3)
    c: Coincident(g5,g3)
    c: Coincident(g4,g6)
    c: Coincident(g4,g1)
    c: Vertical(g4)
    c: Coincident(g0,g-3)
    c: DistanceY(g-4,g3) = 2.4
    c: DistanceX(g1,g1) = 2
    c: DistanceY(g2,g6) = 0
    c: DistanceX(g2,g2) = 0
    c: DistanceY(g0,g0) = 1.2
    c: Coincident(g5,g6)
    c: Horizontal(g5)
    c: Vertical(g6)
FEATURE [Part::Extrusion] Extrude070  label="Extrude piano per rampino"
  Base = -> Sketch066
  Dir = (0,-1,2e-16)
  DirMode = 2
  FaceMakerClass = Part::FaceMakerBullseye
  FaceMakerMode = 3
  LengthFwd = 17
  LengthRev = 0
  Solid = true
  Symmetric = true
FEATURE [Part::Extrusion] Extrude071  label="Extrude rampini_per_serraggio_struttura"
  Base = -> Sketch064
  Dir = (0,-1,2e-16)
  DirMode = 2
  FaceMakerClass = Part::FaceMakerBullseye
  FaceMakerMode = 3
  LengthFwd = 5
  LengthRev = 0
  Solid = true
  Symmetric = true
FEATURE [Part::MultiFuse] Fusion003  label="Fusion supporto neopixel completo"
  Refine = true
  Shapes = -> [Fusion001,Extrude070,Extrude071]
FEATURE [Sketcher::SketchObject] Sketch067  label="perno per blocco switch"
  ArcFitTolerance = 1e-06
  AttachmentSupport = -> [XZ_Plane]
  ExternalGeometry = -> [Sketch,Sketch010]
  FullyConstrained = true
  MakeInternals = false
  MapMode = 5
  Placement = pos=(0,0,0) rot=(1,0,0;1.5708rad)
  sketch-geometry (14):
    g0: LineSegment StartX=-191.073 StartY=24.9429 StartZ=0 EndX=-185.81 EndY=23.0276 EndZ=0
    g1: LineSegment StartX=-183.76 StartY=23.9839 StartZ=0 EndX=-182.392 EndY=27.7427 EndZ=0
    g2: LineSegment StartX=-183.348 StartY=29.7934 StartZ=0 EndX=-188.61 EndY=31.7087 EndZ=0
    g3: LineSegment StartX=-188.61 StartY=31.7087 StartZ=0 EndX=-191.073 EndY=24.9429 EndZ=0
    g4: GeomPoint [constr] X=-186.459 Y=27.0946 Z=0
    g5: LineSegment StartX=-189.022 StartY=25.8992 StartZ=0 EndX=-185.263 EndY=24.5311 EndZ=0
    g6: LineSegment StartX=-185.263 StartY=24.5311 StartZ=0 EndX=-183.895 EndY=28.2899 EndZ=0
    g7: LineSegment StartX=-183.895 StartY=28.2899 StartZ=0 EndX=-187.654 EndY=29.658 EndZ=0
    g8: LineSegment StartX=-187.654 StartY=29.658 StartZ=0 EndX=-189.022 EndY=25.8992 EndZ=0
    g9: GeomPoint [constr] X=-186.459 Y=27.0946 Z=0
    g10: ArcOfCircle CenterX=-185.263 CenterY=24.5311 CenterZ=0 NormalX=0 NormalY=0 NormalZ=1 AngleXU=0 Radius=1.6 StartAngle=4.36332 EndAngle=5.93412
    g11: GeomPoint [constr] X=-184.307 Y=22.4804 Z=0
    g12: ArcOfCircle CenterX=-183.895 CenterY=28.2899 CenterZ=0 NormalX=0 NormalY=0 NormalZ=1 AngleXU=0 Radius=1.6 StartAngle=5.93412 EndAngle=7.50492
    g13: GeomPoint [constr] X=-181.844 Y=29.2462 Z=0
  constraints (30):
    c: Coincident(g2,g3)
    c: Coincident(g3,g0)
    c: Symmetric(g13,g0,g4)
    c: Distance(g11,g3) = 7.2
    c: Distance(g0,g2) = 7.2
    c: Parallel(g3,g1)
    c: Parallel(g2,g0)
    c: Perpendicular(g2,g3)
    c: Coincident(g5,g6)
    c: Coincident(g6,g7)
    c: Coincident(g7,g8)
    c: Coincident(g8,g5)
    c: Symmetric(g7,g5,g9)
    c: Distance(g6,g8) = 4
    c: Distance(g5,g7) = 4
    c: Coincident(g9,g4)
    c: Parallel(g8,g6)
    c: Parallel(g7,g5)
    c: Perpendicular(g7,g8)
    c: Tangent(g8,g-3)
    c: Tangent(g2,g-4)
    c: PointOnObject(g11,g1)
    c: PointOnObject(g11,g0)
    c: Tangent(g1,g10) = -1.5708
    c: Tangent(g0,g10) = -1.5708
    c: PointOnObject(g13,g1)
    c: Tangent(g1,g12) = -1.5708
    c: Tangent(g2,g12) = -1.5708
    c: Equal(g10,g12)
    c: Coincident(g10,g5)
FEATURE [Part::Extrusion] Extrude072  label="Extrude perno per blocco switch"
  Base = -> Sketch067
  Dir = (0,-1,2e-16)
  DirMode = 2
  FaceMakerClass = Part::FaceMakerBullseye
  FaceMakerMode = 3
  LengthFwd = 25.2
  LengthRev = 0
  Solid = true
  Symmetric = true
FEATURE [Part::MultiFuse] Fusion
  Refine = true
  Shapes = -> [Extrude,Sweep,Extrude007,Extrude011,Extrude005,Extrude012,Extrude013,Extrude016,Extrude031,Extrude039,Extrude045,Extrude072]
FEATURE [Part::Cut] Cut
  Base = -> Fusion
  Refine = true
  Tool = -> Extrude001
FEATURE [Part::Cut] Cut001
  Base = -> Cut
  Refine = true
  Tool = -> Extrude004
FEATURE [Part::Cut] Cut002
  Base = -> Cut001
  Refine = true
  Tool = -> Extrude006
FEATURE [Part::Cut] Cut003
  Base = -> Cut002
  Refine = true
  Tool = -> Extrude008
FEATURE [Part::Cut] Cut004
  Base = -> Cut003
  Refine = true
  Tool = -> Extrude009
FEATURE [Part::Cut] Cut005
  Base = -> Cut004
  Refine = true
  Tool = -> Extrude010
FEATURE [Part::Cut] Cut006
  Base = -> Cut005
  Refine = true
  Tool = -> Extrude014
FEATURE [Part::Cut] Cut007
  Base = -> Cut006
  Refine = true
  Tool = -> Extrude015
FEATURE [Part::Cut] Cut008
  Base = -> Cut007
  Refine = true
  Tool = -> Extrude018
FEATURE [Part::Cut] Cut009
  Base = -> Cut008
  Refine = true
  Tool = -> Extrude019
FEATURE [Part::Cut] Cut010
  Base = -> Cut009
  Refine = true
  Tool = -> Extrude020
FEATURE [Part::Cut] Cut011
  Base = -> Cut010
  Refine = true
  Tool = -> Extrude021
FEATURE [Part::Cut] Cut012
  Base = -> Cut011
  Refine = true
  Tool = -> Extrude022
FEATURE [Part::Cut] Cut013
  Base = -> Cut012
  Refine = true
  Tool = -> Extrude023
FEATURE [Part::Cut] Cut014
  Base = -> Cut013
  Refine = true
  Tool = -> Extrude032
FEATURE [Part::Cut] Cut015
  Base = -> Cut014
  Refine = true
  Tool = -> Extrude033
FEATURE [Part::Cut] Cut016
  Base = -> Cut015
  Refine = true
  Tool = -> Extrude034
FEATURE [Part::Cut] Cut017
  Base = -> Cut016
  Refine = true
  Tool = -> Extrude035
FEATURE [Part::Cut] Cut018
  Base = -> Cut017
  Refine = true
  Tool = -> Extrude036
FEATURE [Part::Cut] Cut019
  Base = -> Cut018
  Refine = true
  Tool = -> Extrude037
FEATURE [Part::Cut] Cut020
  Base = -> Cut019
  Refine = true
  Tool = -> Extrude030
FEATURE [Part::Cut] Cut022
  Base = -> Cut020
  Refine = true
  Tool = -> Extrude038
FEATURE [Part::Cut] Cut023
  Base = -> Cut022
  Refine = true
  Tool = -> Extrude041
FEATURE [Part::Cut] Cut024
  Base = -> Cut023
  Refine = true
  Tool = -> Extrude040
FEATURE [Part::Cut] Cut025
  Base = -> Cut024
  Refine = true
  Tool = -> Extrude042
FEATURE [Part::Cut] Cut026
  Base = -> Cut025
  Refine = true
  Tool = -> Extrude043
FEATURE [Part::Cut] Cut027
  Base = -> Cut026
  Refine = true
  Tool = -> Extrude044
FEATURE [Part::Cut] Cut028
  Base = -> Cut027
  Refine = true
  Tool = -> Extrude046
FEATURE [Part::Cut] Cut029
  Base = -> Cut028
  Refine = true
  Tool = -> Extrude047
FEATURE [Part::Cut] Cut033
  Base = -> Cut029
  Refine = true
  Tool = -> Extrude055
FEATURE [Part::Cut] Cut034
  Base = -> Cut033
  Refine = true
  Tool = -> Extrude056
FEATURE [Part::Cut] Cut035
  Base = -> Cut034
  Refine = true
  Tool = -> Extrude057
FEATURE [Part::Cut] Cut037
  Base = -> Cut035
  Refine = true
  Tool = -> Extrude060
FEATURE [Part::Cut] Cut038
  Base = -> Cut037
  Refine = true
  Tool = -> Extrude061
FEATURE [Part::Cut] Cut039
  Base = -> Cut038
  Refine = true
  Tool = -> Extrude063
FEATURE [Part::Cut] Cut040
  Base = -> Cut039
  Refine = true
  Tool = -> Extrude064
FEATURE [Part::Cut] Cut041
  Base = -> Cut040
  Refine = true
  Tool = -> Extrude062
FEATURE [Sketcher::SketchObject] Sketch068  label="base con smusso sopra neopixel"
  ArcFitTolerance = 1e-06
  AttachmentSupport = -> [YZ_Plane002]
  FullyConstrained = true
  MakeInternals = false
  MapMode = 5
  Placement = pos=(0,0,0) rot=(0.57735,0.57735,0.57735;2.0944rad)
  sketch-geometry (5):
    g0: LineSegment StartX=-9.5 StartY=-6.1 StartZ=0 EndX=9.5 EndY=-6.1 EndZ=0
    g1: LineSegment StartX=9.5 StartY=-6.1 StartZ=0 EndX=9.5 EndY=6.1 EndZ=0
    g2: LineSegment StartX=9.5 StartY=6.1 StartZ=0 EndX=-9.5 EndY=6.1 EndZ=0
    g3: LineSegment StartX=-9.5 StartY=6.1 StartZ=0 EndX=-9.5 EndY=-6.1 EndZ=0
    g4: GeomPoint [constr] X=0 Y=0 Z=0
  constraints (12):
    c: Coincident(g0,g1)
    c: Coincident(g1,g2)
    c: Coincident(g2,g3)
    c: Coincident(g3,g0)
    c: Horizontal(g0)
    c: Horizontal(g2)
    c: Vertical(g1)
    c: Vertical(g3)
    c: Symmetric(g2,g0,g4)
    c: Distance(g1,g3) = 19
    c: Distance(g0,g2) = 12.2
    c: Coincident(g4,g-1)
FEATURE [PartDesign::Body] Body002  label="supporto per neopixel"
  AllowCompound = false
  Group = -> [Sketch045,Sketch046,Sketch047,Sketch048,Sketch049,Sketch064,Sketch066,Sketch068]
  Origin = -> Origin002
FEATURE [Part::Extrusion] Extrude073  label="Extrude base con smusso sopra neopixel"
  Base = -> Sketch068
  Dir = (1,0,0)
  DirMode = 2
  FaceMakerClass = Part::FaceMakerBullseye
  FaceMakerMode = 3
  LengthFwd = -1
  LengthRev = 0
  Solid = true
  Symmetric = false
FEATURE [Part::Chamfer] Chamfer  label="Chamfer frontale supporto neopixel da fondere al supporto"
  Base = -> Extrude073
  EdgeLinks = -> Extrude073 [Edge4,Edge7,Edge10,Edge12]
  Edges = 4 edges r=0.5: [Edge4,Edge7,Edge10,Edge12]
FEATURE [Sketcher::SketchObject] Sketch069  label="cilindro minore"
  ArcFitTolerance = 1e-06
  AttachmentSupport = -> [XZ_Plane004]
  FullyConstrained = true
  MakeInternals = false
  MapMode = 5
  Placement = pos=(0,0,0) rot=(1,0,0;1.5708rad)
  sketch-geometry (1):
    g0: Circle CenterX=0 CenterY=0 CenterZ=0 NormalX=0 NormalY=0 NormalZ=1 AngleXU=0 Radius=5.8
  constraints (2):
    c: Diameter(g0) = 11.6
    c: Coincident(g0,g-1)
FEATURE [Sketcher::SketchObject] Sketch070  label="cilindro maggiore"
  ArcFitTolerance = 1e-06
  AttachmentSupport = -> [XZ_Plane004]
  ExternalGeometry = -> [Sketch069]
  FullyConstrained = true
  MakeInternals = false
  MapMode = 5
  Placement = pos=(0,0,0) rot=(1,0,0;1.5708rad)
  sketch-geometry (1):
    g0: Circle CenterX=0 CenterY=0 CenterZ=0 NormalX=0 NormalY=0 NormalZ=1 AngleXU=0 Radius=6.5
  constraints (2):
    c: Coincident(g0,g-1)
    c: Diameter(g0) = 13
FEATURE [Sketcher::SketchObject] Sketch071  label="buco interno"
  ArcFitTolerance = 1e-06
  AttachmentSupport = -> [XZ_Plane004]
  ExternalGeometry = -> [Sketch069]
  FullyConstrained = true
  MakeInternals = false
  MapMode = 5
  Placement = pos=(0,0,0) rot=(1,0,0;1.5708rad)
  sketch-geometry (1):
    g0: Circle CenterX=0 CenterY=0 CenterZ=0 NormalX=0 NormalY=0 NormalZ=1 AngleXU=0 Radius=5
  constraints (2):
    c: Coincident(g0,g-1)
    c: Diameter(g0) = 10
FEATURE [PartDesign::Pad] Pad
  Direction = (0,-1,2e-16)
  Length = 1.2
  Length2 = 10
  Placement = pos=(0,0,0) rot=(1,0,0;1.5708rad)
  Profile = -> Sketch070
  ReferenceAxis = -> Sketch070 [N_Axis]
  Refine = true
  Suppressed = false
  Type = 0
FEATURE [PartDesign::Pad] Pad001
  BaseFeature = -> Pad
  Direction = (0,-1,2e-16)
  Length = 5.6
  Length2 = 10
  Placement = pos=(0,0,0) rot=(1,0,0;1.5708rad)
  Profile = -> Sketch069
  ReferenceAxis = -> Sketch069 [N_Axis]
  Refine = true
  Suppressed = false
  Type = 0
FEATURE [PartDesign::Pocket] Pocket
  BaseFeature = -> Pad001
  Direction = (0,1,-2e-16)
  Length = 7
  Length2 = 5
  Midplane = true
  Placement = pos=(0,0,0) rot=(1,0,0;1.5708rad)
  Profile = -> Sketch071
  ReferenceAxis = -> Sketch071 [N_Axis]
  Refine = true
  Suppressed = false
  Type = 0
FEATURE [PartDesign::Fillet] Fillet
  Base = -> Pocket [Face7]
  BaseFeature = -> Pocket
  Placement = pos=(0,0,0) rot=(1,0,0;1.5708rad)
  Radius = 1
  Refine = true
  SupportTransform = false
  Suppressed = false
  UseAllEdges = false
FEATURE [PartDesign::Body] Body004  label="pulsanti lato sinistro"
  AllowCompound = false
  Group = -> [Sketch069,Sketch070,Sketch071,Pad,Pad001,Pocket,Fillet]
  Origin = -> Origin004
  Tip = -> Fillet
FEATURE [Sketcher::SketchObject] Sketch072  label="buco per saldature e diodo driver solenoide"
  ArcFitTolerance = 1e-06
  AttachmentSupport = -> [XZ_Plane]
  ExternalGeometry = -> [Sketch038]
  FullyConstrained = true
  MakeInternals = false
  MapMode = 5
  Placement = pos=(0,0,0) rot=(1,0,0;1.5708rad)
  sketch-geometry (4):
    g0: LineSegment StartX=-209.225 StartY=-40.6939 StartZ=0 EndX=-204.154 EndY=-29.8182 EndZ=0
    g1: LineSegment StartX=-204.154 StartY=-29.8182 StartZ=0 EndX=-206.51 EndY=-28.7194 EndZ=0
    g2: LineSegment StartX=-206.51 StartY=-28.7194 StartZ=0 EndX=-211.582 EndY=-39.5951 EndZ=0
    g3: LineSegment StartX=-211.582 StartY=-39.5951 StartZ=0 EndX=-209.225 EndY=-40.6939 EndZ=0
  constraints (11):
    c: Coincident(g1,g0)
    c: Coincident(g2,g1)
    c: Coincident(g3,g2)
    c: Coincident(g3,g0)
    c: Parallel(g-3,g0)
    c: Parallel(g0,g2)
    c: Perpendicular(g0,g3)
    c: Perpendicular(g1,g0)
    c: Distance(g3) = 2.6
    c: Distance(g2) = 12
    c: Coincident(g0,g-3)
FEATURE [Part::Extrusion] Extrude074  label="Extrude buco per saldature e diodo driver solenoide"
  Base = -> Sketch072
  Dir = (0,-1,2e-16)
  DirMode = 2
  FaceMakerClass = Part::FaceMakerBullseye
  FaceMakerMode = 3
  LengthFwd = 14.6
  LengthRev = 0
  Solid = true
  Symmetric = true
FEATURE [Part::Cut] Cut042
  Base = -> Cut041
  Refine = true
  Tool = -> Extrude074
FEATURE [Sketcher::SketchObject] Sketch073  label="fori slargati blocco solenoide"
  ArcFitTolerance = 1e-06
  AttachmentSupport = -> [XY_Plane]
  ExternalGeometry = -> [Sketch030]
  FullyConstrained = true
  MakeInternals = false
  MapMode = 5
  sketch-geometry (2):
    g0: Circle CenterX=-152.209 CenterY=6.95 CenterZ=0 NormalX=0 NormalY=0 NormalZ=1 AngleXU=0 Radius=3.7
    g1: Circle CenterX=-130.41 CenterY=-6.95 CenterZ=0 NormalX=0 NormalY=0 NormalZ=1 AngleXU=0 Radius=3.7
  constraints (4):
    c: Diameter(g0) = 7.4
    c: Coincident(g0,g-3)
    c: Diameter(g1) = 7.4
    c: Coincident(g1,g-4)
FEATURE [Part::Extrusion] Extrude075  label="Extrude fori slargati blocco solenoide"
  Base = -> Sketch073
  Dir = (0,0,1)
  DirMode = 2
  FaceMakerClass = Part::FaceMakerBullseye
  FaceMakerMode = 3
  LengthFwd = 1.5
  LengthRev = 0
  Placement = pos=(0,0,36.4) rot=(0,0,1;0rad)
  Solid = true
  Symmetric = false
FEATURE [Part::Cut] Cut043
  Base = -> Cut042
  Refine = true
  Tool = -> Extrude075
FEATURE [Sketcher::SketchObject] Sketch074  label="lato sx pistola"
  ArcFitTolerance = 1e-06
  AttachmentSupport = -> [XZ_Plane]
  ExternalGeometry = -> [Sketch016,Sketch,Sketch058]
  FullyConstrained = true
  MakeInternals = false
  MapMode = 5
  Placement = pos=(0,0,0) rot=(1,0,0;1.5708rad)
  sketch-geometry (37):
    g0: LineSegment StartX=-82.8 StartY=3.2 StartZ=0 EndX=0 EndY=3.2 EndZ=0
    g1: LineSegment StartX=-82.8 StartY=3.2 StartZ=0 EndX=-82.8 EndY=6.2 EndZ=0
    g2: LineSegment [constr] StartX=-107.6 StartY=18 StartZ=0 EndX=-107.6 EndY=20 EndZ=0
    g3: LineSegment [constr] StartX=-132.428 StartY=18 StartZ=0 EndX=-132.428 EndY=20 EndZ=0
    g4: LineSegment StartX=-132.428 StartY=20 StartZ=0 EndX=-107.6 EndY=20 EndZ=0
    g5: ArcOfCircle CenterX=-107.6 CenterY=4 CenterZ=0 NormalX=0 NormalY=0 NormalZ=1 AngleXU=0 Radius=16 StartAngle=0.137937 EndAngle=1.5708
    g6: LineSegment StartX=-82.8 StartY=6.2 StartZ=0 EndX=-91.752 EndY=6.2 EndZ=0
    g7: LineSegment [constr] StartX=-145.743 StartY=8.32624 StartZ=0 EndX=-147.645 EndY=8.94427 EndZ=0
    g8: ArcOfCircle CenterX=-132.428 CenterY=4 CenterZ=0 NormalX=0 NormalY=0 NormalZ=1 AngleXU=0 Radius=16 StartAngle=1.5708 EndAngle=2.82743
    g9: LineSegment StartX=-215.932 StartY=-80.4316 StartZ=0 EndX=-176.685 EndY=-80.4316 EndZ=0
    g10: LineSegment StartX=-147.645 StartY=8.94427 StartZ=0 EndX=-176.685 EndY=-80.4316 EndZ=0
    g11: LineSegment [constr] StartX=-193.988 StartY=-2.33927 StartZ=0 EndX=-192.176 EndY=-3.18451 EndZ=0
    g12: LineSegment [constr] StartX=-217.232 StartY=-52.1862 StartZ=0 EndX=-215.42 EndY=-53.0314 EndZ=0
    g13: LineSegment StartX=-192.176 StartY=-3.18451 StartZ=0 EndX=-215.42 EndY=-53.0314 EndZ=0
    g14: ArcOfCircle CenterX=-184.801 CenterY=-67.3089 CenterZ=0 NormalX=0 NormalY=0 NormalZ=1 AngleXU=0 Radius=33.7833 StartAngle=2.70526 EndAngle=3.54053
    g15: ArcOfCircle CenterX=-207.583 CenterY=4 CenterZ=0 NormalX=0 NormalY=0 NormalZ=1 AngleXU=0 Radius=17 StartAngle=5.84685 EndAngle=7.56663
    g16: LineSegment StartX=-202.765 StartY=20.303 StartZ=0 EndX=-195.887 EndY=39.2 EndZ=0
    g17: LineSegment [constr] StartX=-193.885 StartY=33.0037 StartZ=0 EndX=-197.644 EndY=34.3718 EndZ=0
    g18: LineSegment StartX=-195.887 StartY=39.2 StartZ=0 EndX=0 EndY=39.2 EndZ=0
    g19: LineSegment StartX=0 StartY=3.2 StartZ=0 EndX=0 EndY=39.2 EndZ=0
    g20: LineSegment StartX=-189.939 StartY=31.5672 StartZ=0 EndX=-192.333 EndY=24.9893 EndZ=0
    g21: LineSegment StartX=-196.467 StartY=26.4942 StartZ=0 EndX=-194.073 EndY=33.0721 EndZ=0
    g22: Circle CenterX=-213.443 CenterY=-76.8316 CenterZ=0 NormalX=0 NormalY=0 NormalZ=1 AngleXU=0 Radius=1.8
    g23: Circle CenterX=-179.305 CenterY=-76.8316 CenterZ=0 NormalX=0 NormalY=0 NormalZ=1 AngleXU=0 Radius=1.8
    g24: Circle CenterX=-184.08 CenterY=34.8 CenterZ=0 NormalX=0 NormalY=0 NormalZ=1 AngleXU=0 Radius=1.8
    g25: Circle CenterX=-78.51 CenterY=34.8 CenterZ=0 NormalX=0 NormalY=0 NormalZ=1 AngleXU=0 Radius=1.8
    g26: Circle CenterX=-78.51 CenterY=7.6 CenterZ=0 NormalX=0 NormalY=0 NormalZ=1 AngleXU=0 Radius=1.8
    g27: Circle CenterX=-5.6 CenterY=34.8 CenterZ=0 NormalX=0 NormalY=0 NormalZ=1 AngleXU=0 Radius=1.8
    g28: Circle CenterX=-5.6 CenterY=7.6 CenterZ=0 NormalX=0 NormalY=0 NormalZ=1 AngleXU=0 Radius=1.8
    g29: LineSegment StartX=-190.127 StartY=31.6356 StartZ=0 EndX=-189.939 EndY=31.5672 EndZ=0
    g30: LineSegment StartX=-194.073 StartY=33.0721 StartZ=0 EndX=-193.885 EndY=33.0037 EndZ=0
    g31: LineSegment StartX=-193.885 StartY=33.0037 StartZ=0 EndX=-190.127 EndY=31.6356 EndZ=0
    g32: LineSegment StartX=-196.467 StartY=26.4942 StartZ=0 EndX=-192.333 EndY=24.9893 EndZ=0
    g33: Circle CenterX=-19 CenterY=21.2 CenterZ=0 NormalX=0 NormalY=0 NormalZ=1 AngleXU=0 Radius=6.3
    g34: Circle CenterX=-42 CenterY=21.2 CenterZ=0 NormalX=0 NormalY=0 NormalZ=1 AngleXU=0 Radius=6.3
    g35: Circle CenterX=-65 CenterY=21.2 CenterZ=0 NormalX=0 NormalY=0 NormalZ=1 AngleXU=0 Radius=6.3
    g36: LineSegment [constr] StartX=-4 StartY=21.2 StartZ=0 EndX=-65 EndY=21.2 EndZ=0
  constraints (96):
    c: Coincident(g0,g-41)
    c: Horizontal(g0)
    c: PointOnObject(g0,g-39)
    c: Coincident(g1,g0)
    c: Vertical(g1)
    c: DistanceY(g1,g1) = 3
    c: Coincident(g2,g-17)
    c: Vertical(g2)
    c: Coincident(g3,g-16)
    c: Vertical(g3)
    c: DistanceY(g2,g2) = 2
    c: DistanceY(g3,g3) = 2
    c: Coincident(g4,g3)
    c: Coincident(g4,g2)
    c: Coincident(g5,g-17)
    c: Coincident(g5,g2)
    c: Coincident(g6,g1)
    c: Horizontal(g6)
    c: Coincident(g6,g5)
    c: Coincident(g7,g-15)
    c: Coincident(g8,g7)
    c: Coincident(g8,g3)
    c: Coincident(g8,g-15)
    c: Horizontal(g9)
    c: DistanceY(g-13,g9) = 2
    c: Coincident(g10,g7)
    c: Parallel(g10,g-14)
    c: Coincident(g9,g10)
    c: Distance(g11) = 2
    c: Coincident(g11,g-11)
    c: Perpendicular(g-11,g11)
    c: Distance(g12) = 2
    c: Coincident(g12,g-12)
    c: Perpendicular(g-11,g12)
    c: Coincident(g13,g11)
    c: Coincident(g13,g12)
    c: Coincident(g14,g-32)
    c: Coincident(g14,g12)
    c: Coincident(g14,g9)
    c: Coincident(g15,g-10)
    c: Coincident(g15,g11)
    c: Parallel(g16,g-22)
    c: Distance(g17) = 4
    c: PointOnObject(g17,g16)
    c: Coincident(g15,g16)
    c: Horizontal(g18)
    c: Coincident(g18,g16)
    c: Coincident(g19,g0)
    c: PointOnObject(g19,g-39)
    c: DistanceY(g19,g-36) = 2
    c: Coincident(g18,g19)
    c: Diameter(g22) = 3.6
    c: Coincident(g22,g-9)
    c: Diameter(g23) = 3.6
    c: Coincident(g23,g-8)
    c: Diameter(g24) = 3.6
    c: Diameter(g25) = 3.6
    c: Diameter(g26) = 3.6
    c: Diameter(g27) = 3.6
    c: Diameter(g28) = 3.6
    c: Coincident(g27,g-4)
    c: Coincident(g28,g-3)
    c: Coincident(g25,g-6)
    c: Coincident(g26,g-5)
    c: Coincident(g24,g-7)
    c: Parallel(g20,g-21)
    c: Equal(g20,g-21)
    c: Parallel(g21,g-19)
    c: Equal(g21,g-19)
    c: Distance(g29) = 0.2
    c: Distance(g30) = 0.2
    c: Parallel(g29,g-20)
    c: Parallel(g31,g-20)
    c: Equal(g31,g-20)
    c: Coincident(g30,g31)
    c: Coincident(g31,g29)
    c: Coincident(g29,g-21)
    c: Parallel(g30,g31)
    c: Coincident(g17,g30)
    c: Coincident(g20,g29)
    c: Coincident(g21,g30)
    c: Perpendicular(g16,g17)
    c: Coincident(g32,g21)
    c: Coincident(g32,g20)
    c: Perpendicular(g10,g7)
    c: Diameter(g33) = 12.6
    c: Diameter(g34) = 12.6
    c: Diameter(g35) = 12.6
    c: Horizontal(g36)
    c: PointOnObject(g33,g36)
    c: PointOnObject(g34,g36)
    c: DistanceX(g34,g33) = 23
    c: DistanceX(g35,g34) = 23
    c: DistanceX(g33,g36) = 15
    c: Symmetric(g-24,g-24,g36)
    c: Coincident(g36,g35)
FEATURE [Part::Extrusion] Extrude076  label="Extrude lato sx pistola"
  Base = -> Sketch074
  Dir = (0,-1,2e-16)
  DirMode = 2
  FaceMakerClass = Part::FaceMakerBullseye
  FaceMakerMode = 3
  LengthFwd = -2
  LengthRev = 0
  Solid = true
  Symmetric = false
FEATURE [Sketcher::SketchObject] Sketch075  label="lato dx pistola"
  ArcFitTolerance = 1e-06
  AttachmentSupport = -> [XZ_Plane]
  ExternalGeometry = -> [Sketch016,Sketch,Sketch058,Sketch074]
  FullyConstrained = true
  MakeInternals = false
  MapMode = 5
  Placement = pos=(0,0,0) rot=(1,0,0;1.5708rad)
  sketch-geometry (61):
    g0: LineSegment StartX=-82.8 StartY=3.2 StartZ=0 EndX=0 EndY=3.2 EndZ=0
    g1: LineSegment StartX=-82.8 StartY=3.2 StartZ=0 EndX=-82.8 EndY=6.2 EndZ=0
    g2: LineSegment [constr] StartX=-107.6 StartY=18 StartZ=0 EndX=-107.6 EndY=20 EndZ=0
    g3: LineSegment [constr] StartX=-132.428 StartY=18 StartZ=0 EndX=-132.428 EndY=20 EndZ=0
    g4: LineSegment StartX=-132.428 StartY=20 StartZ=0 EndX=-107.6 EndY=20 EndZ=0
    g5: ArcOfCircle CenterX=-107.6 CenterY=4 CenterZ=0 NormalX=0 NormalY=0 NormalZ=1 AngleXU=0 Radius=16 StartAngle=0.137937 EndAngle=1.5708
    g6: LineSegment StartX=-82.8 StartY=6.2 StartZ=0 EndX=-91.752 EndY=6.2 EndZ=0
    g7: LineSegment [constr] StartX=-145.743 StartY=8.32624 StartZ=0 EndX=-147.645 EndY=8.94427 EndZ=0
    g8: ArcOfCircle CenterX=-132.428 CenterY=4 CenterZ=0 NormalX=0 NormalY=0 NormalZ=1 AngleXU=0 Radius=16 StartAngle=1.5708 EndAngle=2.82743
    g9: LineSegment StartX=-215.932 StartY=-80.4316 StartZ=0 EndX=-176.685 EndY=-80.4316 EndZ=0
    g10: LineSegment StartX=-147.645 StartY=8.94427 StartZ=0 EndX=-176.685 EndY=-80.4316 EndZ=0
    g11: LineSegment [constr] StartX=-193.988 StartY=-2.33927 StartZ=0 EndX=-192.176 EndY=-3.18451 EndZ=0
    g12: LineSegment [constr] StartX=-217.232 StartY=-52.1862 StartZ=0 EndX=-215.42 EndY=-53.0314 EndZ=0
    g13: LineSegment StartX=-192.176 StartY=-3.18451 StartZ=0 EndX=-215.42 EndY=-53.0314 EndZ=0
    g14: ArcOfCircle CenterX=-184.801 CenterY=-67.3089 CenterZ=0 NormalX=0 NormalY=0 NormalZ=1 AngleXU=0 Radius=33.7833 StartAngle=2.70526 EndAngle=3.54053
    g15: ArcOfCircle CenterX=-207.583 CenterY=4 CenterZ=0 NormalX=0 NormalY=0 NormalZ=1 AngleXU=0 Radius=17 StartAngle=5.84685 EndAngle=7.56663
    g16: LineSegment StartX=-202.765 StartY=20.303 StartZ=0 EndX=-195.887 EndY=39.2 EndZ=0
    g17: LineSegment [constr] StartX=-193.885 StartY=33.0037 StartZ=0 EndX=-197.644 EndY=34.3718 EndZ=0
    g18: LineSegment StartX=-195.887 StartY=39.2 StartZ=0 EndX=0 EndY=39.2 EndZ=0
    g19: LineSegment StartX=0 StartY=3.2 StartZ=0 EndX=0 EndY=39.2 EndZ=0
    g20: LineSegment StartX=-189.939 StartY=31.5672 StartZ=0 EndX=-192.333 EndY=24.9893 EndZ=0
    g21: LineSegment StartX=-196.467 StartY=26.4942 StartZ=0 EndX=-194.073 EndY=33.0721 EndZ=0
    g22: Circle CenterX=-213.443 CenterY=-76.8316 CenterZ=0 NormalX=0 NormalY=0 NormalZ=1 AngleXU=0 Radius=1.8
    g23: Circle CenterX=-179.305 CenterY=-76.8316 CenterZ=0 NormalX=0 NormalY=0 NormalZ=1 AngleXU=0 Radius=1.8
    g24: Circle CenterX=-184.08 CenterY=34.8 CenterZ=0 NormalX=0 NormalY=0 NormalZ=1 AngleXU=0 Radius=1.8
    g25: Circle CenterX=-78.51 CenterY=34.8 CenterZ=0 NormalX=0 NormalY=0 NormalZ=1 AngleXU=0 Radius=1.8
    g26: Circle CenterX=-78.51 CenterY=7.6 CenterZ=0 NormalX=0 NormalY=0 NormalZ=1 AngleXU=0 Radius=1.8
    g27: Circle CenterX=-5.6 CenterY=34.8 CenterZ=0 NormalX=0 NormalY=0 NormalZ=1 AngleXU=0 Radius=1.8
    g28: Circle CenterX=-5.6 CenterY=7.6 CenterZ=0 NormalX=0 NormalY=0 NormalZ=1 AngleXU=0 Radius=1.8
    g29: LineSegment StartX=-190.127 StartY=31.6356 StartZ=0 EndX=-189.939 EndY=31.5672 EndZ=0
    g30: LineSegment StartX=-194.073 StartY=33.0721 StartZ=0 EndX=-193.885 EndY=33.0037 EndZ=0
    g31: LineSegment StartX=-193.885 StartY=33.0037 StartZ=0 EndX=-190.127 EndY=31.6356 EndZ=0
    g32: LineSegment StartX=-196.467 StartY=26.4942 StartZ=0 EndX=-192.333 EndY=24.9893 EndZ=0
    g33: LineSegment [constr] StartX=-4 StartY=21.2 StartZ=0 EndX=-87.91 EndY=21.2 EndZ=0
    g34: GeomPoint [constr] X=-4 Y=21.2 Z=0
    g35: LineSegment [constr] StartX=-15.2 StartY=33.7 StartZ=0 EndX=-15.2 EndY=8.7 EndZ=0
    g36: LineSegment [constr] StartX=-15.2 StartY=33.7 StartZ=0 EndX=-56.2 EndY=33.7 EndZ=0
    g37: LineSegment [constr] StartX=-15.2 StartY=8.7 StartZ=0 EndX=-56.2 EndY=8.7 EndZ=0
    g38: LineSegment [constr] StartX=-56.2 StartY=33.7 StartZ=0 EndX=-56.2 EndY=8.7 EndZ=0
    g39: Circle CenterX=-18.6 CenterY=30.3 CenterZ=0 NormalX=0 NormalY=0 NormalZ=1 AngleXU=0 Radius=3.4
    g40: Circle CenterX=-18.6 CenterY=12.1 CenterZ=0 NormalX=0 NormalY=0 NormalZ=1 AngleXU=0 Radius=3.4
    g41: Circle CenterX=-43.2 CenterY=30.3 CenterZ=0 NormalX=0 NormalY=0 NormalZ=1 AngleXU=0 Radius=3.4
    g42: Circle CenterX=-43.2 CenterY=12.1 CenterZ=0 NormalX=0 NormalY=0 NormalZ=1 AngleXU=0 Radius=3.4
    g43: LineSegment [constr] StartX=-4 StartY=21.2 StartZ=0 EndX=-15.2 EndY=21.2 EndZ=0
    g44: LineSegment [constr] StartX=-15.2 StartY=21.2 StartZ=0 EndX=-36.2 EndY=21.2 EndZ=0
    g45: LineSegment [constr] StartX=-41.5 StartY=16.2 StartZ=0 EndX=-30.9 EndY=16.2 EndZ=0
    g46: LineSegment [constr] StartX=-30.9 StartY=16.2 StartZ=0 EndX=-30.9 EndY=26.2 EndZ=0
    g47: LineSegment [constr] StartX=-30.9 StartY=26.2 StartZ=0 EndX=-41.5 EndY=26.2 EndZ=0
    g48: LineSegment [constr] StartX=-41.5 StartY=26.2 StartZ=0 EndX=-41.5 EndY=16.2 EndZ=0
    g49: GeomPoint [constr] X=-36.2 Y=21.2 Z=0
    g50: Circle CenterX=-36.2 CenterY=21.2 CenterZ=0 NormalX=0 NormalY=0 NormalZ=1 AngleXU=0 Radius=2.8
    g51: LineSegment [constr] StartX=-24.2 StartY=26.7 StartZ=0 EndX=-24.2 EndY=15.7 EndZ=0
    g52: Circle CenterX=-24.2 CenterY=26.7 CenterZ=0 NormalX=0 NormalY=0 NormalZ=1 AngleXU=0 Radius=3
    g53: Circle CenterX=-24.2 CenterY=15.7 CenterZ=0 NormalX=0 NormalY=0 NormalZ=1 AngleXU=0 Radius=3
    g54: GeomPoint X=-18.6 Y=30.3 Z=0
    g55: GeomPoint X=-18.6 Y=12.1 Z=0
    g56: GeomPoint X=-43.2 Y=12.1 Z=0
    g57: GeomPoint X=-43.2 Y=30.3 Z=0
    g58: Circle CenterX=-65 CenterY=21.2 CenterZ=0 NormalX=0 NormalY=0 NormalZ=1 AngleXU=0 Radius=1.5
    g59: Circle CenterX=-42 CenterY=21.2 CenterZ=0 NormalX=0 NormalY=0 NormalZ=1 AngleXU=0 Radius=1.5
    g60: Circle CenterX=-19 CenterY=21.2 CenterZ=0 NormalX=0 NormalY=0 NormalZ=1 AngleXU=0 Radius=1.5
  constraints (149):
    c: Coincident(g0,g-41)
    c: Horizontal(g0)
    c: PointOnObject(g0,g-39)
    c: Coincident(g1,g0)
    c: Vertical(g1)
    c: DistanceY(g1,g1) = 3
    c: Coincident(g2,g-17)
    c: Vertical(g2)
    c: Coincident(g3,g-16)
    c: Vertical(g3)
    c: DistanceY(g2,g2) = 2
    c: DistanceY(g3,g3) = 2
    c: Coincident(g4,g3)
    c: Coincident(g4,g2)
    c: Coincident(g5,g-17)
    c: Coincident(g5,g2)
    c: Coincident(g6,g1)
    c: Horizontal(g6)
    c: Coincident(g6,g5)
    c: Coincident(g7,g-15)
    c: Coincident(g8,g7)
    c: Coincident(g8,g3)
    c: Coincident(g8,g-15)
    c: Horizontal(g9)
    c: DistanceY(g-13,g9) = 2
    c: Coincident(g10,g7)
    c: Parallel(g10,g-14)
    c: Coincident(g9,g10)
    c: Distance(g11) = 2
    c: Coincident(g11,g-11)
    c: Perpendicular(g-11,g11)
    c: Distance(g12) = 2
    c: Coincident(g12,g-12)
    c: Perpendicular(g-11,g12)
    c: Coincident(g13,g11)
    c: Coincident(g13,g12)
    c: Coincident(g14,g-32)
    c: Coincident(g14,g12)
    c: Coincident(g14,g9)
    c: Coincident(g15,g-10)
    c: Coincident(g15,g11)
    c: Parallel(g16,g-22)
    c: Distance(g17) = 4
    c: PointOnObject(g17,g16)
    c: Coincident(g15,g16)
    c: Horizontal(g18)
    c: Coincident(g18,g16)
    c: Coincident(g19,g0)
    c: PointOnObject(g19,g-39)
    c: DistanceY(g19,g-36) = 2
    c: Coincident(g18,g19)
    c: Diameter(g22) = 3.6
    c: Coincident(g22,g-9)
    c: Diameter(g23) = 3.6
    c: Coincident(g23,g-8)
    c: Diameter(g24) = 3.6
    c: Diameter(g25) = 3.6
    c: Diameter(g26) = 3.6
    c: Diameter(g27) = 3.6
    c: Diameter(g28) = 3.6
    c: Coincident(g27,g-4)
    c: Coincident(g28,g-3)
    c: Coincident(g25,g-6)
    c: Coincident(g26,g-5)
    c: Coincident(g24,g-7)
    c: Parallel(g20,g-21)
    c: Equal(g20,g-21)
    c: Parallel(g21,g-19)
    c: Equal(g21,g-19)
    c: Distance(g29) = 0.2
    c: Distance(g30) = 0.2
    c: Parallel(g29,g-20)
    c: Parallel(g31,g-20)
    c: Equal(g31,g-20)
    c: Coincident(g30,g31)
    c: Coincident(g31,g29)
    c: Coincident(g29,g-21)
    c: Parallel(g30,g31)
    c: Coincident(g17,g30)
    c: Coincident(g20,g29)
    c: Coincident(g21,g30)
    c: Perpendicular(g16,g17)
    c: Coincident(g32,g21)
    c: Coincident(g32,g20)
    c: Perpendicular(g10,g7)
    c: Horizontal(g33)
    c: Symmetric(g-24,g-24,g33)
    c: PointOnObject(g33,g-28)
    c: Symmetric(g-24,g-24,g34)
    c: DistanceY(g35,g35) = 25
    c: Symmetric(g35,g35,g33)
    c: Distance(g36) = 41
    c: Coincident(g36,g35)
    c: Horizontal(g36)
    c: Coincident(g37,g35)
    c: Horizontal(g37)
    c: Coincident(g38,g36)
    c: Vertical(g38)
    c: Coincident(g37,g38)
    c: Diameter(g39) = 6.8
    c: Diameter(g40) = 6.8
    c: Tangent(g39,g36)
    c: Tangent(g40,g37)
    c: Tangent(g39,g35)
    c: Tangent(g40,g35)
    c: Diameter(g41) = 6.8
    c: Diameter(g42) = 6.8
    c: Tangent(g41,g36)
    c: Tangent(g42,g37)
    c: DistanceX(g41,g39) = 24.6
    c: DistanceX(g42,g40) = 24.6
    c: Distance(g43) = 11.2
    c: Coincident(g43,g33)
    c: PointOnObject(g43,g33)
    c: PointOnObject(g43,g35)
    c: Distance(g44) = 21
    c: Coincident(g44,g43)
    c: PointOnObject(g44,g33)
    c: Coincident(g45,g46)
    c: Coincident(g46,g47)
    c: Coincident(g47,g48)
    c: Coincident(g48,g45)
    c: Horizontal(g45)
    c: Horizontal(g47)
    c: Vertical(g46)
    c: Vertical(g48)
    c: Symmetric(g47,g45,g49)
    c: Distance(g46,g48) = 10.6
    c: Distance(g45,g47) = 10
    c: Coincident(g49,g44)
    c: Diameter(g50) = 5.6
    c: Coincident(g50,g44)
    c: Distance(g51) = 11
    c: Symmetric(g51,g51,g33)
    c: DistanceX(g51,g43) = 9
    c: Diameter(g52) = 6
    c: Coincident(g52,g51)
    c: Diameter(g53) = 6
    c: Coincident(g53,g51)
    c: Coincident(g40,g55)
    c: Coincident(g39,g54)
    c: Coincident(g41,g57)
    c: Coincident(g42,g56)
    c: Diameter(g58) = 3
    c: Diameter(g59) = 3
    c: Diameter(g60) = 3
    c: Coincident(g58,g-44)
    c: Coincident(g59,g-46)
    c: Coincident(g60,g-45)
FEATURE [Sketcher::SketchObject] Sketch076  label="lato sx pistola - scavi pulsanti"
  ArcFitTolerance = 1e-06
  AttachmentSupport = -> [XZ_Plane]
  ExternalGeometry = -> [Sketch074]
  FullyConstrained = true
  MakeInternals = false
  MapMode = 5
  Placement = pos=(0,0,0) rot=(1,0,0;1.5708rad)
  sketch-geometry (3):
    g0: Circle CenterX=-65 CenterY=21.2 CenterZ=0 NormalX=0 NormalY=0 NormalZ=1 AngleXU=0 Radius=7.3
    g1: Circle CenterX=-42 CenterY=21.2 CenterZ=0 NormalX=0 NormalY=0 NormalZ=1 AngleXU=0 Radius=7.3
    g2: Circle CenterX=-19 CenterY=21.2 CenterZ=0 NormalX=0 NormalY=0 NormalZ=1 AngleXU=0 Radius=7.3
  constraints (6):
    c: Diameter(g0) = 14.6
    c: Diameter(g1) = 14.6
    c: Diameter(g2) = 14.6
    c: Coincident(g0,g-3)
    c: Coincident(g1,g-4)
    c: Coincident(g2,g-5)
FEATURE [Part::Extrusion] Extrude077  label="Extrude lato sx pistola - scavi pulsanti"
  Base = -> Sketch076
  Dir = (0,-1,2e-16)
  DirMode = 2
  FaceMakerClass = Part::FaceMakerBullseye
  FaceMakerMode = 3
  LengthFwd = -1.2
  LengthRev = 0
  Solid = true
  Symmetric = false
FEATURE [Part::Cut] Cut044
  Base = -> Extrude076
  Refine = true
  Tool = -> Extrude077
FEATURE [Part::Extrusion] Extrude078  label="Extrude lato dx pistola"
  Base = -> Sketch075
  Dir = (0,-1,2e-16)
  DirMode = 2
  FaceMakerClass = Part::FaceMakerBullseye
  FaceMakerMode = 3
  LengthFwd = 2
  LengthRev = 0
  Solid = true
  Symmetric = false
FEATURE [Sketcher::SketchObject] Sketch077  label="lato dx pistola - scavi pulsanti"
  ArcFitTolerance = 1e-06
  AttachmentSupport = -> [XZ_Plane]
  ExternalGeometry = -> [Sketch075]
  FullyConstrained = true
  MakeInternals = false
  MapMode = 5
  Placement = pos=(0,0,0) rot=(1,0,0;1.5708rad)
  sketch-geometry (4):
    g0: LineSegment StartX=-27.2 StartY=26.7 StartZ=0 EndX=-27.2 EndY=15.7 EndZ=0
    g1: LineSegment StartX=-21.2 StartY=26.7 StartZ=0 EndX=-21.2 EndY=15.7 EndZ=0
    g2: ArcOfCircle CenterX=-24.2 CenterY=26.7 CenterZ=0 NormalX=0 NormalY=0 NormalZ=1 AngleXU=0 Radius=3 StartAngle=5.96642e-06 EndAngle=3.14159
    g3: ArcOfCircle CenterX=-24.2 CenterY=15.7 CenterZ=0 NormalX=0 NormalY=0 NormalZ=1 AngleXU=0 Radius=3 StartAngle=3.14159 EndAngle=6.28319
  constraints (10):
    c: Vertical(g0)
    c: Coincident(g2,g-3)
    c: Vertical(g1)
    c: Coincident(g3,g-4)
    c: Tangent(g1,g-3)
    c: Tangent(g0,g-3)
    c: Tangent(g3,g0) = -1.5708
    c: Coincident(g3,g1)
    c: Tangent(g0,g2) = -1.5708
    c: Coincident(g1,g2)
FEATURE [Part::Extrusion] Extrude079  label="Extrude lato dx pistola - scavi pulsanti"
  Base = -> Sketch077
  Dir = (0,-1,2e-16)
  DirMode = 2
  FaceMakerClass = Part::FaceMakerBullseye
  FaceMakerMode = 3
  LengthFwd = 1.2
  LengthRev = 0
  Solid = true
  Symmetric = false
FEATURE [Part::Cut] Cut045
  Base = -> Extrude078
  Refine = true
  Tool = -> Extrude079
FEATURE [Sketcher::SketchObject] Sketch078
  ArcFitTolerance = 1e-06
  AttachmentSupport = -> [XZ_Plane005]
  FullyConstrained = true
  MakeInternals = false
  MapMode = 5
  Placement = pos=(0,0,0) rot=(1,0,0;1.5708rad)
  sketch-geometry (5):
    g0: LineSegment [constr] StartX=0 StartY=5.5 StartZ=0 EndX=0 EndY=-5.5 EndZ=0
    g1: ArcOfCircle CenterX=0 CenterY=5.5 CenterZ=0 NormalX=0 NormalY=0 NormalZ=1 AngleXU=0 Radius=2.7 StartAngle=0 EndAngle=3.14159
    g2: ArcOfCircle CenterX=0 CenterY=-5.5 CenterZ=0 NormalX=0 NormalY=0 NormalZ=1 AngleXU=0 Radius=2.7 StartAngle=3.1416 EndAngle=6.28318
    g3: LineSegment StartX=-2.7 StartY=5.5 StartZ=0 EndX=-2.7 EndY=-5.50001 EndZ=0
    g4: LineSegment StartX=2.7 StartY=5.5 StartZ=0 EndX=2.7 EndY=-5.50001 EndZ=0
  constraints (13):
    c: Distance(g0) = 11
    c: Vertical(g0)
    c: Symmetric(g0,g0,g-1)
    c: Radius(g1) = 2.7
    c: Coincident(g1,g0)
    c: Radius(g2) = 2.7
    c: Coincident(g2,g0)
    c: Vertical(g3)
    c: Vertical(g4)
    c: Coincident(g2,g4)
    c: Coincident(g2,g3)
    c: Tangent(g3,g1) = -1.5708
    c: Tangent(g4,g1) = 1.5708
FEATURE [PartDesign::Pad] Pad002
  Direction = (0,-1,2e-16)
  Length = 0.8
  Length2 = 10
  Placement = pos=(0,0,0) rot=(1,0,0;1.5708rad)
  Profile = -> Sketch078
  ReferenceAxis = -> Sketch078 [N_Axis]
  Refine = true
  Suppressed = false
  Type = 0
FEATURE [Sketcher::SketchObject] Sketch079
  ArcFitTolerance = 1e-06
  AttachmentSupport = -> [XZ_Plane005]
  ExternalGeometry = -> [Sketch078]
  FullyConstrained = true
  MakeInternals = false
  MapMode = 5
  Placement = pos=(0,0,0) rot=(1,0,0;1.5708rad)
  sketch-geometry (2):
    g0: Circle CenterX=-1e-16 CenterY=5.5 CenterZ=0 NormalX=0 NormalY=0 NormalZ=1 AngleXU=0 Radius=2.7
    g1: Circle CenterX=0 CenterY=-5.5 CenterZ=0 NormalX=0 NormalY=0 NormalZ=1 AngleXU=0 Radius=2.7
  constraints (4):
    c: Coincident(g0,g-3)
    c: PointOnObject(g-3,g0)
    c: Coincident(g1,g-4)
    c: Equal(g1,g-4)
FEATURE [PartDesign::Pad] Pad003
  BaseFeature = -> Pad002
  Direction = (0,-1,2e-16)
  Length = 5
  Length2 = 10
  Placement = pos=(0,0,0) rot=(1,0,0;1.5708rad)
  Profile = -> Sketch079
  ReferenceAxis = -> Sketch079 [N_Axis]
  Refine = true
  Suppressed = false
  Type = 0
FEATURE [PartDesign::Fillet] Fillet001
  Base = -> Pad003 [Edge16,Edge14]
  BaseFeature = -> Pad003
  Placement = pos=(0,0,0) rot=(1,0,0;1.5708rad)
  Radius = 0.4
  Refine = true
  SupportTransform = false
  Suppressed = false
  UseAllEdges = false
FEATURE [PartDesign::Body] Body005  label="pulsanti lato destro"
  AllowCompound = false
  Group = -> [Sketch078,Pad002,Sketch079,Pad003,Fillet001]
  Origin = -> Origin005
  Tip = -> Fillet001
FEATURE [Sketcher::SketchObject] Sketch080  label="lato dx pistola - fori per inserto M3 x 3 x 4.5"
  ArcFitTolerance = 1e-06
  AttachmentSupport = -> [XZ_Plane]
  ExternalGeometry = -> [Sketch075]
  FullyConstrained = true
  MakeInternals = false
  MapMode = 5
  Placement = pos=(0,0,0) rot=(1,0,0;1.5708rad)
  sketch-geometry (4):
    g0: Circle CenterX=-18.6 CenterY=12.1 CenterZ=0 NormalX=0 NormalY=0 NormalZ=1 AngleXU=0 Radius=2.25
    g1: Circle CenterX=-18.6 CenterY=30.3 CenterZ=0 NormalX=0 NormalY=0 NormalZ=1 AngleXU=0 Radius=2.25
    g2: Circle CenterX=-43.2 CenterY=30.3 CenterZ=0 NormalX=0 NormalY=0 NormalZ=1 AngleXU=0 Radius=2.25
    g3: Circle CenterX=-43.2 CenterY=12.1 CenterZ=0 NormalX=0 NormalY=0 NormalZ=1 AngleXU=0 Radius=2.25
  constraints (8):
    c: Diameter(g0) = 4.5
    c: Coincident(g0,g-5)
    c: Diameter(g1) = 4.5
    c: Coincident(g1,g-4)
    c: Diameter(g2) = 4.5
    c: Coincident(g2,g-3)
    c: Diameter(g3) = 4.5
    c: Coincident(g3,g-6)
FEATURE [Sketcher::SketchObject] Sketch081  label="lato dx pistola - pieno per inserto M3 x 3 x 4,5"
  ArcFitTolerance = 1e-06
  AttachmentSupport = -> [XZ_Plane]
  ExternalGeometry = -> [Sketch075]
  FullyConstrained = true
  MakeInternals = false
  MapMode = 5
  Placement = pos=(0,0,0) rot=(1,0,0;1.5708rad)
  sketch-geometry (4):
    g0: Circle CenterX=-43.2 CenterY=30.3 CenterZ=0 NormalX=0 NormalY=0 NormalZ=1 AngleXU=0 Radius=3.4
    g1: Circle CenterX=-18.6 CenterY=30.3 CenterZ=0 NormalX=0 NormalY=0 NormalZ=1 AngleXU=0 Radius=3.4
    g2: Circle CenterX=-43.2 CenterY=12.1 CenterZ=0 NormalX=0 NormalY=0 NormalZ=1 AngleXU=0 Radius=3.4
    g3: Circle CenterX=-18.6 CenterY=12.1 CenterZ=0 NormalX=0 NormalY=0 NormalZ=1 AngleXU=0 Radius=3.4
  constraints (8):
    c: Diameter(g0) = 6.8
    c: Coincident(g0,g-6)
    c: Diameter(g1) = 6.8
    c: Coincident(g1,g-3)
    c: Diameter(g2) = 6.8
    c: Coincident(g2,g-5)
    c: Diameter(g3) = 6.8
    c: Coincident(g3,g-4)
FEATURE [Part::Extrusion] Extrude080  label="Extrude lato dx pistola - pieno per inserto M3 x 3 x 4,5"
  Base = -> Sketch081
  Dir = (0,-1,2e-16)
  DirMode = 2
  FaceMakerClass = Part::FaceMakerBullseye
  FaceMakerMode = 3
  LengthFwd = -2.4
  LengthRev = 0
  Solid = true
  Symmetric = false
FEATURE [Part::MultiFuse] Fusion004
  Refine = true
  Shapes = -> [Cut045,Extrude080]
FEATURE [Part::Extrusion] Extrude081  label="Extrude lato dx pistola - fori per inserto M3 x 3 x 4.5"
  Base = -> Sketch080
  Dir = (0,-1,2e-16)
  DirMode = 2
  FaceMakerClass = Part::FaceMakerBullseye
  FaceMakerMode = 3
  LengthFwd = 0.6
  LengthRev = 2.4
  Solid = true
  Symmetric = false
FEATURE [Part::Cut] Cut046
  Base = -> Fusion004
  Refine = true
  Tool = -> Extrude081
FEATURE [Sketcher::SketchObject] Sketch082  label="lato sx pistola - disegno anteriore"
  ArcFitTolerance = 1e-06
  AttachmentSupport = -> [XZ_Plane]
  ExternalGeometry = -> [Sketch074]
  FullyConstrained = true
  MakeInternals = false
  MapMode = 5
  Placement = pos=(0,0,0) rot=(1,0,0;1.5708rad)
  sketch-geometry (12):
    g0: ArcOfCircle CenterX=-65 CenterY=21.2 CenterZ=0 NormalX=0 NormalY=0 NormalZ=1 AngleXU=0 Radius=10 StartAngle=1.5708 EndAngle=4.71239
    g1: ArcOfCircle CenterX=-19 CenterY=21.2 CenterZ=0 NormalX=0 NormalY=0 NormalZ=1 AngleXU=0 Radius=10 StartAngle=4.71239 EndAngle=7.85398
    g2: LineSegment StartX=-65 StartY=31.2 StartZ=0 EndX=-19 EndY=31.2 EndZ=0
    g3: LineSegment StartX=-65 StartY=11.2 StartZ=0 EndX=-19 EndY=11.2 EndZ=0
    g4: LineSegment StartX=-82.8 StartY=3.2 StartZ=0 EndX=0 EndY=3.2 EndZ=0
    g5: LineSegment StartX=0 StartY=3.2 StartZ=0 EndX=0 EndY=39.2 EndZ=0
    g6: LineSegment StartX=0 StartY=39.2 StartZ=0 EndX=-82.8 EndY=39.2 EndZ=0
    g7: LineSegment StartX=-82.8 StartY=39.2 StartZ=0 EndX=-82.8 EndY=3.2 EndZ=0
    g8: Circle CenterX=-78.51 CenterY=34.8 CenterZ=0 NormalX=0 NormalY=0 NormalZ=1 AngleXU=0 Radius=1.8
    g9: Circle CenterX=-5.6 CenterY=34.8 CenterZ=0 NormalX=0 NormalY=0 NormalZ=1 AngleXU=0 Radius=1.8
    g10: Circle CenterX=-5.6 CenterY=7.6 CenterZ=0 NormalX=0 NormalY=0 NormalZ=1 AngleXU=0 Radius=1.8
    g11: Circle CenterX=-78.51 CenterY=7.6 CenterZ=0 NormalX=0 NormalY=0 NormalZ=1 AngleXU=0 Radius=1.8
  constraints (26):
    c: Tangent(g0,g2) = 1.5708
    c: Tangent(g0,g3) = -1.5708
    c: Tangent(g1,g2) = 1.5708
    c: Tangent(g1,g3) = -1.5708
    c: Equal(g0,g1)
    c: Coincident(g4,g5)
    c: Coincident(g5,g6)
    c: Coincident(g6,g7)
    c: Coincident(g7,g4)
    c: Horizontal(g4)
    c: Horizontal(g6)
    c: Vertical(g5)
    c: Vertical(g7)
    c: Coincident(g4,g-7)
    c: Coincident(g5,g-9)
    c: Diameter(g1) = 20
    c: Coincident(g1,g-5)
    c: Coincident(g0,g-4)
    c: Equal(g9,g-11)
    c: Equal(g10,g-12)
    c: Equal(g11,g-13)
    c: Equal(g8,g-10)
    c: Coincident(g8,g-10)
    c: Coincident(g11,g-13)
    c: Coincident(g10,g-12)
    c: Coincident(g9,g-11)
FEATURE [Sketcher::SketchObject] Sketch083  label="lato dx pistola - disegno anteriore"
  ArcFitTolerance = 1e-06
  AttachmentSupport = -> [XZ_Plane]
  ExternalGeometry = -> [Sketch082]
  FullyConstrained = true
  MakeInternals = false
  MapMode = 5
  Placement = pos=(0,0,0) rot=(1,0,0;1.5708rad)
  sketch-geometry (12):
    g0: LineSegment StartX=-82.8 StartY=3.2 StartZ=0 EndX=0 EndY=3.2 EndZ=0
    g1: LineSegment StartX=0 StartY=3.2 StartZ=0 EndX=0 EndY=39.2 EndZ=0
    g2: LineSegment StartX=0 StartY=39.2 StartZ=0 EndX=-82.8 EndY=39.2 EndZ=0
    g3: LineSegment StartX=-82.8 StartY=39.2 StartZ=0 EndX=-82.8 EndY=3.2 EndZ=0
    g4: ArcOfCircle CenterX=-65 CenterY=21.2 CenterZ=0 NormalX=0 NormalY=0 NormalZ=1 AngleXU=0 Radius=10 StartAngle=1.5708 EndAngle=4.71239
    g5: ArcOfCircle CenterX=-19 CenterY=21.2 CenterZ=0 NormalX=0 NormalY=0 NormalZ=1 AngleXU=0 Radius=10 StartAngle=4.71239 EndAngle=7.85398
    g6: LineSegment StartX=-65 StartY=31.2 StartZ=0 EndX=-19 EndY=31.2 EndZ=0
    g7: LineSegment StartX=-65 StartY=11.2 StartZ=0 EndX=-19 EndY=11.2 EndZ=0
    g8: Circle CenterX=-78.51 CenterY=34.8 CenterZ=0 NormalX=0 NormalY=0 NormalZ=1 AngleXU=0 Radius=1.8
    g9: Circle CenterX=-5.6 CenterY=34.8 CenterZ=0 NormalX=0 NormalY=0 NormalZ=1 AngleXU=0 Radius=1.8
    g10: Circle CenterX=-5.6 CenterY=7.6 CenterZ=0 NormalX=0 NormalY=0 NormalZ=1 AngleXU=0 Radius=1.8
    g11: Circle CenterX=-78.51 CenterY=7.6 CenterZ=0 NormalX=0 NormalY=0 NormalZ=1 AngleXU=0 Radius=1.8
  constraints (26):
    c: Coincident(g0,g1)
    c: Coincident(g1,g2)
    c: Coincident(g2,g3)
    c: Coincident(g3,g0)
    c: Horizontal(g0)
    c: Horizontal(g2)
    c: Vertical(g1)
    c: Vertical(g3)
    c: Coincident(g0,g-5)
    c: Coincident(g1,g-6)
    c: Tangent(g4,g6) = 1.5708
    c: Tangent(g4,g7) = -1.5708
    c: Tangent(g5,g6) = 1.5708
    c: Tangent(g5,g7) = -1.5708
    c: Equal(g4,g5)
    c: Equal(g5,g-9)
    c: Coincident(g5,g-9)
    c: Coincident(g4,g-8)
    c: Equal(g8,g-11)
    c: Equal(g11,g-12)
    c: Equal(g10,g-13)
    c: Equal(g9,g-14)
    c: Coincident(g9,g-14)
    c: Coincident(g10,g-13)
    c: Coincident(g11,g-12)
    c: Coincident(g8,g-11)
FEATURE [Sketcher::SketchObject] Sketch084  label="lato sx pistola - spazi anteriori per viti"
  ArcFitTolerance = 1e-06
  AttachmentSupport = -> [XZ_Plane]
  ExternalGeometry = -> [Sketch082]
  FullyConstrained = true
  MakeInternals = false
  MapMode = 5
  Placement = pos=(0,0,0) rot=(1,0,0;1.5708rad)
  sketch-geometry (24):
    g0: ArcOfCircle CenterX=-78.51 CenterY=34.8 CenterZ=0 NormalX=0 NormalY=0 NormalZ=1 AngleXU=0 Radius=3.5 StartAngle=4.71239 EndAngle=6.28319
    g1: ArcOfCircle CenterX=-5.6 CenterY=34.8 CenterZ=0 NormalX=0 NormalY=0 NormalZ=1 AngleXU=0 Radius=3.5 StartAngle=3.14159 EndAngle=4.71239
    g2: ArcOfCircle CenterX=-78.51 CenterY=7.6 CenterZ=0 NormalX=0 NormalY=0 NormalZ=1 AngleXU=0 Radius=3.5 StartAngle=3.99598e-11 EndAngle=1.5708
    g3: ArcOfCircle CenterX=-5.6 CenterY=7.6 CenterZ=0 NormalX=0 NormalY=0 NormalZ=1 AngleXU=0 Radius=3.5 StartAngle=1.5708 EndAngle=3.14159
    g4: LineSegment StartX=0 StartY=11.1 StartZ=0 EndX=-5.6 EndY=11.1 EndZ=0
    g5: LineSegment StartX=-9.1 StartY=7.6 StartZ=0 EndX=-9.1 EndY=3.2 EndZ=0
    g6: LineSegment StartX=-75.01 StartY=39.2 StartZ=0 EndX=-75.01 EndY=34.8 EndZ=0
    g7: LineSegment StartX=-82.8 StartY=31.3 StartZ=0 EndX=-78.51 EndY=31.3 EndZ=0
    g8: LineSegment StartX=-82.8 StartY=11.1 StartZ=0 EndX=-78.51 EndY=11.1 EndZ=0
    g9: LineSegment StartX=-75.01 StartY=7.6 StartZ=0 EndX=-75.01 EndY=3.2 EndZ=0
    g10: LineSegment StartX=-9.1 StartY=39.2 StartZ=0 EndX=-9.1 EndY=34.8 EndZ=0
    g11: LineSegment StartX=-5.6 StartY=31.3 StartZ=0 EndX=0 EndY=31.3 EndZ=0
    g12: LineSegment StartX=-9.1 StartY=39.2 StartZ=0 EndX=0 EndY=39.2 EndZ=0
    g13: LineSegment StartX=0 StartY=39.2 StartZ=0 EndX=0 EndY=31.3 EndZ=0
    g14: LineSegment StartX=0 StartY=11.1 StartZ=0 EndX=0 EndY=3.2 EndZ=0
    g15: LineSegment StartX=0 StartY=3.2 StartZ=0 EndX=-9.1 EndY=3.2 EndZ=0
    g16: LineSegment StartX=-75.01 StartY=3.2 StartZ=0 EndX=-82.8 EndY=3.2 EndZ=0
    g17: LineSegment StartX=-82.8 StartY=3.2 StartZ=0 EndX=-82.8 EndY=11.1 EndZ=0
    g18: LineSegment StartX=-82.8 StartY=31.3 StartZ=0 EndX=-82.8 EndY=39.2 EndZ=0
    g19: LineSegment StartX=-82.8 StartY=39.2 StartZ=0 EndX=-75.01 EndY=39.2 EndZ=0
    g20: Circle CenterX=-78.51 CenterY=34.8 CenterZ=0 NormalX=0 NormalY=0 NormalZ=1 AngleXU=0 Radius=1.8
    g21: Circle CenterX=-5.6 CenterY=34.8 CenterZ=0 NormalX=0 NormalY=0 NormalZ=1 AngleXU=0 Radius=1.8
    g22: Circle CenterX=-5.6 CenterY=7.6 CenterZ=0 NormalX=0 NormalY=0 NormalZ=1 AngleXU=0 Radius=1.8
    g23: Circle CenterX=-78.51 CenterY=7.6 CenterZ=0 NormalX=0 NormalY=0 NormalZ=1 AngleXU=0 Radius=1.8
  constraints (56):
    c: Radius(g0) = 3.5
    c: Coincident(g0,g-5)
    c: Radius(g1) = 3.5
    c: Coincident(g1,g-10)
    c: Radius(g2) = 3.5
    c: Coincident(g2,g-4)
    c: Radius(g3) = 3.5
    c: Coincident(g3,g-9)
    c: Horizontal(g4)
    c: Vertical(g5)
    c: Vertical(g6)
    c: Horizontal(g7)
    c: Horizontal(g8)
    c: Vertical(g9)
    c: Vertical(g10)
    c: Horizontal(g11)
    c: Tangent(g11,g1) = -1.5708
    c: Tangent(g1,g10) = -1.5708
    c: Tangent(g3,g5) = -1.5708
    c: Tangent(g3,g4) = -1.5708
    c: Tangent(g9,g2) = 1.5708
    c: Tangent(g8,g2) = 1.5708
    c: Tangent(g7,g0) = -1.5708
    c: Tangent(g0,g6) = 1.5708
    c: PointOnObject(g10,g-7)
    c: PointOnObject(g11,g-11)
    c: PointOnObject(g4,g-11)
    c: PointOnObject(g5,g-8)
    c: PointOnObject(g9,g-8)
    c: PointOnObject(g8,g-6)
    c: PointOnObject(g7,g-6)
    c: PointOnObject(g6,g-7)
    c: Coincident(g12,g10)
    c: Coincident(g12,g-11)
    c: Coincident(g13,g12)
    c: Coincident(g13,g11)
    c: Coincident(g14,g4)
    c: Coincident(g14,g-11)
    c: Coincident(g15,g14)
    c: Coincident(g15,g5)
    c: Coincident(g16,g9)
    c: Coincident(g16,g-8)
    c: Coincident(g17,g16)
    c: Coincident(g17,g8)
    c: Coincident(g18,g7)
    c: Coincident(g18,g-7)
    c: Coincident(g19,g18)
    c: Coincident(g19,g6)
    c: Equal(g21,g-10)
    c: Equal(g-9,g22)
    c: Equal(g23,g-4)
    c: Equal(g20,g-5)
    c: Coincident(g20,g0)
    c: Coincident(g21,g1)
    c: Coincident(g22,g3)
    c: Coincident(g23,g2)
FEATURE [Sketcher::SketchObject] Sketch085  label="lato dx pistola - spazi anteriori per viti"
  ArcFitTolerance = 1e-06
  AttachmentSupport = -> [XZ_Plane]
  ExternalGeometry = -> [Sketch083]
  FullyConstrained = true
  MakeInternals = false
  MapMode = 5
  Placement = pos=(0,0,0) rot=(1,0,0;1.5708rad)
  sketch-geometry (24):
    g0: ArcOfCircle CenterX=-78.51 CenterY=34.8 CenterZ=0 NormalX=0 NormalY=0 NormalZ=1 AngleXU=0 Radius=3.5 StartAngle=4.71239 EndAngle=6.28319
    g1: ArcOfCircle CenterX=-5.6 CenterY=34.8 CenterZ=0 NormalX=0 NormalY=0 NormalZ=1 AngleXU=0 Radius=3.5 StartAngle=3.14159 EndAngle=4.71239
    g2: ArcOfCircle CenterX=-78.51 CenterY=7.6 CenterZ=0 NormalX=0 NormalY=0 NormalZ=1 AngleXU=0 Radius=3.5 StartAngle=3.99599e-11 EndAngle=1.5708
    g3: ArcOfCircle CenterX=-5.6 CenterY=7.6 CenterZ=0 NormalX=0 NormalY=0 NormalZ=1 AngleXU=0 Radius=3.5 StartAngle=1.5708 EndAngle=3.14159
    g4: LineSegment StartX=-9.1 StartY=39.2 StartZ=0 EndX=-9.1 EndY=34.8 EndZ=0
    g5: LineSegment StartX=-5.6 StartY=31.3 StartZ=0 EndX=0 EndY=31.3 EndZ=0
    g6: LineSegment StartX=-5.6 StartY=11.1 StartZ=0 EndX=0 EndY=11.1 EndZ=0
    g7: LineSegment StartX=-9.1 StartY=7.6 StartZ=0 EndX=-9.1 EndY=3.2 EndZ=0
    g8: LineSegment StartX=-82.8 StartY=11.1 StartZ=0 EndX=-78.51 EndY=11.1 EndZ=0
    g9: LineSegment StartX=-75.01 StartY=7.6 StartZ=0 EndX=-75.01 EndY=3.2 EndZ=0
    g10: LineSegment StartX=-82.8 StartY=31.3 StartZ=0 EndX=-78.51 EndY=31.3 EndZ=0
    g11: LineSegment StartX=-75.01 StartY=34.8 StartZ=0 EndX=-75.01 EndY=39.2 EndZ=0
    g12: LineSegment StartX=-75.01 StartY=3.2 StartZ=0 EndX=-82.8 EndY=3.2 EndZ=0
    g13: LineSegment StartX=-82.8 StartY=3.2 StartZ=0 EndX=-82.8 EndY=11.1 EndZ=0
    g14: LineSegment StartX=-82.8 StartY=31.3 StartZ=0 EndX=-82.8 EndY=39.2 EndZ=0
    g15: LineSegment StartX=-82.8 StartY=39.2 StartZ=0 EndX=-75.01 EndY=39.2 EndZ=0
    g16: LineSegment StartX=-9.1 StartY=39.2 StartZ=0 EndX=0 EndY=39.2 EndZ=0
    g17: LineSegment StartX=0 StartY=39.2 StartZ=0 EndX=0 EndY=31.3 EndZ=0
    g18: LineSegment StartX=-9.1 StartY=3.2 StartZ=0 EndX=0 EndY=3.2 EndZ=0
    g19: LineSegment StartX=0 StartY=3.2 StartZ=0 EndX=0 EndY=11.1 EndZ=0
    g20: Circle CenterX=-78.51 CenterY=34.8 CenterZ=0 NormalX=0 NormalY=0 NormalZ=1 AngleXU=0 Radius=1.8
    g21: Circle CenterX=-5.6 CenterY=34.8 CenterZ=0 NormalX=0 NormalY=0 NormalZ=1 AngleXU=0 Radius=1.8
    g22: Circle CenterX=-5.6 CenterY=7.6 CenterZ=0 NormalX=0 NormalY=0 NormalZ=1 AngleXU=0 Radius=1.8
    g23: Circle CenterX=-78.51 CenterY=7.6 CenterZ=0 NormalX=0 NormalY=0 NormalZ=1 AngleXU=0 Radius=1.8
  constraints (56):
    c: Radius(g0) = 3.5
    c: Coincident(g0,g-3)
    c: Radius(g1) = 3.5
    c: Coincident(g1,g-5)
    c: Radius(g2) = 3.5
    c: Coincident(g2,g-4)
    c: Radius(g3) = 3.5
    c: Coincident(g3,g-6)
    c: Vertical(g4)
    c: Horizontal(g5)
    c: Horizontal(g6)
    c: Vertical(g7)
    c: Horizontal(g8)
    c: Vertical(g9)
    c: Horizontal(g10)
    c: Vertical(g11)
    c: Tangent(g4,g1) = -1.5708
    c: Tangent(g5,g1) = -1.5708
    c: Tangent(g6,g3) = 1.5708
    c: Tangent(g7,g3) = -1.5708
    c: Tangent(g9,g2) = 1.5708
    c: Tangent(g8,g2) = 1.5708
    c: Tangent(g10,g0) = -1.5708
    c: Tangent(g11,g0) = -1.5708
    c: PointOnObject(g11,g-9)
    c: PointOnObject(g4,g-9)
    c: PointOnObject(g5,g-10)
    c: PointOnObject(g6,g-10)
    c: PointOnObject(g7,g-7)
    c: PointOnObject(g9,g-7)
    c: PointOnObject(g8,g-8)
    c: PointOnObject(g10,g-8)
    c: Coincident(g12,g9)
    c: Coincident(g12,g-8)
    c: Coincident(g13,g12)
    c: Coincident(g13,g8)
    c: Coincident(g14,g10)
    c: Coincident(g14,g-9)
    c: Coincident(g15,g14)
    c: Coincident(g15,g11)
    c: Coincident(g16,g4)
    c: Coincident(g16,g-10)
    c: Coincident(g17,g16)
    c: Coincident(g17,g5)
    c: Coincident(g18,g7)
    c: Coincident(g18,g-10)
    c: Coincident(g19,g18)
    c: Coincident(g19,g6)
    c: Equal(g20,g-3)
    c: Equal(g21,g-5)
    c: Equal(g22,g-6)
    c: Equal(g23,g-4)
    c: Coincident(g20,g0)
    c: Coincident(g21,g1)
    c: Coincident(g22,g3)
    c: Coincident(g23,g2)
FEATURE [Part::Extrusion] Extrude082  label="Extrude lato sx pistola - disegno anteriore"
  Base = -> Sketch082
  Dir = (0,-1,2e-16)
  DirMode = 2
  FaceMakerClass = Part::FaceMakerBullseye
  FaceMakerMode = 3
  LengthFwd = -1.6
  LengthRev = 0
  Placement = pos=(0,2,0) rot=(0,0,1;0rad)
  Solid = true
  Symmetric = false
FEATURE [Part::Extrusion] Extrude083  label="Extrude lato dx pistola - disegno anteriore"
  Base = -> Sketch083
  Dir = (0,-1,2e-16)
  DirMode = 2
  FaceMakerClass = Part::FaceMakerBullseye
  FaceMakerMode = 3
  LengthFwd = 1.6
  LengthRev = 0
  Placement = pos=(0,-2,0) rot=(0,0,1;0rad)
  Solid = true
  Symmetric = false
FEATURE [Part::Extrusion] Extrude084  label="Extrude lato sx pistola - spazi anteriori per viti"
  Base = -> Sketch084
  Dir = (0,-1,2e-16)
  DirMode = 2
  FaceMakerClass = Part::FaceMakerBullseye
  FaceMakerMode = 3
  LengthFwd = -1.6
  LengthRev = 0
  Placement = pos=(0,2,0) rot=(0,0,1;0rad)
  Solid = true
  Symmetric = false
FEATURE [Part::Extrusion] Extrude085  label="Extrude lato dx pistola - spazi anteriori per viti"
  Base = -> Sketch085
  Dir = (0,-1,2e-16)
  DirMode = 2
  FaceMakerClass = Part::FaceMakerBullseye
  FaceMakerMode = 3
  LengthFwd = 0.8
  LengthRev = 0
  Placement = pos=(0,-2.8,0) rot=(0,0,1;0rad)
  Solid = true
  Symmetric = false
FEATURE [Part::Cut] Cut048  label="Extrude lato dx pistola - disegno anterioro con fori viti"
  Base = -> Extrude083
  Refine = true
  Tool = -> Extrude085
FEATURE [Part::MultiFuse] Fusion006
  Refine = true
  Shapes = -> [Cut046,Cut048]
FEATURE [Sketcher::SketchObject] Sketch087  label="lato sx pistola - rialzo posteriore"
  ArcFitTolerance = 1e-06
  AttachmentSupport = -> [XZ_Plane]
  ExternalGeometry = -> [Sketch074]
  FullyConstrained = true
  MakeInternals = false
  MapMode = 5
  Placement = pos=(0,0,0) rot=(1,0,0;1.5708rad)
  sketch-geometry (10):
    g0: LineSegment StartX=-181.33 StartY=20.0744 StartZ=0 EndX=-144.029 EndY=20.0744 EndZ=0
    g1: LineSegment StartX=-137.815 StartY=39.2 StartZ=0 EndX=-144.029 EndY=20.0744 EndZ=0
    g2: LineSegment StartX=-178.754 StartY=39.2 StartZ=0 EndX=-137.815 EndY=39.2 EndZ=0
    g3: ArcOfCircle CenterX=-184.08 CenterY=34.8 CenterZ=0 NormalX=0 NormalY=0 NormalZ=1 AngleXU=0 Radius=3.5 StartAngle=4.71239 EndAngle=5.93412
    g4: LineSegment StartX=-178.754 StartY=39.2 StartZ=0 EndX=-180.791 EndY=33.6029 EndZ=0
    g5: GeomPoint [constr] X=-181.33 Y=20.0744 Z=0
    g6: LineSegment [constr] StartX=-181.33 StartY=20.0744 StartZ=0 EndX=-192.176 EndY=-3.18451 EndZ=0
    g7: LineSegment StartX=-184.08 StartY=31.3 StartZ=0 EndX=-186.139 EndY=31.3 EndZ=0
    g8: LineSegment StartX=-186.139 StartY=31.3 StartZ=0 EndX=-190.224 EndY=20.0744 EndZ=0
    g9: LineSegment StartX=-181.33 StartY=20.0744 StartZ=0 EndX=-190.224 EndY=20.0744 EndZ=0
  constraints (23):
    c: Horizontal(g0)
    c: Tangent(g1,g-5)
    c: PointOnObject(g2,g-4)
    c: Coincident(g2,g1)
    c: Radius(g3) = 3.5
    c: Coincident(g3,g-10)
    c: Horizontal(g2)
    c: Equal(g1,g-3)
    c: Coincident(g0,g1)
    c: Tangent(g4,g3) = 1.5708
    c: Coincident(g4,g2)
    c: Coincident(g6,g5)
    c: Tangent(g6,g-11) = -1.5708
    c: Coincident(g0,g5)
    c: Parallel(g4,g-3)
    c: Horizontal(g7)
    c: Parallel(g8,g-3)
    c: Tangent(g3,g7) = 1.5708
    c: Coincident(g8,g7)
    c: Coincident(g9,g0)
    c: Horizontal(g9)
    c: Coincident(g9,g8)
    c: DistanceX(g-8,g7) = 3.8
FEATURE [Sketcher::SketchObject] Sketch086  label="lato sx pistola - rialzo centrale"
  ArcFitTolerance = 1e-06
  AttachmentOffset = pos=(0,2,0) rot=(0,0,1;0rad)
  AttachmentSupport = -> [XZ_Plane]
  ExternalGeometry = -> [Sketch074,Sketch087]
  FullyConstrained = true
  MakeInternals = false
  MapMode = 5
  Placement = pos=(0,4e-16,2) rot=(1,0,0;1.5708rad)
  sketch-geometry (6):
    g0: LineSegment StartX=-137.815 StartY=37.2 StartZ=0 EndX=-142.793 EndY=21.8787 EndZ=0
    g1: LineSegment StartX=-137.815 StartY=37.2 StartZ=0 EndX=-110.815 EndY=37.2 EndZ=0
    g2: LineSegment StartX=-110.815 StartY=37.2 StartZ=0 EndX=-112.201 EndY=32.9344 EndZ=0
    g3: LineSegment StartX=-127.418 StartY=21.8787 StartZ=0 EndX=-142.793 EndY=21.8787 EndZ=0
    g4: ArcOfCircle CenterX=-127.418 CenterY=37.8787 CenterZ=0 NormalX=0 NormalY=0 NormalZ=1 AngleXU=0 Radius=16 StartAngle=4.71239 EndAngle=5.96903
    g5: GeomPoint [constr] X=-115.793 Y=21.8787 Z=0
  constraints (15):
    c: Distance(g1) = 27
    c: Coincident(g1,g0)
    c: PointOnObject(g1,g-4)
    c: Parallel(g2,g-3)
    c: Coincident(g2,g1)
    c: Horizontal(g3)
    c: PointOnObject(g5,g2)
    c: PointOnObject(g5,g3)
    c: Tangent(g2,g4) = 1.5708
    c: Tangent(g3,g4) = 1.5708
    c: Radius(g4) = 16
    c: Parallel(g0,g-7)
    c: Coincident(g0,g-7)
    c: Coincident(g0,g3)
    c: Distance(g0,g-7) = 4
FEATURE [Sketcher::SketchObject] Sketch088  label="lato sx pistola - rialzo impugnatura"
  ArcFitTolerance = 1e-06
  AttachmentSupport = -> [XZ_Plane]
  ExternalGeometry = -> [Sketch074,Sketch087]
  FullyConstrained = true
  MakeInternals = false
  MapMode = 5
  Placement = pos=(0,0,0) rot=(1,0,0;1.5708rad)
  sketch-geometry (11):
    g0: LineSegment StartX=-144.029 StartY=20.0744 StartZ=0 EndX=-176.685 EndY=-80.4316 EndZ=0
    g1: Circle CenterX=-213.443 CenterY=-76.8316 CenterZ=0 NormalX=0 NormalY=0 NormalZ=1 AngleXU=0 Radius=3
    g2: Circle CenterX=-179.305 CenterY=-76.8316 CenterZ=0 NormalX=0 NormalY=0 NormalZ=1 AngleXU=0 Radius=3
    g3: LineSegment StartX=-176.685 StartY=-80.4316 StartZ=0 EndX=-215.932 EndY=-80.4316 EndZ=0
    g4: LineSegment StartX=-192.176 StartY=-3.18451 StartZ=0 EndX=-215.42 EndY=-53.0314 EndZ=0
    g5: ArcOfCircle CenterX=-184.801 CenterY=-67.3089 CenterZ=0 NormalX=0 NormalY=0 NormalZ=1 AngleXU=0 Radius=33.7833 StartAngle=2.70526 EndAngle=3.54053
    g6: LineSegment [constr] StartX=-192.176 StartY=-3.18451 StartZ=0 EndX=-181.33 EndY=20.0744 EndZ=0
    g7: LineSegment StartX=-144.029 StartY=20.0744 StartZ=0 EndX=-190.224 EndY=20.0744 EndZ=0
    g8: LineSegment StartX=-190.224 StartY=20.0744 StartZ=0 EndX=-191.316 EndY=17.0744 EndZ=0
    g9: LineSegment StartX=-191.316 StartY=17.0744 StartZ=0 EndX=-182.729 EndY=17.0744 EndZ=0
    g10: LineSegment StartX=-192.176 StartY=-3.18451 StartZ=0 EndX=-182.729 EndY=17.0744 EndZ=0
  constraints (26):
    c: Coincident(g0,g-5)
    c: Coincident(g2,g-10)
    c: Coincident(g1,g-9)
    c: Diameter(g2) = 6
    c: Diameter(g1) = 6
    c: Coincident(g3,g0)
    c: Coincident(g3,g-4)
    c: Equal(g4,g-15)
    c: Parallel(g4,g-15)
    c: Coincident(g4,g-15)
    c: Coincident(g5,g4)
    c: Coincident(g5,g3)
    c: Tangent(g6,g4) = 1.5708
    c: PointOnObject(g6,g-13)
    c: Coincident(g0,g-13)
    c: Coincident(g7,g0)
    c: Coincident(g7,g-14)
    c: Coincident(g8,g7)
    c: Coincident(g9,g8)
    c: Horizontal(g9)
    c: PointOnObject(g9,g6)
    c: Coincident(g10,g4)
    c: Coincident(g10,g9)
    c: DistanceY(g8,g8) = 3
    c: Parallel(g8,g-16)
    c: Tangent(g5,g-3)
FEATURE [Sketcher::SketchObject] Sketch089  label="lato sx pistola - disegno centrale"
  ArcFitTolerance = 1e-06
  AttachmentSupport = -> [XZ_Plane]
  ExternalGeometry = -> [Sketch086]
  FullyConstrained = true
  MakeInternals = false
  MapMode = 5
  Placement = pos=(0,0,0) rot=(1,0,0;1.5708rad)
  sketch-geometry (4):
    g0: LineSegment StartX=-130.215 StartY=39.2 StartZ=0 EndX=-119.215 EndY=39.2 EndZ=0
    g1: LineSegment StartX=-130.215 StartY=39.2 StartZ=0 EndX=-132.81 EndY=31.2111 EndZ=0
    g2: LineSegment StartX=-119.215 StartY=39.2 StartZ=0 EndX=-121.81 EndY=31.2111 EndZ=0
    g3: LineSegment StartX=-132.81 StartY=31.2111 StartZ=0 EndX=-121.81 EndY=31.2111 EndZ=0
  constraints (11):
    c: Horizontal(g3)
    c: Parallel(g2,g-4)
    c: Parallel(g1,g-4)
    c: Distance(g1) = 8.4
    c: DistanceX(g0,g0) = 11
    c: Tangent(g0,g-3)
    c: Coincident(g1,g0)
    c: Coincident(g2,g0)
    c: Coincident(g3,g1)
    c: Coincident(g3,g2)
    c: DistanceX(g0,g-4) = 8.4
FEATURE [Sketcher::SketchObject] Sketch090  label="lato sx pistola - disegno pre centrale"
  ArcFitTolerance = 1e-06
  AttachmentSupport = -> [XZ_Plane]
  ExternalGeometry = -> [Sketch074,Sketch086]
  FullyConstrained = true
  MakeInternals = false
  MapMode = 5
  Placement = pos=(0,0,0) rot=(1,0,0;1.5708rad)
  sketch-geometry (4):
    g0: LineSegment StartX=-106.615 StartY=36.8 StartZ=0 EndX=-89.6146 EndY=36.8 EndZ=0
    g1: LineSegment StartX=-110.254 StartY=26.8 StartZ=0 EndX=-89.6146 EndY=26.8 EndZ=0
    g2: LineSegment StartX=-106.615 StartY=36.8 StartZ=0 EndX=-110.254 EndY=26.8 EndZ=0
    g3: ArcOfCircle CenterX=-94.6146 CenterY=31.8 CenterZ=0 NormalX=0 NormalY=0 NormalZ=1 AngleXU=0 Radius=7.07107 StartAngle=5.49779 EndAngle=7.06858
  constraints (13):
    c: Horizontal(g0)
    c: Horizontal(g1)
    c: Parallel(g-3,g2)
    c: Coincident(g0,g2)
    c: DistanceY(g2,g2) = 10
    c: Coincident(g1,g2)
    c: DistanceX(g0,g0) = 17
    c: DistanceX(g0,g1) = 0
    c: Coincident(g3,g1)
    c: DistanceX(g-5,g0) = 4.2
    c: DistanceY(g0,g-5) = 2.4
    c: Coincident(g3,g0)
    c: DistanceX(g3,g0) = 5
FEATURE [PartDesign::Body] Body  label="Struttura pistola"
  AllowCompound = false
  Group = -> [Sketch,Sketch002,Sketch004,DatumPlane,Sketch005,DatumPlane001,CopyCut,Sketch008,Sketch009,Sketch010,Sketch011,Sketch012,Sketch013,Sketch014,Sketch015,Sketch016,Sketch017,Sketch018,Sketch019,Sketch020,Sketch022,Sketch023,Sketch024,Sketch025,Sketch026,Sketch027,Sketch029,Sketch030,Sketch031,Sketch032,Sketch033,Sketch034,Sketch035,Sketch036,Sketch037,Sketch038,Sketch039,Sketch040,Sketch041,Sketch042,+28 more]
  Origin = -> Origin
FEATURE [PartDesign::SubShapeBinder] Binder
  BindCopyOnChange = 0
  BindMode = 0
  ClaimChildren = false
  Context = -> Body006 [Binder.]
  Fuse = false
  MakeFace = true
  OffsetFill = false
  OffsetIntersection = false
  OffsetJoinType = 0
  OffsetOpenResult = false
  PartialLoad = false
  Refine = true
  Relative = true
  Support = -> [Body[Sketch074.]]
  _Version = 2
FEATURE [PartDesign::SubShapeBinder] Binder001
  BindCopyOnChange = 0
  BindMode = 0
  ClaimChildren = false
  Context = -> Body007 [Binder001.]
  Fuse = false
  MakeFace = true
  OffsetFill = false
  OffsetIntersection = false
  OffsetJoinType = 0
  OffsetOpenResult = false
  PartialLoad = false
  Refine = true
  Relative = true
  Support = -> [Body[Sketch075.]]
  _Version = 2
FEATURE [PartDesign::Pad] Pad004
  Direction = (0,1,0)
  Length = 2
  Length2 = 10
  Profile = -> Binder
  Refine = true
  Suppressed = false
  Type = 0
FEATURE [Sketcher::SketchObject] Sketch091  label="Sketch091 - forma anteriore"
  ArcFitTolerance = 1e-06
  AttachmentSupport = -> [Pad004]
  ExternalGeometry = -> [Binder]
  FullyConstrained = true
  MakeInternals = false
  MapMode = 5
  Placement = pos=(0,2,0) rot=(0,0.707107,0.707107;3.14159rad)
  sketch-geometry (12):
    g0: Circle CenterX=5.6 CenterY=34.8 CenterZ=0 NormalX=0 NormalY=0 NormalZ=1 AngleXU=0 Radius=1.8
    g1: Circle CenterX=5.6 CenterY=7.6 CenterZ=0 NormalX=0 NormalY=0 NormalZ=1 AngleXU=0 Radius=1.8
    g2: Circle CenterX=78.51 CenterY=34.8 CenterZ=0 NormalX=0 NormalY=0 NormalZ=1 AngleXU=0 Radius=1.8
    g3: Circle CenterX=78.51 CenterY=7.6 CenterZ=0 NormalX=0 NormalY=0 NormalZ=1 AngleXU=0 Radius=1.8
    g4: LineSegment StartX=0 StartY=39.2 StartZ=0 EndX=0 EndY=3.2 EndZ=0
    g5: LineSegment StartX=0 StartY=3.2 StartZ=0 EndX=82.8 EndY=3.2 EndZ=0
    g6: LineSegment StartX=82.8 StartY=3.2 StartZ=0 EndX=82.8 EndY=39.2 EndZ=0
    g7: LineSegment StartX=82.8 StartY=39.2 StartZ=0 EndX=0 EndY=39.2 EndZ=0
    g8: ArcOfCircle CenterX=19 CenterY=21.2 CenterZ=0 NormalX=0 NormalY=0 NormalZ=1 AngleXU=0 Radius=10 StartAngle=1.5708 EndAngle=4.71239
    g9: ArcOfCircle CenterX=65 CenterY=21.2 CenterZ=0 NormalX=0 NormalY=0 NormalZ=1 AngleXU=0 Radius=10 StartAngle=4.71239 EndAngle=7.85398
    g10: LineSegment StartX=19 StartY=31.2 StartZ=0 EndX=65 EndY=31.2 EndZ=0
    g11: LineSegment StartX=19 StartY=11.2 StartZ=0 EndX=65 EndY=11.2 EndZ=0
  constraints (25):
    c: Equal(g2,g-7)
    c: Equal(g3,g-8)
    c: Equal(g1,g-13)
    c: Equal(g0,g-12)
    c: Coincident(g0,g-12)
    c: Coincident(g1,g-13)
    c: Coincident(g3,g-8)
    c: Coincident(g2,g-7)
    c: Coincident(g4,g-4)
    c: Coincident(g4,g-5)
    c: Coincident(g5,g4)
    c: Coincident(g5,g-6)
    c: Coincident(g6,g5)
    c: PointOnObject(g6,g-3)
    c: Vertical(g6)
    c: Coincident(g7,g6)
    c: Coincident(g7,g4)
    c: Tangent(g8,g10) = 1.5708
    c: Tangent(g8,g11) = -1.5708
    c: Tangent(g9,g10) = 1.5708
    c: Tangent(g9,g11) = -1.5708
    c: Equal(g8,g9)
    c: Radius(g8) = 10
    c: Coincident(g8,g-11)
    c: Coincident(g9,g-9)
FEATURE [PartDesign::Pad] Pad005
  BaseFeature = -> Pad004
  Direction = (0,1,-2e-16)
  Length = 1.6
  Length2 = 10
  Profile = -> Sketch091
  ReferenceAxis = -> Sketch091 [N_Axis]
  Refine = true
  Suppressed = false
  Type = 0
FEATURE [Sketcher::SketchObject] Sketch092  label="Sketch092 - scavi per viti anteriori"
  ArcFitTolerance = 1e-06
  AttachmentSupport = -> [Pad005]
  ExternalGeometry = -> [Binder]
  FullyConstrained = true
  MakeInternals = false
  MapMode = 5
  Placement = pos=(0,3.6,0) rot=(0,0.707107,0.707107;3.14159rad)
  sketch-geometry (20):
    g0: ArcOfCircle CenterX=5.6 CenterY=7.6 CenterZ=0 NormalX=0 NormalY=0 NormalZ=1 AngleXU=0 Radius=3.5 StartAngle=0 EndAngle=1.5708
    g1: ArcOfCircle CenterX=5.6 CenterY=34.8 CenterZ=0 NormalX=0 NormalY=0 NormalZ=1 AngleXU=0 Radius=3.5 StartAngle=4.71239 EndAngle=6.28319
    g2: ArcOfCircle CenterX=78.51 CenterY=34.8 CenterZ=0 NormalX=0 NormalY=0 NormalZ=1 AngleXU=0 Radius=3.5 StartAngle=3.14159 EndAngle=4.71239
    g3: ArcOfCircle CenterX=78.51 CenterY=7.6 CenterZ=0 NormalX=0 NormalY=0 NormalZ=1 AngleXU=0 Radius=3.5 StartAngle=1.5708 EndAngle=3.14159
    g4: LineSegment StartX=0 StartY=3.2 StartZ=0 EndX=0 EndY=11.1 EndZ=0
    g5: LineSegment StartX=0 StartY=11.1 StartZ=0 EndX=5.6 EndY=11.1 EndZ=0
    g6: LineSegment StartX=0 StartY=3.2 StartZ=0 EndX=9.1 EndY=3.2 EndZ=0
    g7: LineSegment StartX=9.1 StartY=3.2 StartZ=0 EndX=9.1 EndY=7.6 EndZ=0
    g8: LineSegment StartX=0 StartY=39.2 StartZ=0 EndX=0 EndY=31.3 EndZ=0
    g9: LineSegment StartX=0 StartY=31.3 StartZ=0 EndX=5.6 EndY=31.3 EndZ=0
    g10: LineSegment StartX=0 StartY=39.2 StartZ=0 EndX=9.1 EndY=39.2 EndZ=0
    g11: LineSegment StartX=9.1 StartY=39.2 StartZ=0 EndX=9.1 EndY=34.8 EndZ=0
    g12: LineSegment StartX=82.8 StartY=39.2 StartZ=0 EndX=75.01 EndY=39.2 EndZ=0
    g13: LineSegment StartX=82.8 StartY=39.2 StartZ=0 EndX=82.8 EndY=31.3 EndZ=0
    g14: LineSegment StartX=82.8 StartY=31.3 StartZ=0 EndX=78.51 EndY=31.3 EndZ=0
    g15: LineSegment StartX=82.8 StartY=3.2 StartZ=0 EndX=75.01 EndY=3.2 EndZ=0
    g16: LineSegment StartX=75.01 StartY=3.2 StartZ=0 EndX=75.01 EndY=7.6 EndZ=0
    g17: LineSegment StartX=82.8 StartY=3.2 StartZ=0 EndX=82.8 EndY=11.1 EndZ=0
    g18: LineSegment StartX=82.8 StartY=11.1 StartZ=0 EndX=78.51 EndY=11.1 EndZ=0
    g19: LineSegment StartX=75.01 StartY=39.2 StartZ=0 EndX=75.01 EndY=34.8 EndZ=0
  constraints (48):
    c: Radius(g0) = 3.5
    c: Coincident(g0,g-10)
    c: Radius(g1) = 3.5
    c: Coincident(g1,g-9)
    c: Radius(g2) = 3.5
    c: Coincident(g2,g-8)
    c: Radius(g3) = 3.5
    c: Coincident(g3,g-7)
    c: Coincident(g4,g-5)
    c: PointOnObject(g4,g-4)
    c: Coincident(g5,g4)
    c: Horizontal(g5)
    c: Coincident(g6,g4)
    c: PointOnObject(g6,g-5)
    c: Coincident(g7,g6)
    c: Vertical(g7)
    c: Coincident(g8,g-4)
    c: PointOnObject(g8,g-4)
    c: Coincident(g9,g8)
    c: Horizontal(g9)
    c: Coincident(g10,g8)
    c: PointOnObject(g10,g-3)
    c: Coincident(g11,g10)
    c: Vertical(g11)
    c: PointOnObject(g12,g-3)
    c: PointOnObject(g12,g-3)
    c: Coincident(g13,g12)
    c: Vertical(g13)
    c: Coincident(g14,g13)
    c: Horizontal(g14)
    c: Coincident(g15,g-6)
    c: PointOnObject(g15,g-5)
    c: Coincident(g16,g15)
    c: Vertical(g16)
    c: Coincident(g17,g15)
    c: Coincident(g18,g17)
    c: Horizontal(g18)
    c: Tangent(g3,g18) = -1.5708
    c: Tangent(g16,g3) = 1.5708
    c: Coincident(g19,g12)
    c: Vertical(g19)
    c: Tangent(g2,g19) = -1.5708
    c: Tangent(g2,g14) = 1.5708
    c: Tangent(g0,g7) = -1.5708
    c: Tangent(g0,g5) = 1.5708
    c: Tangent(g9,g1) = -1.5708
    c: Tangent(g1,g11) = 1.5708
    c: Tangent(g17,g13)
FEATURE [PartDesign::Pocket] Pocket001
  BaseFeature = -> Pad005
  Direction = (0,-1,2e-16)
  Length = 1.6
  Length2 = 5
  Profile = -> Sketch092
  ReferenceAxis = -> Sketch092 [N_Axis]
  Refine = true
  Suppressed = false
  Type = 0
FEATURE [Sketcher::SketchObject] Sketch093  label="Sketch093 - scavi interni pulsanti"
  ArcFitTolerance = 1e-06
  AttachmentSupport = -> [Pad004]
  ExternalGeometry = -> [Binder]
  FullyConstrained = true
  MakeInternals = false
  MapMode = 5
  Placement = pos=(0,9e-16,0) rot=(1,0,0;1.5708rad)
  sketch-geometry (3):
    g0: Circle CenterX=-65 CenterY=21.2 CenterZ=0 NormalX=0 NormalY=0 NormalZ=1 AngleXU=0 Radius=7.3
    g1: Circle CenterX=-42 CenterY=21.2 CenterZ=0 NormalX=0 NormalY=0 NormalZ=1 AngleXU=0 Radius=7.3
    g2: Circle CenterX=-19 CenterY=21.2 CenterZ=0 NormalX=0 NormalY=0 NormalZ=1 AngleXU=0 Radius=7.3
  constraints (6):
    c: Coincident(g0,g-3)
    c: Coincident(g1,g-4)
    c: Coincident(g2,g-5)
    c: Diameter(g0) = 14.6
    c: Diameter(g1) = 14.6
    c: Diameter(g2) = 14.6
FEATURE [PartDesign::Pocket] Pocket002
  BaseFeature = -> Pocket001
  Direction = (0,1,-2e-16)
  Length = 1.2
  Length2 = 5
  Profile = -> Sketch093
  ReferenceAxis = -> Sketch093 [N_Axis]
  Refine = true
  Suppressed = false
  Type = 0
FEATURE [Sketcher::SketchObject] Sketch094  label="Sketch094 - forma centrale"
  ArcFitTolerance = 1e-06
  AttachmentSupport = -> [Pad004]
  ExternalGeometry = -> [Binder]
  FullyConstrained = true
  MakeInternals = false
  MapMode = 5
  Placement = pos=(0,2,0) rot=(0,0.707107,0.707107;3.14159rad)
  sketch-geometry (4):
    g0: LineSegment StartX=137.815 StartY=39.2 StartZ=0 EndX=142.655 EndY=24.303 EndZ=0
    g1: LineSegment StartX=110.815 StartY=24.303 StartZ=0 EndX=142.655 EndY=24.303 EndZ=0
    g2: LineSegment StartX=137.815 StartY=39.2 StartZ=0 EndX=110.815 EndY=39.2 EndZ=0
    g3: ArcOfCircle CenterX=92.2534 CenterY=31.7515 CenterZ=0 NormalX=0 NormalY=0 NormalZ=1 AngleXU=0 Radius=20 StartAngle=5.90156 EndAngle=6.66481
  constraints (12):
    c: PointOnObject(g0,g-3)
    c: Tangent(g0,g-5)
    c: Horizontal(g1)
    c: Coincident(g1,g0)
    c: Coincident(g2,g0)
    c: PointOnObject(g2,g-3)
    c: DistanceX(g2,g2) = 27
    c: Vertical(g1,g2)
    c: Coincident(g3,g2)
    c: Radius(g3) = 20
    c: Coincident(g3,g1)
    c: DistanceY(g-6,g0) = 4
FEATURE [PartDesign::Pad] Pad006
  BaseFeature = -> Pocket002
  Direction = (0,1,-2e-16)
  Length = 0.8
  Length2 = 10
  Profile = -> Sketch094
  ReferenceAxis = -> Sketch094 [N_Axis]
  Refine = true
  Suppressed = false
  Type = 0
FEATURE [Sketcher::SketchObject] Sketch095  label="Sketch095 - forma posteriore"
  ArcFitTolerance = 1e-06
  AttachmentSupport = -> [Pad004]
  ExternalGeometry = -> [Binder]
  FullyConstrained = true
  MakeInternals = false
  MapMode = 5
  Placement = pos=(0,2,0) rot=(0,0.707107,0.707107;3.14159rad)
  sketch-geometry (15):
    g0: LineSegment StartX=137.815 StartY=39.2 StartZ=0 EndX=143.955 EndY=20.303 EndZ=0
    g1: LineSegment StartX=143.955 StartY=20.303 StartZ=0 EndX=190.141 EndY=20.303 EndZ=0
    g2: ArcOfCircle CenterX=184.08 CenterY=34.8 CenterZ=0 NormalX=0 NormalY=0 NormalZ=1 AngleXU=0 Radius=3.5 StartAngle=3.49066 EndAngle=4.71239
    g3: LineSegment StartX=180.791 StartY=33.6029 StartZ=0 EndX=178.754 EndY=39.2 EndZ=0
    g4: LineSegment StartX=184.08 StartY=31.3 StartZ=0 EndX=186.139 EndY=31.3 EndZ=0
    g5: LineSegment StartX=190.141 StartY=20.303 StartZ=0 EndX=186.139 EndY=31.3 EndZ=0
    g6: LineSegment StartX=137.815 StartY=39.2 StartZ=0 EndX=156.815 EndY=39.2 EndZ=0
    g7: LineSegment StartX=178.754 StartY=39.2 StartZ=0 EndX=168.815 EndY=39.2 EndZ=0
    g8: LineSegment StartX=156.815 StartY=31.2 StartZ=0 EndX=168.815 EndY=31.2 EndZ=0
    g9: ArcOfCircle CenterX=176.411 CenterY=35.2 CenterZ=0 NormalX=0 NormalY=0 NormalZ=1 AngleXU=0 Radius=20 StartAngle=2.94023 EndAngle=3.34295
    g10: ArcOfCircle CenterX=188.411 CenterY=35.2 CenterZ=0 NormalX=0 NormalY=0 NormalZ=1 AngleXU=0 Radius=20 StartAngle=2.94023 EndAngle=3.34295
    g11: LineSegment StartX=157.815 StartY=39.2 StartZ=0 EndX=167.815 EndY=39.2 EndZ=0
    g12: LineSegment StartX=157.436 StartY=36.2 StartZ=0 EndX=167.436 EndY=36.2 EndZ=0
    g13: ArcOfCircle CenterX=177.411 CenterY=35.2 CenterZ=0 NormalX=0 NormalY=0 NormalZ=1 AngleXU=0 Radius=20 StartAngle=2.94023 EndAngle=3.09157
    g14: ArcOfCircle CenterX=187.411 CenterY=35.2 CenterZ=0 NormalX=0 NormalY=0 NormalZ=1 AngleXU=0 Radius=20 StartAngle=2.94023 EndAngle=3.09157
  constraints (46):
    c: PointOnObject(g0,g-3)
    c: Tangent(g0,g-6)
    c: Coincident(g1,g0)
    c: Horizontal(g1)
    c: Radius(g2) = 3.5
    c: Coincident(g2,g-5)
    c: PointOnObject(g3,g-3)
    c: Parallel(g3,g-4)
    c: Tangent(g3,g2) = 1.5708
    c: Horizontal(g4)
    c: Tangent(g4,g2) = -1.5708
    c: Coincident(g5,g1)
    c: Parallel(g5,g-4)
    c: Coincident(g5,g4)
    c: DistanceX(g4,g-8) = 3.8
    c: Coincident(g6,g0)
    c: PointOnObject(g6,g-3)
    c: Coincident(g7,g3)
    c: PointOnObject(g7,g-3)
    c: Horizontal(g8)
    c: DistanceX(g6,g7) = 12
    c: Vertical(g8,g6)
    c: Vertical(g7,g8)
    c: DistanceY(g8,g6) = 8
    c: Coincident(g9,g8)
    c: Coincident(g9,g6)
    c: Coincident(g10,g7)
    c: Coincident(g10,g8)
    c: Radius(g9) = 20
    c: Radius(g10) = 20
    c: PointOnObject(g11,g-3)
    c: PointOnObject(g11,g-3)
    c: DistanceX(g11,g11) = 10
    c: DistanceX(g6,g11) = 1
    c: Horizontal(g12)
    c: Equal(g12,g11)
    c: DistanceY(g12,g11) = 3
    c: Coincident(g13,g11)
    c: Coincident(g13,g12)
    c: Radius(g13) = 20
    c: Coincident(g14,g11)
    c: Coincident(g14,g12)
    c: Radius(g14) = 20
    c: DistanceX(g0,g6) = 19
    c: Horizontal(g9,g13)
    c: Horizontal(g0,g-4)
FEATURE [PartDesign::Pad] Pad007
  BaseFeature = -> Pad006
  Direction = (0,1,-2e-16)
  Length = 2
  Length2 = 10
  Profile = -> Sketch095
  ReferenceAxis = -> Sketch095 [N_Axis]
  Refine = true
  Suppressed = false
  Type = 0
FEATURE [Sketcher::SketchObject] Sketch096  label="Sketch096 - forma impugnatura"
  ArcFitTolerance = 1e-06
  AttachmentSupport = -> [Pad004]
  ExternalGeometry = -> [Binder]
  FullyConstrained = true
  MakeInternals = false
  MapMode = 5
  Placement = pos=(0,2,0) rot=(0,0.707107,0.707107;3.14159rad)
  sketch-geometry (8):
    g0: LineSegment StartX=176.685 StartY=-80.4316 StartZ=0 EndX=143.955 EndY=20.303 EndZ=0
    g1: LineSegment StartX=176.685 StartY=-80.4316 StartZ=0 EndX=215.932 EndY=-80.4316 EndZ=0
    g2: Circle CenterX=179.305 CenterY=-76.8316 CenterZ=0 NormalX=0 NormalY=0 NormalZ=1 AngleXU=0 Radius=3
    g3: Circle CenterX=213.443 CenterY=-76.8316 CenterZ=0 NormalX=0 NormalY=0 NormalZ=1 AngleXU=0 Radius=3
    g4: LineSegment StartX=143.955 StartY=20.303 StartZ=0 EndX=202.765 EndY=20.303 EndZ=0
    g5: LineSegment StartX=215.42 StartY=-53.0314 StartZ=0 EndX=192.176 EndY=-3.18451 EndZ=0
    g6: ArcOfCircle CenterX=184.801 CenterY=-67.3089 CenterZ=0 NormalX=0 NormalY=0 NormalZ=1 AngleXU=0 Radius=33.7833 StartAngle=5.88425 EndAngle=6.71952
    g7: ArcOfCircle CenterX=207.583 CenterY=4 CenterZ=0 NormalX=0 NormalY=0 NormalZ=1 AngleXU=0 Radius=17 StartAngle=1.85815 EndAngle=3.57792
  constraints (19):
    c: Coincident(g0,g-4)
    c: PointOnObject(g0,g-3)
    c: Horizontal(g0,g-7)
    c: Coincident(g1,g0)
    c: Coincident(g1,g-5)
    c: Diameter(g2) = 6
    c: Diameter(g3) = 6
    c: Coincident(g2,g-9)
    c: Coincident(g3,g-10)
    c: Coincident(g4,g0)
    c: Coincident(g5,g-6)
    c: Coincident(g6,g1)
    c: Coincident(g6,g5)
    c: Equal(g-5,g6)
    c: Coincident(g5,g-7)
    c: Coincident(g4,g-7)
    c: Tangent(g7,g-7)
    c: Coincident(g7,g4)
    c: Coincident(g7,g5)
FEATURE [PartDesign::Pad] Pad008  label="Pad008 - forma impugnatura"
  BaseFeature = -> Pad007
  Direction = (0,1,-2e-16)
  Length = 1.6
  Length2 = 10
  Profile = -> Sketch096
  ReferenceAxis = -> Sketch096 [N_Axis]
  Refine = true
  Suppressed = false
  Type = 0
FEATURE [Sketcher::SketchObject] Sketch097
  ArcFitTolerance = 1e-06
  AttachmentSupport = -> [Pad004]
  ExternalGeometry = -> [Binder]
  FullyConstrained = true
  MakeInternals = false
  MapMode = 5
  Placement = pos=(0,2,0) rot=(0,0.707107,0.707107;3.14159rad)
  sketch-geometry (4):
    g0: LineSegment StartX=90 StartY=36.8 StartZ=0 EndX=108 EndY=36.8 EndZ=0
    g1: LineSegment StartX=108 StartY=36.8 StartZ=0 EndX=108 EndY=26.8 EndZ=0
    g2: LineSegment StartX=108 StartY=26.8 StartZ=0 EndX=90 EndY=26.8 EndZ=0
    g3: ArcOfCircle CenterX=94 CenterY=31.8 CenterZ=0 NormalX=0 NormalY=0 NormalZ=1 AngleXU=0 Radius=6.40312 StartAngle=2.24554 EndAngle=4.03765
  constraints (13):
    c: Horizontal(g0)
    c: Coincident(g1,g0)
    c: Vertical(g1)
    c: DistanceX(g0,g0) = 18
    c: DistanceY(g1,g1) = 10
    c: Coincident(g2,g1)
    c: Horizontal(g2)
    c: Equal(g2,g0)
    c: DistanceY(g0,g-3) = 2.4
    c: Coincident(g3,g0)
    c: Coincident(g3,g2)
    c: DistanceX(g2,g3) = 4
    c: DistanceX(g-3,g0) = 90
FEATURE [PartDesign::Pad] Pad009
  BaseFeature = -> Pad008
  Direction = (0,1,-2e-16)
  Length = 1.6
  Length2 = 10
  Profile = -> Sketch097
  ReferenceAxis = -> Sketch097 [N_Axis]
  Refine = true
  Suppressed = false
  Type = 0
FEATURE [Sketcher::SketchObject] Sketch098
  ArcFitTolerance = 1e-06
  AttachmentSupport = -> [Pad006]
  ExternalGeometry = -> [Binder]
  FullyConstrained = true
  MakeInternals = false
  MapMode = 5
  Placement = pos=(0,2.8,-7e-16) rot=(0,0.707107,0.707107;3.14159rad)
  sketch-geometry (4):
    g0: LineSegment StartX=118 StartY=39.2 StartZ=0 EndX=129 EndY=39.2 EndZ=0
    g1: LineSegment StartX=120.599 StartY=31.2 StartZ=0 EndX=131.599 EndY=31.2 EndZ=0
    g2: LineSegment StartX=129 StartY=39.2 StartZ=0 EndX=131.599 EndY=31.2 EndZ=0
    g3: LineSegment StartX=118 StartY=39.2 StartZ=0 EndX=120.599 EndY=31.2 EndZ=0
  constraints (12):
    c: PointOnObject(g0,g-3)
    c: PointOnObject(g0,g-3)
    c: DistanceX(g0,g0) = 11
    c: Horizontal(g1)
    c: Equal(g1,g0)
    c: Coincident(g2,g0)
    c: Coincident(g3,g0)
    c: Parallel(g-4,g2)
    c: Coincident(g1,g2)
    c: Coincident(g1,g3)
    c: DistanceY(g1,g0) = 8
    c: DistanceX(g-3,g0) = 118
FEATURE [PartDesign::Pad] Pad010
  BaseFeature = -> Pad009
  Direction = (0,1,-2e-16)
  Length = 1.2
  Length2 = 10
  Profile = -> Sketch098
  ReferenceAxis = -> Sketch098 [N_Axis]
  Refine = true
  Suppressed = false
  Type = 0
FEATURE [Sketcher::SketchObject] Sketch099
  ArcFitTolerance = 1e-06
  AttachmentSupport = -> [Pad008]
  ExternalGeometry = -> [Binder]
  FullyConstrained = true
  MakeInternals = false
  MapMode = 5
  Placement = pos=(0,3.6,0) rot=(0,0.707107,0.707107;3.14159rad)
  sketch-geometry (13):
    g0: LineSegment StartX=192.176 StartY=-3.18451 StartZ=0 EndX=196.804 EndY=-13.1108 EndZ=0
    g1: LineSegment [constr] StartX=202.765 StartY=20.303 StartZ=0 EndX=181.223 EndY=20.303 EndZ=0
    g2: LineSegment [constr] StartX=181.223 StartY=20.303 StartZ=0 EndX=181.223 EndY=-3.18451 EndZ=0
    g3: ArcOfCircle CenterX=181.223 CenterY=-20.3764 CenterZ=0 NormalX=0 NormalY=0 NormalZ=1 AngleXU=0 Radius=17.1918 StartAngle=0.436332 EndAngle=1.57079
    g4: ArcOfEllipse CenterX=181.223 CenterY=8.55923 CenterZ=0 NormalX=0 NormalY=0 NormalZ=1 MajorRadius=23.4779 MinorRadius=11.7437 AngleXU=0 StartAngle=1.5708 EndAngle=4.71239
    g5: LineSegment [constr] StartX=204.701 StartY=8.55923 StartZ=0 EndX=157.745 EndY=8.55923 EndZ=0
    g6: LineSegment [constr] StartX=181.223 StartY=20.303 StartZ=0 EndX=181.223 EndY=-3.18451 EndZ=0
    g7: GeomPoint [constr] X=201.553 Y=8.55923 Z=0
    g8: GeomPoint [constr] X=160.894 Y=8.55923 Z=0
    g9: GeomPoint [constr] X=181.223 Y=-3.18451 Z=0
    g10: LineSegment StartX=181.223 StartY=20.303 StartZ=0 EndX=202.765 EndY=20.303 EndZ=0
    g11: ArcOfCircle CenterX=207.583 CenterY=4 CenterZ=0 NormalX=0 NormalY=0 NormalZ=1 AngleXU=0 Radius=17 StartAngle=1.85815 EndAngle=3.57792
    g12: LineSegment [constr] StartX=172.411 StartY=39.2 StartZ=0 EndX=192.176 EndY=-3.18451 EndZ=0
  constraints (27):
    c: Coincident(g1,g-7)
    c: Horizontal(g1)
    c: Coincident(g2,g1)
    c: Vertical(g2)
    c: Horizontal(g2,g0)
    c: Coincident(g3,g0)
    c: Coincident(g3,g2)
    c: InternalAlignment(g5-g8 -> g4) x4
    c: Horizontal(g5)
    c: PointOnObject(g4,g2)
    c: Coincident(g4,g1)
    c: DistanceX(g-3,g5) = 10.1
    c: Coincident(g4,g2)
    c: Tangent(g3,g-5)
    c: PointOnObject(g9,g4)
    c: PointOnObject(g9,g3)
    c: Tangent(g4,g3,g9) = 1.5708
    c: Coincident(g10,g1)
    c: Coincident(g10,g1)
    c: Equal(g11,g-4)
    c: Coincident(g11,g1)
    c: Coincident(g11,g0)
    c: PointOnObject(g12,g-6)
    c: PointOnObject(g1,g12)
    c: Tangent(g12,g-5) = -1.5708
    c: Tangent(g0,g-5) = -1.5708
    c: Horizontal(g9,g12)
FEATURE [Sketcher::SketchObject] Sketch106  label="Sketch106 - smusso impuniatura interno"
  ArcFitTolerance = 1e-06
  AttachmentSupport = -> [Pad008]
  ExternalGeometry = -> [Pad008]
  FullyConstrained = true
  MakeInternals = false
  MapMode = 5
  Placement = pos=(0,0,-80.4316) rot=(1,0,0;3.14159rad)
  sketch-geometry (9):
    g0: LineSegment StartX=-176.685 StartY=-3.6 StartZ=0 EndX=-176.685 EndY=1.168e-12 EndZ=0
    g1: LineSegment [constr] StartX=-176.685 StartY=1.79e-14 StartZ=0 EndX=-176.685 EndY=1.1682e-12 EndZ=0
    g2: LineSegment [constr] StartX=-186.685 StartY=-3.6 StartZ=0 EndX=-186.685 EndY=1.168e-12 EndZ=0
    g3: ArcOfEllipse CenterX=-186.685 CenterY=1.1682e-12 CenterZ=0 NormalX=0 NormalY=0 NormalZ=1 MajorRadius=10 MinorRadius=3.6 AngleXU=-3.14159 StartAngle=1.5708 EndAngle=3.14159
    g4: LineSegment [constr] StartX=-196.685 StartY=1.79e-14 StartZ=0 EndX=-176.685 EndY=1.79e-14 EndZ=0
    g5: LineSegment [constr] StartX=-186.685 StartY=-3.6 StartZ=0 EndX=-186.685 EndY=3.6 EndZ=0
    g6: GeomPoint [constr] X=-196.015 Y=1.6e-14 Z=0
    g7: GeomPoint [constr] X=-177.356 Y=1.85e-14 Z=0
    g8: LineSegment StartX=-176.685 StartY=-3.6 StartZ=0 EndX=-186.685 EndY=-3.6 EndZ=0
  constraints (15):
    c: PointOnObject(g2,g-3)
    c: Coincident(g1,g-5)
    c: DistanceY(g1,g1) = 0
    c: Coincident(g0,g1)
    c: DistanceX(g2,g-5) = 10
    c: Vertical(g2)
    c: Horizontal(g2,g0)
    c: InternalAlignment(g4-g7 -> g3) x4
    c: Coincident(g3,g2)
    c: Horizontal(g4)
    c: Coincident(g3,g0)
    c: Tangent(g0,g-5) = 1.5708
    c: Coincident(g3,g2)
    c: Coincident(g8,g0)
    c: Coincident(g8,g2)
FEATURE [Sketcher::SketchObject] Sketch107  label="Sketch107 - smusso impugnatura esterno"
  ArcFitTolerance = 1e-06
  AttachmentSupport = -> [Pad008]
  ExternalGeometry = -> [Pad008]
  FullyConstrained = true
  MakeInternals = false
  MapMode = 5
  Placement = pos=(0,0,-80.4316) rot=(1,0,0;3.14159rad)
  sketch-geometry (9):
    g0: LineSegment [constr] StartX=-215.932 StartY=1.79e-14 StartZ=0 EndX=-215.932 EndY=1.94e-14 EndZ=0
    g1: LineSegment StartX=-215.932 StartY=-3.6 StartZ=0 EndX=-215.932 EndY=1.95e-14 EndZ=0
    g2: LineSegment StartX=-215.932 StartY=-3.6 StartZ=0 EndX=-205.932 EndY=-3.6 EndZ=0
    g3: LineSegment [constr] StartX=-205.932 StartY=-3.6 StartZ=0 EndX=-205.932 EndY=1.95e-14 EndZ=0
    g4: ArcOfEllipse CenterX=-205.932 CenterY=1.94e-14 CenterZ=0 NormalX=0 NormalY=0 NormalZ=1 MajorRadius=10 MinorRadius=3.6 AngleXU=3.14159 StartAngle=1e-16 EndAngle=1.5708
    g5: LineSegment [constr] StartX=-215.932 StartY=1.79e-14 StartZ=0 EndX=-195.932 EndY=1.79e-14 EndZ=0
    g6: LineSegment [constr] StartX=-205.932 StartY=-3.6 StartZ=0 EndX=-205.932 EndY=3.6 EndZ=0
    g7: GeomPoint [constr] X=-215.262 Y=1.97e-14 Z=0
    g8: GeomPoint [constr] X=-196.602 Y=1.78e-14 Z=0
  constraints (16):
    c: Coincident(g0,g-6)
    c: PointOnObject(g0,g-6)
    c: DistanceY(g0,g0) = 0
    c: Coincident(g1,g-6)
    c: Coincident(g1,g0)
    c: Tangent(g2,g-3)
    c: DistanceX(g2,g2) = 10
    c: Coincident(g3,g2)
    c: Vertical(g3)
    c: Horizontal(g3,g0)
    c: InternalAlignment(g5-g8 -> g4) x4
    c: Coincident(g4,g3)
    c: Horizontal(g5)
    c: Coincident(g4,g0)
    c: Coincident(g4,g2)
    c: PointOnObject(g2,g1)
FEATURE [PartDesign::SubtractivePipe] SubtractivePipe
  AuxilleryCurvelinear = true
  AuxillerySpineTangent = false
  BaseFeature = -> Pad010
  Binormal = (0,0,0)
  Mode = 0
  Profile = -> Sketch106
  Refine = true
  Spine = -> Pad008 [Edge208]
  SpineTangent = false
  Suppressed = false
  Transformation = 0
  Transition = 0
FEATURE [PartDesign::SubtractivePipe] SubtractivePipe001
  AuxilleryCurvelinear = true
  AuxillerySpineTangent = false
  BaseFeature = -> SubtractivePipe
  Binormal = (0,0,0)
  Mode = 0
  Profile = -> Sketch107
  Refine = true
  Spine = -> Pad008 [Edge206,Edge209,Edge197]
  SpineTangent = false
  Suppressed = false
  Transformation = 0
  Transition = 0
FEATURE [Sketcher::SketchObject] Sketch108
  ArcFitTolerance = 1e-06
  AttachmentOffset = pos=(0,0,-1.6) rot=(0,0,1;0rad)
  AttachmentSupport = -> [Pad008]
  ExternalGeometry = -> [Binder]
  FullyConstrained = true
  MakeInternals = false
  MapMode = 5
  Placement = pos=(0,2,4e-16) rot=(0,0.707107,0.707107;3.14159rad)
  sketch-geometry (14):
    g0: LineSegment StartX=192.176 StartY=-3.18451 StartZ=0 EndX=193.827 EndY=-6.72678 EndZ=0
    g1: LineSegment [constr] StartX=202.765 StartY=20.303 StartZ=0 EndX=181.223 EndY=20.303 EndZ=0
    g2: LineSegment [constr] StartX=181.223 StartY=20.303 StartZ=0 EndX=181.223 EndY=1.30297 EndZ=0
    g3: ArcOfCircle CenterX=181.223 CenterY=-12.6042 CenterZ=0 NormalX=0 NormalY=0 NormalZ=1 AngleXU=0 Radius=13.9072 StartAngle=0.436332 EndAngle=1.5708
    g4: ArcOfEllipse CenterX=181.223 CenterY=10.803 CenterZ=0 NormalX=0 NormalY=0 NormalZ=1 MajorRadius=14.4779 MinorRadius=9.5 AngleXU=0 StartAngle=1.5708 EndAngle=4.71239
    g5: LineSegment [constr] StartX=195.701 StartY=10.803 StartZ=0 EndX=166.745 EndY=10.803 EndZ=0
    g6: LineSegment [constr] StartX=181.223 StartY=20.303 StartZ=0 EndX=181.223 EndY=1.30297 EndZ=0
    g7: GeomPoint [constr] X=192.148 Y=10.803 Z=0
    g8: GeomPoint [constr] X=170.298 Y=10.803 Z=0
    g9: LineSegment StartX=181.223 StartY=20.303 StartZ=0 EndX=202.765 EndY=20.303 EndZ=0
    g10: ArcOfCircle CenterX=207.583 CenterY=4 CenterZ=0 NormalX=0 NormalY=0 NormalZ=1 AngleXU=0 Radius=17 StartAngle=1.85815 EndAngle=3.57792
    g11: LineSegment [constr] StartX=172.411 StartY=39.2 StartZ=0 EndX=192.176 EndY=-3.18451 EndZ=0
    g12: GeomPoint [constr] X=181.223 Y=1.30297 Z=0
    g13: GeomPoint [constr] X=181.223 Y=1.30297 Z=0
  constraints (28):
    c: Coincident(g1,g-7)
    c: Horizontal(g1)
    c: Coincident(g2,g1)
    c: Vertical(g2)
    c: Coincident(g3,g2)
    c: InternalAlignment(g5-g8 -> g4) x4
    c: Horizontal(g5)
    c: PointOnObject(g4,g2)
    c: Coincident(g4,g1)
    c: DistanceX(g-3,g5) = 19.1
    c: Coincident(g4,g2)
    c: Coincident(g9,g1)
    c: Coincident(g9,g1)
    c: Coincident(g10,g1)
    c: Coincident(g10,g0)
    c: PointOnObject(g11,g-6)
    c: PointOnObject(g1,g11)
    c: DistanceY(g2,g1) = 19
    c: Coincident(g10,g-4)
    c: PointOnObject(g12,g4)
    c: PointOnObject(g12,g3)
    c: Tangent(g11,g-5) = -1.5708
    c: Tangent(g0,g-5) = -1.5708
    c: Tangent(g3,g0) = 1.5708
    c: PointOnObject(g13,g4)
    c: PointOnObject(g13,g3)
    c: Tangent(g4,g3,g13) = 1.5708
    c: Horizontal(g11,g0)
FEATURE [Part::Part2DObjectPython] Clone2D  label="Sketch108 (2D)"  # Draft 2D object (typed FeaturePython)
  Fuse = false
  Objects = -> [Sketch108]
  Placement = pos=(0,2,4e-16) rot=(0,0.707107,0.707107;3.14159rad)
  Scale = (1,1,1)
FEATURE [Sketcher::SketchObject] Sketch109
  ArcFitTolerance = 1e-06
  AttachmentOffset = pos=(0,0,-3.8) rot=(0,0,1;0rad)
  AttachmentSupport = -> [Pad008]
  ExternalGeometry = -> [Binder]
  FullyConstrained = true
  MakeInternals = false
  MapMode = 5
  Placement = pos=(0,-0.2,8e-16) rot=(0,0.707107,0.707107;3.14159rad)
  sketch-geometry (1):
    g0: GeomPoint X=197.47 Y=8.55923 Z=0
  constraints (1):
    c: Symmetric(g-7,g-5,g0)
FEATURE [PartDesign::SubtractiveLoft] SubtractiveLoft
  BaseFeature = -> SubtractivePipe001
  Closed = false
  Profile = -> Sketch099
  Refine = true
  Ruled = false
  Sections = -> [Sketch108]
  Suppressed = false
FEATURE [PartDesign::SubtractiveLoft] SubtractiveLoft001
  BaseFeature = -> SubtractiveLoft
  Closed = false
  Profile = -> Clone2D
  Refine = true
  Ruled = false
  Sections = -> [Sketch109]
  Suppressed = false
FEATURE [PartDesign::Chamfer] Chamfer001
  Angle = 45
  Base = -> SubtractiveLoft001 [Edge122,Edge121,Edge118,Edge116,Edge114,Edge113,Edge170,Edge80,Edge76]
  BaseFeature = -> SubtractiveLoft001
  ChamferType = 0
  FlipDirection = false
  Refine = true
  Size = 1.9
  Size2 = 1
  SupportTransform = false
  Suppressed = false
  UseAllEdges = false
FEATURE [PartDesign::Chamfer] Chamfer002
  Angle = 45
  Base = -> Chamfer001 [Edge95,Edge34]
  BaseFeature = -> Chamfer001
  ChamferType = 0
  FlipDirection = false
  Refine = true
  Size = 3.5
  Size2 = 1
  SupportTransform = false
  Suppressed = false
  UseAllEdges = false
FEATURE [PartDesign::Chamfer] Chamfer003
  Angle = 45
  Base = -> Chamfer002 [Edge85]
  BaseFeature = -> Chamfer002
  ChamferType = 0
  FlipDirection = false
  Refine = true
  Size = 1.5
  Size2 = 1
  SupportTransform = false
  Suppressed = false
  UseAllEdges = false
FEATURE [PartDesign::Chamfer] Chamfer004
  Angle = 45
  Base = -> Chamfer003 [Edge18,Edge19,Edge17,Edge20]
  BaseFeature = -> Chamfer003
  ChamferType = 0
  FlipDirection = false
  Refine = true
  Size = 1.5
  Size2 = 1
  SupportTransform = false
  Suppressed = false
  UseAllEdges = false
FEATURE [PartDesign::Chamfer] Chamfer005
  Angle = 45
  Base = -> Chamfer004 [Edge227,Edge224]
  BaseFeature = -> Chamfer004
  ChamferType = 1
  FlipDirection = false
  Refine = true
  Size = 1.5
  Size2 = 2.8
  SupportTransform = false
  Suppressed = false
  UseAllEdges = false
FEATURE [PartDesign::Chamfer] Chamfer006
  Angle = 45
  Base = -> Chamfer005 [Edge223]
  BaseFeature = -> Chamfer005
  ChamferType = 1
  FlipDirection = false
  Refine = true
  Size = 6
  Size2 = 1
  SupportTransform = false
  Suppressed = false
  UseAllEdges = false
FEATURE [PartDesign::Fillet] Fillet002
  Base = -> Chamfer006 [Edge150]
  BaseFeature = -> Chamfer006
  Radius = 1.9
  Refine = true
  SupportTransform = false
  Suppressed = false
  UseAllEdges = false
FEATURE [PartDesign::Fillet] Fillet003
  Base = -> Fillet002 [Edge6]
  BaseFeature = -> Fillet002
  Radius = 1.1
  Refine = true
  SupportTransform = false
  Suppressed = false
  UseAllEdges = false
FEATURE [PartDesign::Fillet] Fillet004
  Base = -> Fillet003 [Edge45]
  BaseFeature = -> Fillet003
  Radius = 1.9
  Refine = true
  SupportTransform = false
  Suppressed = false
  UseAllEdges = false
FEATURE [PartDesign::Fillet] Fillet005
  Base = -> Fillet004 [Edge1]
  BaseFeature = -> Fillet004
  Radius = 1
  Refine = true
  SupportTransform = false
  Suppressed = false
  UseAllEdges = false
FEATURE [PartDesign::Chamfer] Chamfer007
  Angle = 45
  Base = -> Fillet005 [Edge29]
  BaseFeature = -> Fillet005
  ChamferType = 0
  FlipDirection = false
  Refine = true
  Size = 1.9
  Size2 = 1
  SupportTransform = false
  Suppressed = false
  UseAllEdges = false
FEATURE [PartDesign::Fillet] Fillet006
  Base = -> Chamfer007 [Edge339,Edge338]
  BaseFeature = -> Chamfer007
  Radius = 5
  Refine = true
  SupportTransform = false
  Suppressed = false
  UseAllEdges = false
FEATURE [Sketcher::SketchObject] Sketch110
  ArcFitTolerance = 1e-06
  AttachmentSupport = -> [Pad010]
  ExternalGeometry = -> [Sketch098]
  FullyConstrained = true
  MakeInternals = false
  MapMode = 5
  Placement = pos=(0,4,-9e-16) rot=(0,0.707107,0.707107;3.14159rad)
  sketch-geometry (8):
    g0: LineSegment StartX=119.69 StartY=34 StartZ=0 EndX=130.69 EndY=34 EndZ=0
    g1: LineSegment StartX=119.95 StartY=33.2 StartZ=0 EndX=130.95 EndY=33.2 EndZ=0
    g2: LineSegment StartX=119.137 StartY=35.7 StartZ=0 EndX=130.137 EndY=35.7 EndZ=0
    g3: LineSegment StartX=118.877 StartY=36.5 StartZ=0 EndX=129.877 EndY=36.5 EndZ=0
    g4: LineSegment StartX=118.877 StartY=36.5 StartZ=0 EndX=119.137 EndY=35.7 EndZ=0
    g5: LineSegment StartX=129.877 StartY=36.5 StartZ=0 EndX=130.137 EndY=35.7 EndZ=0
    g6: LineSegment StartX=119.69 StartY=34 StartZ=0 EndX=119.95 EndY=33.2 EndZ=0
    g7: LineSegment StartX=130.69 StartY=34 StartZ=0 EndX=130.95 EndY=33.2 EndZ=0
  constraints (24):
    c: Horizontal(g0)
    c: Horizontal(g1)
    c: Horizontal(g2)
    c: Horizontal(g3)
    c: Equal(g1,g-5)
    c: Equal(g0,g-5)
    c: Equal(g2,g-5)
    c: Equal(g3,g-5)
    c: PointOnObject(g0,g-3)
    c: PointOnObject(g1,g-3)
    c: PointOnObject(g2,g-3)
    c: PointOnObject(g3,g-3)
    c: Coincident(g4,g3)
    c: Coincident(g4,g2)
    c: Coincident(g5,g3)
    c: Coincident(g5,g2)
    c: Coincident(g6,g0)
    c: Coincident(g6,g1)
    c: Coincident(g7,g0)
    c: Coincident(g7,g1)
    c: DistanceY(g1,g0) = 0.8
    c: DistanceY(g2,g3) = 0.8
    c: DistanceY(g-5,g1) = 2
    c: DistanceY(g-5,g2) = 4.5
FEATURE [PartDesign::Pocket] Pocket003
  BaseFeature = -> Fillet006
  Direction = (0,-1,2e-16)
  Length = 1
  Length2 = 5
  Profile = -> Sketch110
  ReferenceAxis = -> Sketch110 [N_Axis]
  Refine = true
  Suppressed = false
  Type = 0
FEATURE [Sketcher::SketchObject] Sketch111
  ArcFitTolerance = 1e-06
  AttachmentSupport = -> [Pad009]
  ExternalGeometry = -> [Pad009]
  FullyConstrained = true
  MakeInternals = false
  MapMode = 5
  Placement = pos=(0,3.6,-8e-16) rot=(0,0.707107,0.707107;3.14159rad)
  sketch-geometry (21):
    g0: LineSegment [constr] StartX=97 StartY=36.8 StartZ=0 EndX=97 EndY=26.8 EndZ=0
    g1: LineSegment StartX=97 StartY=28.6 StartZ=0 EndX=97 EndY=27.8 EndZ=0
    g2: LineSegment StartX=97 StartY=27.8 StartZ=0 EndX=108 EndY=27.8 EndZ=0
    g3: LineSegment StartX=108 StartY=27.8 StartZ=0 EndX=108 EndY=28.6 EndZ=0
    g4: LineSegment StartX=108 StartY=28.6 StartZ=0 EndX=97 EndY=28.6 EndZ=0
    g5: LineSegment StartX=97 StartY=35.8 StartZ=0 EndX=97 EndY=35 EndZ=0
    g6: LineSegment StartX=97 StartY=35 StartZ=0 EndX=108 EndY=35 EndZ=0
    g7: LineSegment StartX=108 StartY=35 StartZ=0 EndX=108 EndY=35.8 EndZ=0
    g8: LineSegment StartX=108 StartY=35.8 StartZ=0 EndX=97 EndY=35.8 EndZ=0
    g9: LineSegment StartX=97 StartY=30.4 StartZ=0 EndX=97 EndY=29.6 EndZ=0
    g10: LineSegment StartX=97 StartY=29.6 StartZ=0 EndX=108 EndY=29.6 EndZ=0
    g11: LineSegment StartX=108 StartY=29.6 StartZ=0 EndX=108 EndY=30.4 EndZ=0
    g12: LineSegment StartX=108 StartY=30.4 StartZ=0 EndX=97 EndY=30.4 EndZ=0
    g13: LineSegment StartX=97 StartY=34 StartZ=0 EndX=97 EndY=33.2 EndZ=0
    g14: LineSegment StartX=97 StartY=33.2 StartZ=0 EndX=108 EndY=33.2 EndZ=0
    g15: LineSegment StartX=108 StartY=33.2 StartZ=0 EndX=108 EndY=34 EndZ=0
    g16: LineSegment StartX=108 StartY=34 StartZ=0 EndX=97 EndY=34 EndZ=0
    g17: LineSegment StartX=97 StartY=32.2 StartZ=0 EndX=97 EndY=31.4 EndZ=0
    g18: LineSegment StartX=97 StartY=31.4 StartZ=0 EndX=108 EndY=31.4 EndZ=0
    g19: LineSegment StartX=108 StartY=31.4 StartZ=0 EndX=108 EndY=32.2 EndZ=0
    g20: LineSegment StartX=108 StartY=32.2 StartZ=0 EndX=97 EndY=32.2 EndZ=0
  constraints (54):
    c: Vertical(g0)
    c: PointOnObject(g0,g-3)
    c: PointOnObject(g0,g-4)
    c: DistanceX(g0,g-5) = 11
    c: Coincident(g1,g2)
    c: Coincident(g2,g3)
    c: Coincident(g3,g4)
    c: Coincident(g4,g1)
    c: Horizontal(g2)
    c: Horizontal(g4)
    c: Tangent(g1,g0)
    c: Tangent(g3,g-5)
    c: DistanceY(g2,g3) = 0.8
    c: Coincident(g5,g6)
    c: Coincident(g6,g7)
    c: Coincident(g7,g8)
    c: Coincident(g8,g5)
    c: Horizontal(g6)
    c: Horizontal(g8)
    c: DistanceY(g6,g7) = 0.8
    c: Coincident(g9,g10)
    c: Coincident(g10,g11)
    c: Coincident(g11,g12)
    c: Coincident(g12,g9)
    c: Horizontal(g10)
    c: Horizontal(g12)
    c: DistanceY(g10,g11) = 0.8
    c: Tangent(g5,g0)
    c: Tangent(g7,g-5)
    c: Tangent(g9,g0)
    c: Tangent(g11,g-5)
    c: Coincident(g13,g14)
    c: Coincident(g14,g15)
    c: Coincident(g15,g16)
    c: Coincident(g16,g13)
    c: Horizontal(g14)
    c: Horizontal(g16)
    c: DistanceY(g14,g15) = 0.8
    c: Tangent(g13,g0)
    c: Tangent(g15,g-5)
    c: Coincident(g17,g18)
    c: Coincident(g18,g19)
    c: Coincident(g19,g20)
    c: Coincident(g20,g17)
    c: Horizontal(g18)
    c: Horizontal(g20)
    c: DistanceY(g18,g19) = 0.8
    c: Tangent(g17,g0)
    c: Tangent(g19,g-5)
    c: DistanceY(g1,g9) = 1
    c: DistanceY(g9,g17) = 1
    c: DistanceY(g17,g13) = 1
    c: DistanceY(g13,g5) = 1
    c: DistanceY(g0,g1) = 1
FEATURE [PartDesign::Pocket] Pocket004
  BaseFeature = -> Pocket003
  Direction = (0,-1,2e-16)
  Length = 1
  Length2 = 5
  Profile = -> Sketch111
  ReferenceAxis = -> Sketch111 [N_Axis]
  Refine = true
  Suppressed = false
  Type = 0
FEATURE [Sketcher::SketchObject] Sketch112
  ArcFitTolerance = 1e-06
  AttachmentSupport = -> [Pad008]
  ExternalGeometry = -> [Binder]
  FullyConstrained = true
  MakeInternals = false
  MapMode = 5
  Placement = pos=(0,3.6,0) rot=(0,0.707107,0.707107;3.14159rad)
  sketch-geometry (4):
    g0: LineSegment [constr] StartX=167.782 StartY=-53.0314 StartZ=0 EndX=215.42 EndY=-53.0314 EndZ=0
    g1: GeomPoint [constr] X=191.282 Y=-53.0314 Z=0
    g2: Circle CenterX=191.282 CenterY=-53.0314 CenterZ=0 NormalX=0 NormalY=0 NormalZ=1 AngleXU=0 Radius=11.5
    g3: Circle CenterX=191.282 CenterY=-53.0314 CenterZ=0 NormalX=0 NormalY=0 NormalZ=1 AngleXU=0 Radius=10.7
  constraints (9):
    c: Horizontal(g0)
    c: PointOnObject(g0,g-3)
    c: Diameter(g2) = 23
    c: Coincident(g2,g1)
    c: Diameter(g3) = 21.4
    c: Coincident(g3,g1)
    c: DistanceX(g0,g1) = 23.5
    c: PointOnObject(g1,g0)
    c: Coincident(g0,g-4)
FEATURE [PartDesign::Pocket] Pocket005
  BaseFeature = -> Pocket004
  Direction = (0,-1,2e-16)
  Length = 0.8
  Length2 = 5
  Profile = -> Sketch112
  ReferenceAxis = -> Sketch112 [N_Axis]
  Refine = true
  Suppressed = false
  Type = 0
FEATURE [Part::Mirroring] Part__Mirroring  label="Pocket005 (Mirror #1)"
  Base = (0,0,0)
  Normal = (0,0,1)
  Source = -> Pocket005
FEATURE [Sketcher::SketchObject] Sketch113
  ArcFitTolerance = 1e-06
  AttachmentSupport = -> [Pocket005]
  FullyConstrained = true
  MakeInternals = false
  MapMode = 5
  Placement = pos=(0,3.6,0) rot=(0,0.707107,0.707107;3.14159rad)
FEATURE [PartDesign::Body] Body006  label="lato SX"
  AllowCompound = false
  Group = -> [Binder,Pad004,Sketch091,Pad005,Sketch092,Pocket001,Sketch093,Pocket002,Sketch094,Pad006,Sketch095,Pad007,Sketch096,Pad008,Sketch097,Pad009,Sketch098,Pad010,SubtractivePipe,SubtractivePipe001,Sketch099,Sketch106,Sketch107,Sketch108,Clone2D,Sketch109,SubtractiveLoft,SubtractiveLoft001,Chamfer001,Chamfer002,Chamfer003,Chamfer004,Chamfer005,Chamfer006,Fillet002,Fillet003,Fillet004,Fillet005,+9 more]
  Origin = -> Origin006
  Tip = -> Pocket005
FEATURE [Mesh::Feature] logo_per_PCB_definitivo_positivo
  Placement = pos=(-191,17,-66) rot=(0,1,1;0rad)
FEATURE [Sketcher::SketchObject] Sketch114  label="Sketch114 - base lato DX"
  ArcFitTolerance = 1e-06
  AttachmentSupport = -> [Binder001]
  ExternalGeometry = -> [Binder001]
  FullyConstrained = true
  MakeInternals = false
  MapMode = 5
  Placement = pos=(0,1e-15,0) rot=(0,0.707107,0.707107;3.14159rad)
  sketch-geometry (28):
    g0: Circle CenterX=5.6 CenterY=34.8 CenterZ=0 NormalX=0 NormalY=0 NormalZ=1 AngleXU=0 Radius=1.8
    g1: Circle CenterX=5.6 CenterY=7.6 CenterZ=0 NormalX=0 NormalY=0 NormalZ=1 AngleXU=0 Radius=1.8
    g2: Circle CenterX=24.2 CenterY=26.7 CenterZ=0 NormalX=0 NormalY=0 NormalZ=1 AngleXU=0 Radius=3
    g3: Circle CenterX=24.2 CenterY=15.7 CenterZ=0 NormalX=0 NormalY=0 NormalZ=1 AngleXU=0 Radius=3
    g4: Circle CenterX=36.2 CenterY=21.2 CenterZ=0 NormalX=0 NormalY=0 NormalZ=1 AngleXU=0 Radius=2.8
    g5: Circle CenterX=78.51 CenterY=34.8 CenterZ=0 NormalX=0 NormalY=0 NormalZ=1 AngleXU=0 Radius=1.8
    g6: Circle CenterX=78.51 CenterY=7.6 CenterZ=0 NormalX=0 NormalY=0 NormalZ=1 AngleXU=0 Radius=1.8
    g7: Circle CenterX=184.08 CenterY=34.8 CenterZ=0 NormalX=0 NormalY=0 NormalZ=1 AngleXU=0 Radius=1.8
    g8: Circle CenterX=213.443 CenterY=-76.8316 CenterZ=0 NormalX=0 NormalY=0 NormalZ=1 AngleXU=0 Radius=1.8
    g9: Circle CenterX=179.305 CenterY=-76.8316 CenterZ=0 NormalX=0 NormalY=0 NormalZ=1 AngleXU=0 Radius=1.8
    g10: ArcOfCircle CenterX=132.428 CenterY=4 CenterZ=0 NormalX=0 NormalY=0 NormalZ=1 AngleXU=0 Radius=16 StartAngle=0.314159 EndAngle=1.5708
    g11: ArcOfCircle CenterX=107.6 CenterY=4 CenterZ=0 NormalX=0 NormalY=0 NormalZ=1 AngleXU=0 Radius=16 StartAngle=1.5708 EndAngle=3.00366
    g12: ArcOfCircle CenterX=207.583 CenterY=4 CenterZ=0 NormalX=0 NormalY=0 NormalZ=1 AngleXU=0 Radius=17 StartAngle=1.85815 EndAngle=3.57792
    g13: ArcOfCircle CenterX=184.801 CenterY=-67.3089 CenterZ=0 NormalX=0 NormalY=0 NormalZ=1 AngleXU=0 Radius=33.7833 StartAngle=5.88425 EndAngle=6.71952
    g14: LineSegment StartX=0 StartY=39.2 StartZ=0 EndX=0 EndY=3.2 EndZ=0
    g15: LineSegment StartX=0 StartY=3.2 StartZ=0 EndX=82.8 EndY=3.2 EndZ=0
    g16: LineSegment StartX=82.8 StartY=3.2 StartZ=0 EndX=82.8 EndY=6.2 EndZ=0
    g17: LineSegment StartX=82.8 StartY=6.2 StartZ=0 EndX=91.752 EndY=6.2 EndZ=0
    g18: LineSegment StartX=107.6 StartY=20 StartZ=0 EndX=132.428 EndY=20 EndZ=0
    g19: LineSegment StartX=147.645 StartY=8.94427 StartZ=0 EndX=176.685 EndY=-80.4316 EndZ=0
    g20: LineSegment StartX=176.685 StartY=-80.4316 StartZ=0 EndX=215.932 EndY=-80.4316 EndZ=0
    g21: LineSegment StartX=215.42 StartY=-53.0314 StartZ=0 EndX=192.176 EndY=-3.18451 EndZ=0
    g22: LineSegment StartX=202.765 StartY=20.303 StartZ=0 EndX=195.887 EndY=39.2 EndZ=0
    g23: LineSegment StartX=195.887 StartY=39.2 StartZ=0 EndX=0 EndY=39.2 EndZ=0
    g24: LineSegment StartX=196.467 StartY=26.4942 StartZ=0 EndX=194.073 EndY=33.0721 EndZ=0
    g25: LineSegment StartX=194.073 StartY=33.0721 StartZ=0 EndX=189.939 EndY=31.5672 EndZ=0
    g26: LineSegment StartX=189.939 StartY=31.5672 StartZ=0 EndX=192.333 EndY=24.9893 EndZ=0
    g27: LineSegment StartX=192.333 StartY=24.9893 StartZ=0 EndX=196.467 EndY=26.4942 EndZ=0
  constraints (60):
    c: Equal(g0,g-25)
    c: Equal(g2,g-29)
    c: Equal(g3,g-30)
    c: Equal(g4,g-28)
    c: Equal(g1,g-26)
    c: Coincident(g0,g-25)
    c: Coincident(g1,g-26)
    c: Coincident(g2,g-29)
    c: Coincident(g3,g-30)
    c: Coincident(g4,g-28)
    c: Equal(g5,g-23)
    c: Equal(g6,g-24)
    c: Coincident(g5,g-23)
    c: Coincident(g6,g-24)
    c: Equal(g7,g-20)
    c: Coincident(g7,g-20)
    c: Equal(g9,g-22)
    c: Coincident(g9,g-22)
    c: Equal(g8,g-21)
    c: Coincident(g8,g-21)
    c: Equal(g13,g-12)
    c: Equal(g12,g-14)
    c: Equal(g10,g-9)
    c: Equal(g11,g-7)
    c: Coincident(g14,g-27)
    c: Coincident(g14,g-27)
    c: Coincident(g15,g14)
    c: Coincident(g15,g-5)
    c: Coincident(g16,g15)
    c: Coincident(g16,g-6)
    c: Coincident(g17,g16)
    c: Coincident(g17,g-7)
    c: Coincident(g11,g17)
    c: Coincident(g11,g-8)
    c: Coincident(g18,g11)
    c: Coincident(g18,g-9)
    c: Coincident(g10,g18)
    c: Coincident(g10,g-10)
    c: Coincident(g19,g10)
    c: Coincident(g19,g-11)
    c: Coincident(g20,g19)
    c: Coincident(g20,g-12)
    c: Coincident(g13,g20)
    c: Coincident(g13,g-13)
    c: Coincident(g21,g13)
    c: Coincident(g21,g-14)
    c: Coincident(g12,g21)
    c: Coincident(g12,g-15)
    c: Coincident(g22,g12)
    c: Coincident(g22,g-15)
    c: Coincident(g23,g22)
    c: Coincident(g23,g14)
    c: Coincident(g24,g-18)
    c: Coincident(g24,g-16)
    c: Coincident(g25,g24)
    c: Coincident(g25,g-19)
    c: Coincident(g26,g25)
    c: Coincident(g26,g-19)
    c: Coincident(g27,g26)
    c: Coincident(g27,g24)
FEATURE [PartDesign::Pad] Pad011
  Direction = (0,1,-2e-16)
  Length = 2
  Length2 = 10
  Profile = -> Sketch114
  ReferenceAxis = -> Sketch114 [N_Axis]
  Refine = true
  Reversed = true
  Suppressed = false
  Type = 0
FEATURE [Sketcher::SketchObject] Sketch115
  ArcFitTolerance = 1e-06
  AttachmentSupport = -> [Pad011]
  ExternalGeometry = -> [Binder001]
  FullyConstrained = true
  MakeInternals = false
  MapMode = 5
  Placement = pos=(0,1.1e-15,0) rot=(0,0.707107,0.707107;3.14159rad)
  sketch-geometry (4):
    g0: ArcOfCircle CenterX=24.2 CenterY=26.7 CenterZ=0 NormalX=0 NormalY=0 NormalZ=1 AngleXU=0 Radius=3 StartAngle=4.48384e-08 EndAngle=3.14159
    g1: ArcOfCircle CenterX=24.2 CenterY=15.7 CenterZ=0 NormalX=0 NormalY=0 NormalZ=1 AngleXU=0 Radius=3 StartAngle=3.14159 EndAngle=6.28318
    g2: LineSegment StartX=21.2 StartY=26.7 StartZ=0 EndX=21.2 EndY=15.7 EndZ=0
    g3: LineSegment StartX=27.2 StartY=26.7 StartZ=0 EndX=27.2 EndY=15.7 EndZ=0
  constraints (12):
    c: Equal(g1,g-4)
    c: Equal(g0,g-3)
    c: Coincident(g0,g-3)
    c: Coincident(g1,g-4)
    c: Vertical(g2)
    c: Vertical(g3)
    c: Tangent(g3,g-3)
    c: Tangent(g2,g-3)
    c: Coincident(g0,g2)
    c: Coincident(g0,g3)
    c: Coincident(g1,g2)
    c: Coincident(g3,g1)
FEATURE [PartDesign::Pocket] Pocket006
  BaseFeature = -> Pad011
  Direction = (0,-1,2e-16)
  Length = 1.2
  Length2 = 5
  Profile = -> Sketch115
  ReferenceAxis = -> Sketch115 [N_Axis]
  Refine = true
  Suppressed = false
  Type = 0
FEATURE [Sketcher::SketchObject] Sketch116
  ArcFitTolerance = 1e-06
  AttachmentSupport = -> [Pocket006]
  ExternalGeometry = -> [Binder001]
  FullyConstrained = true
  MakeInternals = false
  MapMode = 5
  Placement = pos=(0,1.1e-15,0) rot=(0,0.707107,0.707107;3.14159rad)
  sketch-geometry (4):
    g0: Circle CenterX=43.2 CenterY=30.3 CenterZ=0 NormalX=0 NormalY=0 NormalZ=1 AngleXU=0 Radius=3.4
    g1: Circle CenterX=43.2 CenterY=12.1 CenterZ=0 NormalX=0 NormalY=0 NormalZ=1 AngleXU=0 Radius=3.4
    g2: Circle CenterX=18.6 CenterY=30.3 CenterZ=0 NormalX=0 NormalY=0 NormalZ=1 AngleXU=0 Radius=3.4
    g3: Circle CenterX=18.6 CenterY=12.1 CenterZ=0 NormalX=0 NormalY=0 NormalZ=1 AngleXU=0 Radius=3.4
  constraints (8):
    c: Diameter(g0) = 6.8
    c: Diameter(g1) = 6.8
    c: Diameter(g2) = 6.8
    c: Diameter(g3) = 6.8
    c: Coincident(g2,g-3)
    c: Coincident(g0,g-4)
    c: Coincident(g3,g-6)
    c: Coincident(g1,g-5)
FEATURE [PartDesign::Pad] Pad012
  BaseFeature = -> Pocket006
  Direction = (0,1,-2e-16)
  Length = 2.4
  Length2 = 10
  Profile = -> Sketch116
  ReferenceAxis = -> Sketch116 [N_Axis]
  Refine = true
  Suppressed = false
  Type = 0
FEATURE [Sketcher::SketchObject] Sketch117
  ArcFitTolerance = 1e-06
  AttachmentSupport = -> [Pad011]
  ExternalGeometry = -> [Binder001]
  FullyConstrained = true
  MakeInternals = false
  MapMode = 5
  Placement = pos=(0,1.1e-15,0) rot=(0,0.707107,0.707107;3.14159rad)
  sketch-geometry (4):
    g0: Circle CenterX=43.2 CenterY=30.3 CenterZ=0 NormalX=0 NormalY=0 NormalZ=1 AngleXU=0 Radius=2.25
    g1: Circle CenterX=43.2 CenterY=12.1 CenterZ=0 NormalX=0 NormalY=0 NormalZ=1 AngleXU=0 Radius=2.25
    g2: Circle CenterX=18.6 CenterY=30.3 CenterZ=0 NormalX=0 NormalY=0 NormalZ=1 AngleXU=0 Radius=2.25
    g3: Circle CenterX=18.6 CenterY=12.1 CenterZ=0 NormalX=0 NormalY=0 NormalZ=1 AngleXU=0 Radius=2.25
  constraints (8):
    c: Diameter(g0) = 4.5
    c: Diameter(g1) = 4.5
    c: Diameter(g2) = 4.5
    c: Diameter(g3) = 4.5
    c: Coincident(g2,g-3)
    c: Coincident(g3,g-6)
    c: Coincident(g0,g-4)
    c: Coincident(g1,g-5)
FEATURE [PartDesign::Pocket] Pocket007
  BaseFeature = -> Pad012
  Direction = (0,-1,2e-16)
  Length = 0.6
  Length2 = 2.4
  Profile = -> Sketch117
  ReferenceAxis = -> Sketch117 [N_Axis]
  Refine = true
  Suppressed = false
  Type = 4
FEATURE [Sketcher::SketchObject] Sketch118
  ArcFitTolerance = 1e-06
  AttachmentSupport = -> [Pad011]
  ExternalGeometry = -> [Binder001]
  FullyConstrained = true
  MakeInternals = false
  MapMode = 5
  Placement = pos=(0,-2,4e-16) rot=(1,0,0;1.5708rad)
  sketch-geometry (12):
    g0: Circle CenterX=-78.51 CenterY=34.8 CenterZ=0 NormalX=0 NormalY=0 NormalZ=1 AngleXU=0 Radius=1.8
    g1: Circle CenterX=-78.51 CenterY=7.6 CenterZ=0 NormalX=0 NormalY=0 NormalZ=1 AngleXU=0 Radius=1.8
    g2: Circle CenterX=-5.6 CenterY=34.8 CenterZ=0 NormalX=0 NormalY=0 NormalZ=1 AngleXU=0 Radius=1.8
    g3: Circle CenterX=-5.6 CenterY=7.6 CenterZ=0 NormalX=0 NormalY=0 NormalZ=1 AngleXU=0 Radius=1.8
    g4: LineSegment StartX=0 StartY=39.2 StartZ=0 EndX=0 EndY=3.2 EndZ=0
    g5: LineSegment StartX=0 StartY=3.2 StartZ=0 EndX=-82.8 EndY=3.2 EndZ=0
    g6: LineSegment StartX=-82.8 StartY=3.2 StartZ=0 EndX=-82.8 EndY=39.2 EndZ=0
    g7: LineSegment StartX=-82.8 StartY=39.2 StartZ=0 EndX=0 EndY=39.2 EndZ=0
    g8: ArcOfCircle CenterX=-65 CenterY=21.2 CenterZ=0 NormalX=0 NormalY=0 NormalZ=1 AngleXU=0 Radius=10 StartAngle=1.5708 EndAngle=4.71239
    g9: ArcOfCircle CenterX=-19 CenterY=21.2 CenterZ=0 NormalX=0 NormalY=0 NormalZ=1 AngleXU=0 Radius=10 StartAngle=4.71239 EndAngle=7.85398
    g10: LineSegment StartX=-65 StartY=31.2 StartZ=0 EndX=-19 EndY=31.2 EndZ=0
    g11: LineSegment StartX=-65 StartY=11.2 StartZ=0 EndX=-19 EndY=11.2 EndZ=0
  constraints (25):
    c: Equal(g2,g-5)
    c: Equal(g3,g-7)
    c: Equal(g1,g-6)
    c: Equal(g0,g-4)
    c: Coincident(g0,g-4)
    c: Coincident(g1,g-6)
    c: Coincident(g3,g-7)
    c: Coincident(g2,g-5)
    c: Coincident(g4,g-8)
    c: Coincident(g4,g-9)
    c: Coincident(g5,g4)
    c: Coincident(g5,g-10)
    c: Coincident(g6,g5)
    c: PointOnObject(g6,g-3)
    c: Vertical(g6)
    c: Coincident(g7,g6)
    c: Coincident(g7,g4)
    c: Tangent(g8,g10) = 1.5708
    c: Tangent(g8,g11) = -1.5708
    c: Tangent(g9,g10) = 1.5708
    c: Tangent(g9,g11) = -1.5708
    c: Equal(g8,g9)
    c: Radius(g8) = 10
    c: Coincident(g8,g-11)
    c: Coincident(g9,g-12)
FEATURE [PartDesign::Pad] Pad013
  BaseFeature = -> Pocket007
  Direction = (0,-1,2e-16)
  Length = 1.6
  Length2 = 10
  Profile = -> Sketch118
  ReferenceAxis = -> Sketch118 [N_Axis]
  Refine = true
  Suppressed = false
  Type = 0
FEATURE [Sketcher::SketchObject] Sketch119
  ArcFitTolerance = 1e-06
  AttachmentSupport = -> [Pad013]
  ExternalGeometry = -> [Binder001]
  FullyConstrained = true
  MakeInternals = false
  MapMode = 5
  Placement = pos=(0,-3.6,0) rot=(1,0,0;1.5708rad)
  sketch-geometry (21):
    g0: LineSegment [constr] StartX=-82.8 StartY=3.2 StartZ=0 EndX=-82.8 EndY=39.2 EndZ=0
    g1: ArcOfCircle CenterX=-78.51 CenterY=34.8 CenterZ=0 NormalX=0 NormalY=0 NormalZ=1 AngleXU=0 Radius=3.5 StartAngle=4.71239 EndAngle=6.28319
    g2: ArcOfCircle CenterX=-78.51 CenterY=7.6 CenterZ=0 NormalX=0 NormalY=0 NormalZ=1 AngleXU=0 Radius=3.5 StartAngle=0 EndAngle=1.5708
    g3: ArcOfCircle CenterX=-5.6 CenterY=34.8 CenterZ=0 NormalX=0 NormalY=0 NormalZ=1 AngleXU=0 Radius=3.5 StartAngle=3.14159 EndAngle=4.71239
    g4: ArcOfCircle CenterX=-5.6 CenterY=7.6 CenterZ=0 NormalX=0 NormalY=0 NormalZ=1 AngleXU=0 Radius=3.5 StartAngle=1.5708 EndAngle=3.14159
    g5: LineSegment StartX=0 StartY=39.2 StartZ=0 EndX=0 EndY=31.3 EndZ=0
    g6: LineSegment StartX=0 StartY=39.2 StartZ=0 EndX=-9.1 EndY=39.2 EndZ=0
    g7: LineSegment StartX=0 StartY=3.2 StartZ=0 EndX=0 EndY=11.1 EndZ=0
    g8: LineSegment StartX=0 StartY=3.2 StartZ=0 EndX=-9.1 EndY=3.2 EndZ=0
    g9: LineSegment StartX=-82.8 StartY=3.2 StartZ=0 EndX=-75.01 EndY=3.2 EndZ=0
    g10: LineSegment StartX=-82.8 StartY=3.2 StartZ=0 EndX=-82.8 EndY=11.1 EndZ=0
    g11: LineSegment StartX=-82.8 StartY=39.2 StartZ=0 EndX=-82.8 EndY=31.3 EndZ=0
    g12: LineSegment StartX=-82.8 StartY=39.2 StartZ=0 EndX=-75.01 EndY=39.2 EndZ=0
    g13: LineSegment StartX=-82.8 StartY=31.3 StartZ=0 EndX=-78.51 EndY=31.3 EndZ=0
    g14: LineSegment StartX=-75.01 StartY=39.2 StartZ=0 EndX=-75.01 EndY=34.8 EndZ=0
    g15: LineSegment StartX=-82.8 StartY=11.1 StartZ=0 EndX=-78.51 EndY=11.1 EndZ=0
    g16: LineSegment StartX=-75.01 StartY=3.2 StartZ=0 EndX=-75.01 EndY=7.6 EndZ=0
    g17: LineSegment StartX=-9.1 StartY=39.2 StartZ=0 EndX=-9.1 EndY=34.8 EndZ=0
    g18: LineSegment StartX=0 StartY=31.3 StartZ=0 EndX=-5.6 EndY=31.3 EndZ=0
    g19: LineSegment StartX=0 StartY=11.1 StartZ=0 EndX=-5.6 EndY=11.1 EndZ=0
    g20: LineSegment StartX=-9.1 StartY=3.2 StartZ=0 EndX=-9.1 EndY=7.6 EndZ=0
  constraints (51):
    c: Coincident(g0,g-10)
    c: PointOnObject(g0,g-8)
    c: Vertical(g0)
    c: Coincident(g1,g-3)
    c: Coincident(g2,g-4)
    c: Coincident(g3,g-5)
    c: Coincident(g4,g-6)
    c: Radius(g4) = 3.5
    c: Radius(g3) = 3.5
    c: Radius(g1) = 3.5
    c: Radius(g2) = 3.5
    c: Coincident(g5,g-9)
    c: PointOnObject(g5,g-9)
    c: Coincident(g6,g5)
    c: PointOnObject(g6,g-8)
    c: Coincident(g7,g-9)
    c: PointOnObject(g7,g-9)
    c: Coincident(g8,g7)
    c: PointOnObject(g8,g-7)
    c: Coincident(g9,g0)
    c: PointOnObject(g9,g-7)
    c: Coincident(g10,g0)
    c: PointOnObject(g10,g0)
    c: Coincident(g11,g0)
    c: PointOnObject(g11,g0)
    c: Coincident(g12,g0)
    c: PointOnObject(g12,g-8)
    c: Coincident(g13,g11)
    c: Horizontal(g13)
    c: Coincident(g14,g12)
    c: Vertical(g14)
    c: Coincident(g15,g10)
    c: Horizontal(g15)
    c: Coincident(g16,g9)
    c: Vertical(g16)
    c: Coincident(g17,g6)
    c: Vertical(g17)
    c: Coincident(g18,g5)
    c: Horizontal(g18)
    c: Coincident(g19,g7)
    c: Horizontal(g19)
    c: Coincident(g20,g8)
    c: Vertical(g20)
    c: Tangent(g20,g4) = 1.5708
    c: Tangent(g4,g19) = -1.5708
    c: Tangent(g18,g3) = 1.5708
    c: Tangent(g3,g17) = -1.5708
    c: Tangent(g13,g1) = -1.5708
    c: Tangent(g1,g14) = 1.5708
    c: Tangent(g16,g2) = -1.5708
    c: Tangent(g2,g15) = 1.5708
FEATURE [PartDesign::Pocket] Pocket008
  BaseFeature = -> Pad013
  Direction = (0,1,-2e-16)
  Length = 1.6
  Length2 = 5
  Profile = -> Sketch119
  ReferenceAxis = -> Sketch119 [N_Axis]
  Refine = true
  Suppressed = false
  Type = 0
FEATURE [Sketcher::SketchObject] Sketch120
  ArcFitTolerance = 1e-06
  AttachmentSupport = -> [Pad011]
  ExternalGeometry = -> [Binder001]
  FullyConstrained = true
  MakeInternals = false
  MapMode = 5
  Placement = pos=(0,-2,4e-16) rot=(1,0,0;1.5708rad)
  sketch-geometry (4):
    g0: LineSegment StartX=-137.815 StartY=39.2 StartZ=0 EndX=-142.655 EndY=24.303 EndZ=0
    g1: LineSegment StartX=-137.815 StartY=39.2 StartZ=0 EndX=-110.815 EndY=39.2 EndZ=0
    g2: LineSegment StartX=-142.655 StartY=24.303 StartZ=0 EndX=-110.815 EndY=24.303 EndZ=0
    g3: ArcOfCircle CenterX=-92.2534 CenterY=31.7515 CenterZ=0 NormalX=0 NormalY=0 NormalZ=1 AngleXU=0 Radius=20 StartAngle=2.75997 EndAngle=3.52321
  constraints (12):
    c: PointOnObject(g0,g-3)
    c: Coincident(g1,g0)
    c: PointOnObject(g1,g-3)
    c: Coincident(g2,g0)
    c: Horizontal(g2)
    c: Tangent(g0,g-4)
    c: Vertical(g2,g1)
    c: DistanceX(g1,g1) = 27
    c: DistanceY(g-6,g0) = 4
    c: Radius(g3) = 20
    c: Coincident(g3,g1)
    c: Coincident(g3,g2)
FEATURE [Sketcher::SketchObject] Sketch121
  ArcFitTolerance = 1e-06
  AttachmentSupport = -> [Pad011]
  ExternalGeometry = -> [Binder001]
  FullyConstrained = true
  MakeInternals = false
  MapMode = 5
  Placement = pos=(0,-2,4e-16) rot=(1,0,0;1.5708rad)
  sketch-geometry (15):
    g0: LineSegment StartX=-137.815 StartY=39.2 StartZ=0 EndX=-143.955 EndY=20.303 EndZ=0
    g1: LineSegment StartX=-143.955 StartY=20.303 StartZ=0 EndX=-190.141 EndY=20.303 EndZ=0
    g2: LineSegment StartX=-190.141 StartY=20.303 StartZ=0 EndX=-186.139 EndY=31.3 EndZ=0
    g3: LineSegment StartX=-178.754 StartY=39.2 StartZ=0 EndX=-180.791 EndY=33.6029 EndZ=0
    g4: ArcOfCircle CenterX=-184.08 CenterY=34.8 CenterZ=0 NormalX=0 NormalY=0 NormalZ=1 AngleXU=0 Radius=3.5 StartAngle=4.71239 EndAngle=5.93412
    g5: LineSegment StartX=-184.08 StartY=31.3 StartZ=0 EndX=-186.139 EndY=31.3 EndZ=0
    g6: LineSegment StartX=-137.815 StartY=39.2 StartZ=0 EndX=-156.815 EndY=39.2 EndZ=0
    g7: LineSegment StartX=-168.815 StartY=39.2 StartZ=0 EndX=-178.754 EndY=39.2 EndZ=0
    g8: LineSegment StartX=-157.815 StartY=39.2 StartZ=0 EndX=-167.815 EndY=39.2 EndZ=0
    g9: LineSegment StartX=-168.815 StartY=31.2 StartZ=0 EndX=-156.815 EndY=31.2 EndZ=0
    g10: LineSegment StartX=-167.436 StartY=36.2 StartZ=0 EndX=-157.436 EndY=36.2 EndZ=0
    g11: ArcOfCircle CenterX=-176.411 CenterY=35.2 CenterZ=0 NormalX=0 NormalY=0 NormalZ=1 AngleXU=0 Radius=20 StartAngle=6.08183 EndAngle=6.48454
    g12: ArcOfCircle CenterX=-188.411 CenterY=35.2 CenterZ=0 NormalX=0 NormalY=0 NormalZ=1 AngleXU=0 Radius=20 StartAngle=6.08183 EndAngle=6.48454
    g13: ArcOfCircle CenterX=-177.411 CenterY=35.2 CenterZ=0 NormalX=0 NormalY=0 NormalZ=1 AngleXU=0 Radius=20 StartAngle=0.0500209 EndAngle=0.201358
    g14: ArcOfCircle CenterX=-187.411 CenterY=35.2 CenterZ=0 NormalX=0 NormalY=0 NormalZ=1 AngleXU=0 Radius=20 StartAngle=0.0500209 EndAngle=0.201358
  constraints (46):
    c: PointOnObject(g0,g-3)
    c: Tangent(g0,g-5)
    c: Coincident(g1,g0)
    c: Horizontal(g1)
    c: Coincident(g2,g1)
    c: PointOnObject(g3,g-3)
    c: Parallel(g3,g-6)
    c: Parallel(g2,g-6)
    c: Radius(g4) = 3.5
    c: Coincident(g4,g-7)
    c: Tangent(g3,g4) = 1.5708
    c: Horizontal(g5)
    c: Tangent(g5,g4) = 1.5708
    c: DistanceX(g-8,g5) = 3.8
    c: Coincident(g2,g5)
    c: Coincident(g6,g0)
    c: PointOnObject(g6,g-3)
    c: DistanceX(g6,g6) = 19
    c: PointOnObject(g7,g-3)
    c: DistanceX(g7,g6) = 12
    c: Coincident(g7,g3)
    c: PointOnObject(g8,g-3)
    c: PointOnObject(g8,g-3)
    c: DistanceX(g8,g8) = 10
    c: DistanceX(g8,g6) = 1
    c: Horizontal(g9)
    c: Vertical(g7,g9)
    c: Vertical(g6,g9)
    c: DistanceY(g9,g7) = 8
    c: Horizontal(g10)
    c: Equal(g8,g10)
    c: DistanceY(g10,g8) = 3
    c: Radius(g11) = 20
    c: Coincident(g11,g6)
    c: Coincident(g11,g9)
    c: Radius(g12) = 20
    c: Coincident(g12,g7)
    c: Coincident(g12,g9)
    c: Equal(g13,g11)
    c: Coincident(g13,g8)
    c: Coincident(g13,g10)
    c: Horizontal(g13,g11)
    c: Equal(g14,g12)
    c: Coincident(g14,g8)
    c: Coincident(g14,g10)
    c: Horizontal(g1,g-6)
FEATURE [Sketcher::SketchObject] Sketch122
  ArcFitTolerance = 1e-06
  AttachmentSupport = -> [Pad011]
  ExternalGeometry = -> [Binder001]
  FullyConstrained = true
  MakeInternals = false
  MapMode = 5
  Placement = pos=(0,-2,4e-16) rot=(1,0,0;1.5708rad)
  sketch-geometry (8):
    g0: LineSegment StartX=-202.765 StartY=20.303 StartZ=0 EndX=-143.955 EndY=20.303 EndZ=0
    g1: ArcOfCircle CenterX=-184.801 CenterY=-67.3089 CenterZ=0 NormalX=0 NormalY=0 NormalZ=1 AngleXU=0 Radius=33.7833 StartAngle=2.70526 EndAngle=3.54053
    g2: LineSegment StartX=-176.685 StartY=-80.4316 StartZ=0 EndX=-215.932 EndY=-80.4316 EndZ=0
    g3: LineSegment StartX=-215.42 StartY=-53.0315 StartZ=0 EndX=-192.176 EndY=-3.18454 EndZ=0
    g4: ArcOfCircle CenterX=-207.583 CenterY=4 CenterZ=0 NormalX=0 NormalY=0 NormalZ=1 AngleXU=0 Radius=17 StartAngle=5.84685 EndAngle=7.56663
    g5: Circle CenterX=-213.443 CenterY=-76.8316 CenterZ=0 NormalX=0 NormalY=0 NormalZ=1 AngleXU=0 Radius=3
    g6: Circle CenterX=-179.305 CenterY=-76.8316 CenterZ=0 NormalX=0 NormalY=0 NormalZ=1 AngleXU=0 Radius=3
    g7: LineSegment StartX=-143.955 StartY=20.303 StartZ=0 EndX=-176.685 EndY=-80.4316 EndZ=0
  constraints (18):
    c: Coincident(g0,g-6)
    c: Coincident(g1,g-7)
    c: Coincident(g1,g-8)
    c: Coincident(g2,g1)
    c: Tangent(g3,g-5)
    c: Coincident(g4,g-6)
    c: Coincident(g4,g0)
    c: Coincident(g3,g4)
    c: Coincident(g1,g3)
    c: Diameter(g5) = 6
    c: Diameter(g6) = 6
    c: Coincident(g5,g-9)
    c: Coincident(g6,g-10)
    c: Horizontal(g0)
    c: Horizontal(g2)
    c: Coincident(g7,g0)
    c: Coincident(g7,g2)
    c: Tangent(g7,g-4)
FEATURE [Sketcher::SketchObject] Sketch123
  ArcFitTolerance = 1e-06
  AttachmentSupport = -> [Pad011]
  ExternalGeometry = -> [Binder001]
  FullyConstrained = true
  MakeInternals = false
  MapMode = 5
  Placement = pos=(0,-2,4e-16) rot=(1,0,0;1.5708rad)
  sketch-geometry (4):
    g0: LineSegment StartX=-108 StartY=36.8 StartZ=0 EndX=-90 EndY=36.8 EndZ=0
    g1: LineSegment StartX=-108 StartY=36.8 StartZ=0 EndX=-108 EndY=26.8 EndZ=0
    g2: LineSegment StartX=-108 StartY=26.8 StartZ=0 EndX=-90 EndY=26.8 EndZ=0
    g3: ArcOfCircle CenterX=-94 CenterY=31.8 CenterZ=0 NormalX=0 NormalY=0 NormalZ=1 AngleXU=0 Radius=6.40312 StartAngle=5.38713 EndAngle=7.17924
  constraints (13):
    c: Horizontal(g0)
    c: Coincident(g1,g0)
    c: Vertical(g1)
    c: Coincident(g2,g1)
    c: Horizontal(g2)
    c: DistanceX(g0,g0) = 18
    c: DistanceY(g1,g1) = 10
    c: Equal(g0,g2)
    c: DistanceX(g0,g-3) = 90
    c: DistanceY(g0,g-3) = 2.4
    c: Coincident(g3,g0)
    c: Coincident(g3,g2)
    c: DistanceX(g3,g0) = 4
FEATURE [PartDesign::Pad] Pad017
  BaseFeature = -> Pocket008
  Direction = (0,-1,2e-16)
  Length = 1.6
  Length2 = 10
  Profile = -> Sketch123
  ReferenceAxis = -> Sketch123 [N_Axis]
  Refine = true
  Suppressed = false
  Type = 0
FEATURE [Sketcher::SketchObject] Sketch125
  ArcFitTolerance = 1e-06
  AttachmentSupport = -> [Pad017]
  ExternalGeometry = -> [Pad017]
  FullyConstrained = true
  MakeInternals = false
  MapMode = 5
  Placement = pos=(0,-3.6,8e-16) rot=(1,0,0;1.5708rad)
  sketch-geometry (20):
    g0: LineSegment StartX=-108 StartY=35.8 StartZ=0 EndX=-108 EndY=35 EndZ=0
    g1: LineSegment StartX=-108 StartY=35 StartZ=0 EndX=-97 EndY=35 EndZ=0
    g2: LineSegment StartX=-97 StartY=35 StartZ=0 EndX=-97 EndY=35.8 EndZ=0
    g3: LineSegment StartX=-97 StartY=35.8 StartZ=0 EndX=-108 EndY=35.8 EndZ=0
    g4: LineSegment StartX=-108 StartY=28.6 StartZ=0 EndX=-108 EndY=27.8 EndZ=0
    g5: LineSegment StartX=-108 StartY=27.8 StartZ=0 EndX=-97 EndY=27.8 EndZ=0
    g6: LineSegment StartX=-97 StartY=27.8 StartZ=0 EndX=-97 EndY=28.6 EndZ=0
    g7: LineSegment StartX=-97 StartY=28.6 StartZ=0 EndX=-108 EndY=28.6 EndZ=0
    g8: LineSegment StartX=-108 StartY=30.4 StartZ=0 EndX=-108 EndY=29.6 EndZ=0
    g9: LineSegment StartX=-108 StartY=29.6 StartZ=0 EndX=-97 EndY=29.6 EndZ=0
    g10: LineSegment StartX=-97 StartY=29.6 StartZ=0 EndX=-97 EndY=30.4 EndZ=0
    g11: LineSegment StartX=-97 StartY=30.4 StartZ=0 EndX=-108 EndY=30.4 EndZ=0
    g12: LineSegment StartX=-108 StartY=32.2 StartZ=0 EndX=-108 EndY=31.4 EndZ=0
    g13: LineSegment StartX=-108 StartY=31.4 StartZ=0 EndX=-97 EndY=31.4 EndZ=0
    g14: LineSegment StartX=-97 StartY=31.4 StartZ=0 EndX=-97 EndY=32.2 EndZ=0
    g15: LineSegment StartX=-97 StartY=32.2 StartZ=0 EndX=-108 EndY=32.2 EndZ=0
    g16: LineSegment StartX=-108 StartY=34 StartZ=0 EndX=-108 EndY=33.2 EndZ=0
    g17: LineSegment StartX=-108 StartY=33.2 StartZ=0 EndX=-97 EndY=33.2 EndZ=0
    g18: LineSegment StartX=-97 StartY=33.2 StartZ=0 EndX=-97 EndY=34 EndZ=0
    g19: LineSegment StartX=-97 StartY=34 StartZ=0 EndX=-108 EndY=34 EndZ=0
  constraints (55):
    c: Coincident(g1,g0)
    c: Horizontal(g1)
    c: Coincident(g2,g1)
    c: Vertical(g2)
    c: Coincident(g3,g2)
    c: Horizontal(g3)
    c: Coincident(g3,g0)
    c: DistanceX(g1,g1) = 11
    c: DistanceY(g2,g2) = 0.8
    c: Coincident(g5,g4)
    c: Horizontal(g5)
    c: Coincident(g6,g5)
    c: Vertical(g6)
    c: Coincident(g7,g6)
    c: Horizontal(g7)
    c: Coincident(g7,g4)
    c: Coincident(g9,g8)
    c: Horizontal(g9)
    c: Coincident(g10,g9)
    c: Vertical(g10)
    c: Coincident(g11,g10)
    c: Horizontal(g11)
    c: Coincident(g11,g8)
    c: Coincident(g13,g12)
    c: Horizontal(g13)
    c: Coincident(g14,g13)
    c: Vertical(g14)
    c: Coincident(g15,g14)
    c: Horizontal(g15)
    c: Coincident(g15,g12)
    c: Coincident(g17,g16)
    c: Horizontal(g17)
    c: Coincident(g18,g17)
    c: Vertical(g18)
    c: Coincident(g19,g18)
    c: Horizontal(g19)
    c: Coincident(g19,g16)
    c: Equal(g3,g19)
    c: Equal(g3,g15)
    c: Equal(g3,g11)
    c: Equal(g3,g7)
    c: Equal(g2,g18)
    c: Equal(g2,g14)
    c: Equal(g2,g10)
    c: Equal(g2,g6)
    c: DistanceY(g-4,g4) = 1
    c: DistanceY(g4,g8) = 1
    c: DistanceY(g8,g12) = 1
    c: DistanceY(g12,g16) = 1
    c: DistanceY(g16,g0) = 1
    c: Tangent(g0,g-5)
    c: Tangent(g16,g-5)
    c: Tangent(g12,g-5)
    c: Tangent(g8,g-5)
    c: Tangent(g4,g-5)
FEATURE [PartDesign::Chamfer] Chamfer009
  Angle = 45
  Base = -> Pad017 [Edge147,Edge150]
  BaseFeature = -> Pad017
  ChamferType = 1
  FlipDirection = false
  Refine = true
  Size = 1.5
  Size2 = 2.8
  SupportTransform = false
  Suppressed = false
  UseAllEdges = false
FEATURE [PartDesign::Pocket] Pocket009
  BaseFeature = -> Chamfer009
  Direction = (0,1,-2e-16)
  Length = 1
  Length2 = 5
  Profile = -> Sketch125
  ReferenceAxis = -> Sketch125 [N_Axis]
  Refine = true
  Suppressed = false
  Type = 0
FEATURE [PartDesign::Pad] Pad014
  BaseFeature = -> Pocket009
  Direction = (0,-1,2e-16)
  Length = 0.8
  Length2 = 10
  Profile = -> Sketch120
  ReferenceAxis = -> Sketch120 [N_Axis]
  Refine = true
  Suppressed = false
  Type = 0
FEATURE [Sketcher::SketchObject] Sketch124
  ArcFitTolerance = 1e-06
  AttachmentSupport = -> [Pad014]
  ExternalGeometry = -> [Binder001]
  FullyConstrained = true
  MakeInternals = false
  MapMode = 5
  Placement = pos=(0,-2.8,6e-16) rot=(1,0,0;1.5708rad)
  sketch-geometry (4):
    g0: LineSegment StartX=-129 StartY=39.2 StartZ=0 EndX=-131.599 EndY=31.2 EndZ=0
    g1: LineSegment StartX=-118 StartY=39.2 StartZ=0 EndX=-120.599 EndY=31.2 EndZ=0
    g2: LineSegment StartX=-129 StartY=39.2 StartZ=0 EndX=-118 EndY=39.2 EndZ=0
    g3: LineSegment StartX=-120.599 StartY=31.2 StartZ=0 EndX=-131.599 EndY=31.2 EndZ=0
  constraints (12):
    c: PointOnObject(g0,g-3)
    c: PointOnObject(g1,g-3)
    c: Parallel(g-4,g0)
    c: Parallel(g-4,g1)
    c: Coincident(g2,g0)
    c: Coincident(g2,g1)
    c: DistanceX(g2,g2) = 11
    c: DistanceY(g1,g1) = 8
    c: Coincident(g3,g1)
    c: Horizontal(g3)
    c: Coincident(g3,g0)
    c: DistanceX(g1,g-3) = 118
FEATURE [PartDesign::Pad] Pad018
  BaseFeature = -> Pad014
  Direction = (0,-1,2e-16)
  Length = 1.2
  Length2 = 10
  Profile = -> Sketch124
  ReferenceAxis = -> Sketch124 [N_Axis]
  Refine = true
  Suppressed = false
  Type = 0
FEATURE [Sketcher::SketchObject] Sketch126
  ArcFitTolerance = 1e-06
  AttachmentSupport = -> [Pad018]
  ExternalGeometry = -> [Pad018]
  FullyConstrained = true
  MakeInternals = false
  MapMode = 5
  Placement = pos=(0,-4,0) rot=(1,0,0;1.5708rad)
  sketch-geometry (8):
    g0: LineSegment StartX=-129.877 StartY=36.5 StartZ=0 EndX=-130.137 EndY=35.7 EndZ=0
    g1: LineSegment StartX=-130.69 StartY=34 StartZ=0 EndX=-130.95 EndY=33.2 EndZ=0
    g2: LineSegment StartX=-129.877 StartY=36.5 StartZ=0 EndX=-118.877 EndY=36.5 EndZ=0
    g3: LineSegment StartX=-130.137 StartY=35.7 StartZ=0 EndX=-119.137 EndY=35.7 EndZ=0
    g4: LineSegment StartX=-130.69 StartY=34 StartZ=0 EndX=-119.69 EndY=34 EndZ=0
    g5: LineSegment StartX=-130.95 StartY=33.2 StartZ=0 EndX=-119.95 EndY=33.2 EndZ=0
    g6: LineSegment StartX=-118.877 StartY=36.5 StartZ=0 EndX=-119.137 EndY=35.7 EndZ=0
    g7: LineSegment StartX=-119.69 StartY=34 StartZ=0 EndX=-119.95 EndY=33.2 EndZ=0
  constraints (20):
    c: Coincident(g2,g0)
    c: Horizontal(g2)
    c: Coincident(g3,g0)
    c: Horizontal(g3)
    c: Coincident(g4,g1)
    c: Horizontal(g4)
    c: Coincident(g5,g1)
    c: Horizontal(g5)
    c: Coincident(g6,g2)
    c: Coincident(g6,g3)
    c: Coincident(g7,g4)
    c: Coincident(g7,g5)
    c: Tangent(g0,g-4)
    c: Tangent(g6,g-5)
    c: Tangent(g1,g-4)
    c: Tangent(g7,g-5)
    c: DistanceY(g3,g2) = 0.8
    c: DistanceY(g5,g4) = 0.8
    c: DistanceY(g-6,g1) = 2
    c: DistanceY(g-6,g0) = 4.5
FEATURE [PartDesign::Chamfer] Chamfer008
  Angle = 45
  Base = -> Pad018 [Edge253]
  BaseFeature = -> Pad018
  ChamferType = 1
  FlipDirection = false
  Refine = true
  Size = 1
  Size2 = 6
  SupportTransform = false
  Suppressed = false
  UseAllEdges = false
FEATURE [PartDesign::Pocket] Pocket010
  BaseFeature = -> Chamfer008
  Direction = (0,1,-2e-16)
  Length = 1
  Length2 = 5
  Profile = -> Sketch126
  ReferenceAxis = -> Sketch126 [N_Axis]
  Refine = true
  Suppressed = false
  Type = 0
FEATURE [PartDesign::Pad] Pad015
  BaseFeature = -> Pocket010
  Direction = (0,-1,2e-16)
  Length = 2
  Length2 = 10
  Profile = -> Sketch121
  ReferenceAxis = -> Sketch121 [N_Axis]
  Refine = true
  Suppressed = false
  Type = 0
FEATURE [PartDesign::Pad] Pad016
  BaseFeature = -> Pad015
  Direction = (0,-1,2e-16)
  Length = 1.6
  Length2 = 10
  Profile = -> Sketch122
  ReferenceAxis = -> Sketch122 [N_Axis]
  Refine = true
  Suppressed = false
  Type = 0
FEATURE [Sketcher::SketchObject] Sketch127
  ArcFitTolerance = 1e-06
  AttachmentSupport = -> [Pad016]
  ExternalGeometry = -> [Pad016]
  FullyConstrained = true
  MakeInternals = false
  MapMode = 5
  Placement = pos=(0,0,-80.4316) rot=(1,0,0;3.14159rad)
  sketch-geometry (8):
    g0: LineSegment StartX=-176.685 StartY=3.6 StartZ=0 EndX=-186.685 EndY=3.6 EndZ=0
    g1: LineSegment [constr] StartX=-186.685 StartY=3.6 StartZ=0 EndX=-186.685 EndY=-9e-16 EndZ=0
    g2: LineSegment StartX=-176.685 StartY=3.6 StartZ=0 EndX=-176.685 EndY=0 EndZ=0
    g3: ArcOfEllipse CenterX=-186.685 CenterY=-9e-16 CenterZ=0 NormalX=0 NormalY=0 NormalZ=1 MajorRadius=10 MinorRadius=3.6 AngleXU=1e-16 StartAngle=0 EndAngle=1.5708
    g4: LineSegment [constr] StartX=-176.685 StartY=-2e-15 StartZ=0 EndX=-196.685 EndY=-2e-15 EndZ=0
    g5: LineSegment [constr] StartX=-186.685 StartY=3.6 StartZ=0 EndX=-186.685 EndY=-3.6 EndZ=0
    g6: GeomPoint [constr] X=-177.356 Y=-1e-16 Z=0
    g7: GeomPoint [constr] X=-196.015 Y=-1.9e-15 Z=0
  constraints (13):
    c: Coincident(g0,g-4)
    c: PointOnObject(g0,g-4)
    c: DistanceX(g0,g0) = 10
    c: Coincident(g1,g0)
    c: PointOnObject(g1,g-5)
    c: Vertical(g1)
    c: Coincident(g2,g0)
    c: Coincident(g2,g-5)
    c: InternalAlignment(g4-g7 -> g3) x4
    c: Coincident(g3,g1)
    c: Coincident(g3,g0)
    c: Coincident(g3,g2)
    c: Horizontal(g4)
FEATURE [Sketcher::SketchObject] Sketch128
  ArcFitTolerance = 1e-06
  AttachmentSupport = -> [Pad016]
  ExternalGeometry = -> [Pad016]
  FullyConstrained = true
  MakeInternals = false
  MapMode = 5
  Placement = pos=(0,0,-80.4316) rot=(1,0,0;3.14159rad)
  sketch-geometry (8):
    g0: LineSegment StartX=-215.932 StartY=3.6 StartZ=0 EndX=-215.932 EndY=0 EndZ=0
    g1: LineSegment StartX=-215.932 StartY=3.6 StartZ=0 EndX=-205.932 EndY=3.6 EndZ=0
    g2: LineSegment [constr] StartX=-205.932 StartY=3.6 StartZ=0 EndX=-205.932 EndY=-9e-16 EndZ=0
    g3: ArcOfEllipse CenterX=-205.932 CenterY=-9e-16 CenterZ=0 NormalX=0 NormalY=0 NormalZ=1 MajorRadius=10 MinorRadius=3.6 AngleXU=-3.14159 StartAngle=4.71239 EndAngle=6.28319
    g4: LineSegment [constr] StartX=-215.932 StartY=-1e-15 StartZ=0 EndX=-195.932 EndY=-1e-15 EndZ=0
    g5: LineSegment [constr] StartX=-205.932 StartY=-3.6 StartZ=0 EndX=-205.932 EndY=3.6 EndZ=0
    g6: GeomPoint [constr] X=-215.262 Y=-1e-15 Z=0
    g7: GeomPoint [constr] X=-196.602 Y=-1e-15 Z=0
  constraints (13):
    c: Coincident(g0,g-4)
    c: Coincident(g0,g-5)
    c: Coincident(g1,g0)
    c: PointOnObject(g1,g-3)
    c: DistanceX(g1,g1) = 10
    c: Coincident(g2,g1)
    c: Vertical(g2)
    c: PointOnObject(g2,g-5)
    c: InternalAlignment(g4-g7 -> g3) x4
    c: Coincident(g3,g2)
    c: Coincident(g3,g1)
    c: Coincident(g3,g0)
    c: Horizontal(g4)
FEATURE [PartDesign::SubtractivePipe] SubtractivePipe002
  AuxilleryCurvelinear = true
  AuxillerySpineTangent = false
  BaseFeature = -> Pad016
  Binormal = (0,0,0)
  Mode = 0
  Profile = -> Sketch127
  Refine = true
  Spine = -> Pad016 [Edge280]
  SpineTangent = false
  Suppressed = false
  Transformation = 0
  Transition = 0
FEATURE [PartDesign::SubtractivePipe] SubtractivePipe003
  AuxilleryCurvelinear = true
  AuxillerySpineTangent = false
  BaseFeature = -> SubtractivePipe002
  Binormal = (0,0,0)
  Mode = 0
  Profile = -> Sketch128
  Refine = true
  Spine = -> Pad016 [Edge282,Edge277,Edge278]
  SpineTangent = false
  Suppressed = false
  Transformation = 0
  Transition = 0
FEATURE [Sketcher::SketchObject] Sketch129
  ArcFitTolerance = 1e-06
  AttachmentSupport = -> [Pad016]
  ExternalGeometry = -> [Binder001]
  FullyConstrained = true
  MakeInternals = false
  MapMode = 5
  Placement = pos=(0,-3.6,0) rot=(1,0,0;1.5708rad)
  sketch-geometry (12):
    g0: LineSegment [constr] StartX=-192.176 StartY=-3.18451 StartZ=0 EndX=-181.223 EndY=20.303 EndZ=0
    g1: LineSegment [constr] StartX=-202.765 StartY=20.303 StartZ=0 EndX=-181.223 EndY=20.303 EndZ=0
    g2: LineSegment StartX=-202.765 StartY=20.303 StartZ=0 EndX=-181.223 EndY=20.303 EndZ=0
    g3: LineSegment StartX=-192.176 StartY=-3.18451 StartZ=0 EndX=-196.804 EndY=-13.1107 EndZ=0
    g4: ArcOfCircle CenterX=-207.583 CenterY=4 CenterZ=0 NormalX=0 NormalY=0 NormalZ=1 AngleXU=0 Radius=17 StartAngle=5.84685 EndAngle=7.56663
    g5: ArcOfEllipse CenterX=-181.223 CenterY=8.55923 CenterZ=0 NormalX=0 NormalY=0 NormalZ=1 MajorRadius=23.4779 MinorRadius=11.7437 AngleXU=2e-16 StartAngle=4.71239 EndAngle=7.85398
    g6: LineSegment [constr] StartX=-157.745 StartY=8.55923 StartZ=0 EndX=-204.701 EndY=8.55923 EndZ=0
    g7: LineSegment [constr] StartX=-181.223 StartY=20.303 StartZ=0 EndX=-181.223 EndY=-3.18451 EndZ=0
    g8: GeomPoint [constr] X=-160.894 Y=8.55923 Z=0
    g9: GeomPoint [constr] X=-201.553 Y=8.55923 Z=0
    g10: ArcOfCircle CenterX=-181.223 CenterY=-20.3763 CenterZ=0 NormalX=0 NormalY=0 NormalZ=1 AngleXU=0 Radius=17.1918 StartAngle=1.57079 EndAngle=2.70526
    g11: GeomPoint [constr] X=-181.223 Y=-3.18451 Z=0
  constraints (23):
    c: Coincident(g0,g-5)
    c: Coincident(g1,g-6)
    c: Horizontal(g1)
    c: Coincident(g1,g0)
    c: Parallel(g0,g-4)
    c: Coincident(g2,g1)
    c: Coincident(g2,g0)
    c: Coincident(g3,g0)
    c: Equal(g4,g-5)
    c: Coincident(g4,g1)
    c: Coincident(g4,g0)
    c: InternalAlignment(g6-g9 -> g5) x4
    c: Vertical(g5,g0)
    c: Horizontal(g6)
    c: Coincident(g5,g0)
    c: DistanceX(g6,g-3) = 10.1
    c: Tangent(g10,g3) = -1.5708
    c: PointOnObject(g11,g10)
    c: Tangent(g5,g10,g11) = 1.5708
    c: Coincident(g10,g5)
    c: Coincident(g11,g7)
    c: Parallel(g3,g-4)
    c: Horizontal(g5,g0)
FEATURE [Sketcher::SketchObject] Sketch130
  ArcFitTolerance = 1e-06
  AttachmentOffset = pos=(0,0,-1.6) rot=(0,0,1;0rad)
  AttachmentSupport = -> [Pad016]
  ExternalGeometry = -> [Binder001]
  FullyConstrained = true
  MakeInternals = false
  MapMode = 5
  Placement = pos=(0,-2,-4e-16) rot=(1,0,0;1.5708rad)
  sketch-geometry (12):
    g0: LineSegment [constr] StartX=-192.176 StartY=-3.18451 StartZ=0 EndX=-181.223 EndY=20.303 EndZ=0
    g1: LineSegment [constr] StartX=-202.765 StartY=20.303 StartZ=0 EndX=-181.223 EndY=20.303 EndZ=0
    g2: LineSegment StartX=-202.765 StartY=20.303 StartZ=0 EndX=-181.223 EndY=20.303 EndZ=0
    g3: LineSegment StartX=-192.176 StartY=-3.18451 StartZ=0 EndX=-193.827 EndY=-6.72678 EndZ=0
    g4: ArcOfCircle CenterX=-207.583 CenterY=4 CenterZ=0 NormalX=0 NormalY=0 NormalZ=1 AngleXU=0 Radius=17 StartAngle=5.84685 EndAngle=7.56663
    g5: ArcOfEllipse CenterX=-181.223 CenterY=10.803 CenterZ=0 NormalX=0 NormalY=0 NormalZ=1 MajorRadius=14.4779 MinorRadius=9.5 AngleXU=0 StartAngle=4.71239 EndAngle=7.85398
    g6: LineSegment [constr] StartX=-166.745 StartY=10.803 StartZ=0 EndX=-195.701 EndY=10.803 EndZ=0
    g7: LineSegment [constr] StartX=-181.223 StartY=20.303 StartZ=0 EndX=-181.223 EndY=1.30297 EndZ=0
    g8: GeomPoint [constr] X=-170.298 Y=10.803 Z=0
    g9: GeomPoint [constr] X=-192.148 Y=10.803 Z=0
    g10: ArcOfCircle CenterX=-181.223 CenterY=-12.6042 CenterZ=0 NormalX=0 NormalY=0 NormalZ=1 AngleXU=0 Radius=13.9072 StartAngle=1.5708 EndAngle=2.70526
    g11: GeomPoint [constr] X=-181.223 Y=1.30297 Z=0
  constraints (23):
    c: Coincident(g0,g-5)
    c: Coincident(g1,g-6)
    c: Horizontal(g1)
    c: Coincident(g1,g0)
    c: Parallel(g0,g-4)
    c: Coincident(g2,g1)
    c: Coincident(g2,g0)
    c: Coincident(g3,g0)
    c: Equal(g4,g-5)
    c: Coincident(g4,g1)
    c: Coincident(g4,g0)
    c: InternalAlignment(g6-g9 -> g5) x4
    c: Vertical(g5,g0)
    c: Horizontal(g6)
    c: Coincident(g5,g0)
    c: DistanceX(g6,g-3) = 19.1
    c: Tangent(g10,g3) = -1.5708
    c: PointOnObject(g11,g10)
    c: Tangent(g5,g10,g11) = 1.5708
    c: Coincident(g10,g5)
    c: Coincident(g11,g7)
    c: Parallel(g3,g-4)
    c: DistanceY(g5,g0) = 19
FEATURE [Part::Part2DObjectPython] Clone2D001  label="Sketch130 (2D)"  # Draft 2D object (typed FeaturePython)
  Fuse = false
  Objects = -> [Sketch130]
  Placement = pos=(0,-2,-4e-16) rot=(1,0,0;1.5708rad)
  Scale = (1,1,1)
FEATURE [Sketcher::SketchObject] Sketch131
  ArcFitTolerance = 1e-06
  AttachmentOffset = pos=(0,0,-3.8) rot=(0,0,1;0rad)
  AttachmentSupport = -> [Pad016]
  ExternalGeometry = -> [Binder001]
  FullyConstrained = true
  MakeInternals = false
  MapMode = 5
  Placement = pos=(0,0.2,-8e-16) rot=(1,0,0;1.5708rad)
  sketch-geometry (1):
    g0: GeomPoint X=-197.47 Y=8.55923 Z=0
  constraints (1):
    c: Symmetric(g-6,g-4,g0)
FEATURE [PartDesign::SubtractiveLoft] SubtractiveLoft002
  BaseFeature = -> SubtractivePipe003
  Closed = false
  Profile = -> Sketch129
  Refine = true
  Ruled = false
  Sections = -> [Sketch130]
  Suppressed = false
FEATURE [PartDesign::SubtractiveLoft] SubtractiveLoft003
  BaseFeature = -> SubtractiveLoft002
  Closed = false
  Profile = -> Clone2D001
  Refine = true
  Ruled = false
  Sections = -> [Sketch131]
  Suppressed = false
FEATURE [PartDesign::Chamfer] Chamfer010
  Angle = 45
  Base = -> SubtractiveLoft003 [Edge209,Edge210,Edge212,Edge211,Edge203]
  BaseFeature = -> SubtractiveLoft003
  ChamferType = 0
  FlipDirection = false
  Refine = true
  Size = 1.5
  Size2 = 1
  SupportTransform = false
  Suppressed = false
  UseAllEdges = false
FEATURE [PartDesign::Chamfer] Chamfer011
  Angle = 45
  Base = -> Chamfer010 [Edge10]
  BaseFeature = -> Chamfer010
  ChamferType = 0
  FlipDirection = false
  Refine = true
  Size = 3.5
  Size2 = 1
  SupportTransform = false
  Suppressed = false
  UseAllEdges = false
FEATURE [PartDesign::Chamfer] Chamfer012
  Angle = 45
  Base = -> Chamfer011 [Edge10]
  BaseFeature = -> Chamfer011
  ChamferType = 0
  FlipDirection = false
  Refine = true
  Size = 3.5
  Size2 = 1
  SupportTransform = false
  Suppressed = false
  UseAllEdges = false
FEATURE [PartDesign::Chamfer] Chamfer013
  Angle = 45
  Base = -> Chamfer012 [Edge105,Edge104,Edge103,Edge101,Edge98]
  BaseFeature = -> Chamfer012
  ChamferType = 0
  FlipDirection = false
  Refine = true
  Size = 1.9
  Size2 = 1
  SupportTransform = false
  Suppressed = false
  UseAllEdges = false
FEATURE [PartDesign::Chamfer] Chamfer014
  Angle = 45
  Base = -> Chamfer013 [Edge229]
  BaseFeature = -> Chamfer013
  ChamferType = 0
  FlipDirection = false
  Refine = true
  Size = 1.9
  Size2 = 1
  SupportTransform = false
  Suppressed = false
  UseAllEdges = false
FEATURE [PartDesign::Fillet] Fillet007
  Base = -> Chamfer014 [Edge144]
  BaseFeature = -> Chamfer014
  Radius = 1.9
  Refine = true
  SupportTransform = false
  Suppressed = false
  UseAllEdges = false
FEATURE [PartDesign::Fillet] Fillet008
  Base = -> Fillet007 [Edge156,Edge38,Edge46]
  BaseFeature = -> Fillet007
  Radius = 1.1
  Refine = true
  SupportTransform = false
  Suppressed = false
  UseAllEdges = false
FEATURE [Sketcher::SketchObject] Sketch132
  ArcFitTolerance = 1e-06
  AttachmentSupport = -> [Pad016]
  ExternalGeometry = -> [Binder001]
  FullyConstrained = true
  MakeInternals = false
  MapMode = 5
  Placement = pos=(0,-3.6,0) rot=(1,0,0;1.5708rad)
  sketch-geometry (3):
    g0: LineSegment [constr] StartX=-215.42 StartY=-53.0314 StartZ=0 EndX=-167.782 EndY=-53.0314 EndZ=0
    g1: Circle CenterX=-191.282 CenterY=-53.0314 CenterZ=0 NormalX=0 NormalY=0 NormalZ=1 AngleXU=0 Radius=11.5
    g2: Circle CenterX=-191.282 CenterY=-53.0314 CenterZ=0 NormalX=0 NormalY=0 NormalZ=1 AngleXU=0 Radius=10.7
  constraints (8):
    c: Coincident(g0,g-3)
    c: PointOnObject(g0,g-4)
    c: Horizontal(g0)
    c: Diameter(g1) = 23
    c: PointOnObject(g1,g0)
    c: DistanceX(g1,g0) = 23.5
    c: Diameter(g2) = 21.4
    c: Coincident(g2,g1)
FEATURE [PartDesign::Pocket] Pocket011
  BaseFeature = -> Fillet008
  Direction = (0,1,-2e-16)
  Length = 0.8
  Length2 = 5
  Profile = -> Sketch132
  ReferenceAxis = -> Sketch132 [N_Axis]
  Refine = true
  Suppressed = false
  Type = 0
FEATURE [PartDesign::Body] Body007  label="lato DX"
  AllowCompound = false
  Group = -> [Binder001,Sketch114,Pad011,Sketch115,Pocket006,Sketch116,Pad012,Sketch117,Pocket007,Sketch118,Pad013,Sketch119,Pocket008,Pad017,Chamfer009,Pocket009,Sketch123,Sketch120,Pad014,Pad018,Chamfer008,Pocket010,Sketch121,Pad015,Sketch122,Pad016,Sketch124,Sketch125,Sketch126,Sketch127,Sketch128,SubtractivePipe002,SubtractivePipe003,Sketch129,Sketch130,Clone2D001,Sketch131,SubtractiveLoft002,+10 more]
  Origin = -> Origin007
  Tip = -> Pocket011
